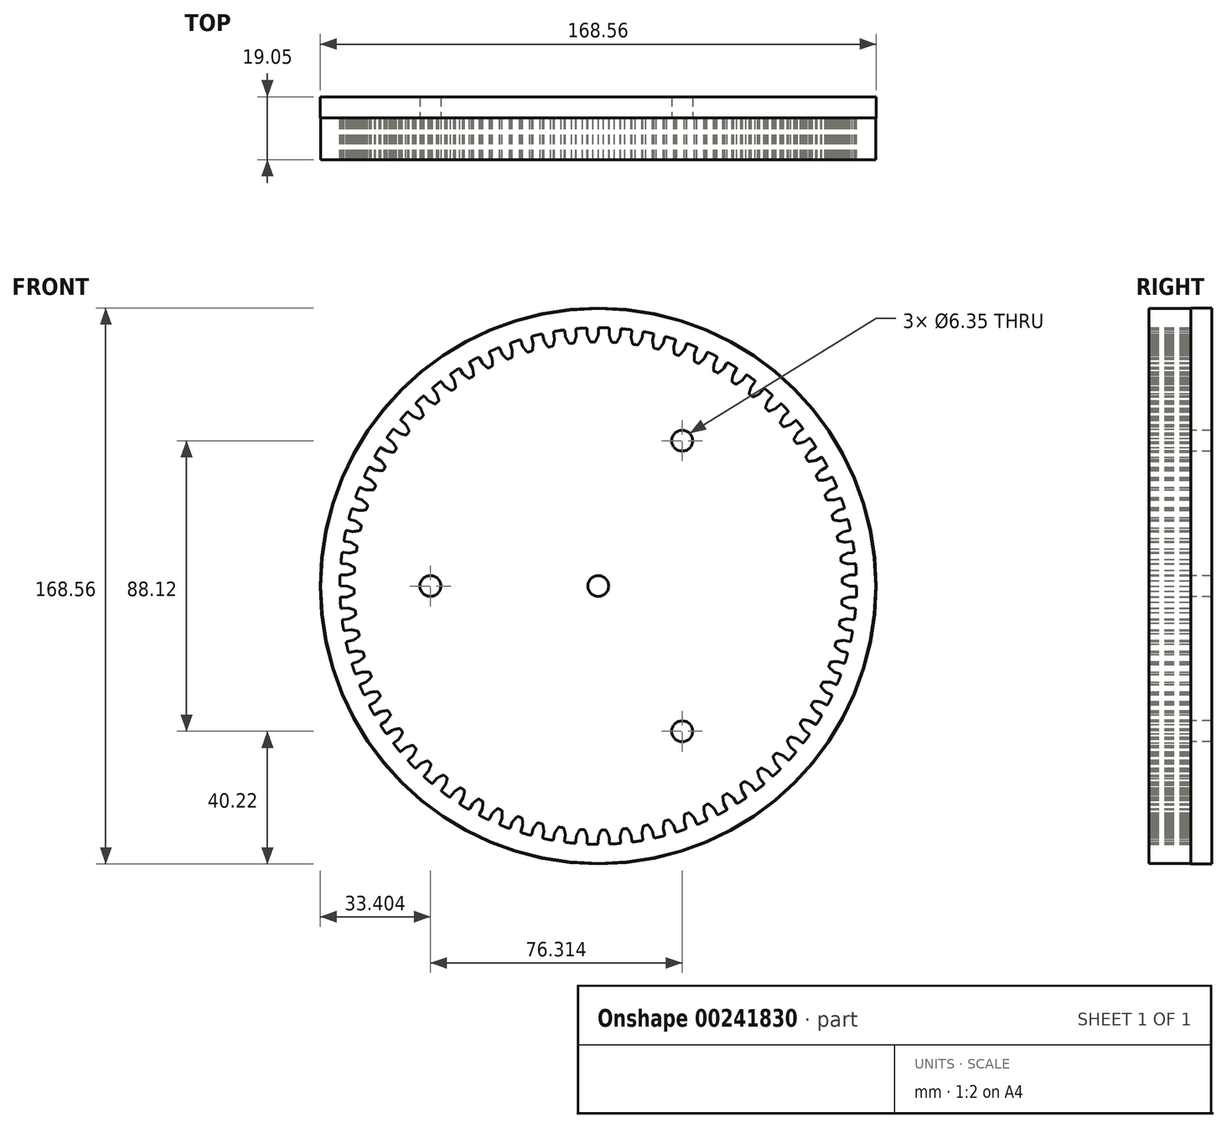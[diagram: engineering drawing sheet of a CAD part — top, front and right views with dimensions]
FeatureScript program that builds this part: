
annotation { "Feature Type Name" : "Feature", "Feature Type Description" : "" }
export const myFeature = defineFeature(function(context is Context, id is Id, definition is map)
    precondition{}
    {
        {
            var Q0;
            Q0=qCreatedBy(makeId("Front.planeOp"),FACE);
            var sketch = newSketch(context, id + "F0", { "sketchPlane" : qUnion([Q0])});
            skArc(sketch, "E0", {"start": v(-3.79, 78.22) * mm, "mid": v(-5.3, 78.14) * mm, "end": v(-6.81, 78.02) * mm});
            skPoint(sketch, "E1.orphan", {"position": v(0.25, 70.42) * mm});
            skPoint(sketch, "E2.orphan", {"position": v(-3.32, 70.34) * mm});
            skArc(sketch, "E3.MirrorCS", {"start": v(-3.32, 76.11) * mm, "mid": v(-2.93, 75.15) * mm, "end": v(-2.48, 74.2) * mm});
            skLineSegment(sketch, "E4.MirrorCS", {"start": v(-2.14, 74) * mm, "end": v(-1.63, 74) * mm});
            skLineSegment(sketch, "E5.MirrorCS", {"start": v(-1.12, 74.01) * mm, "end": v(-1.63, 74) * mm});
            skArc(sketch, "E6.MirrorCS", {"start": v(0, 76.17) * mm, "mid": v(-0.36, 75.19) * mm, "end": v(-0.78, 74.23) * mm});
            skLineSegment(sketch, "E7", {"start": v(-3.32, 76.11) * mm, "end": v(-3.39, 77.86) * mm});
            skLineSegment(sketch, "E8", {"start": v(0, 76.17) * mm, "end": v(0.01, 77.94) * mm});
            skCircle(sketch, "E9", {"center": v(0, 0) * mm, "radius": 84.1 * mm});
            skPoint(sketch, "E10.visualSharp", {"position": v(-3.4, 78.24) * mm});
            skArc(sketch, "E10.filletArc", {"start": v(-3.39, 77.86) * mm, "mid": v(-3.51, 78.13) * mm, "end": v(-3.79, 78.22) * mm});
            skPoint(sketch, "E11.visualSharp", {"position": v(0.01, 78.32) * mm});
            skArc(sketch, "E11.filletArc", {"start": v(0.4, 78.32) * mm, "mid": v(0.12, 78.2) * mm, "end": v(0.01, 77.94) * mm});
            skPoint(sketch, "E12.visualSharp", {"position": v(-0.88, 74.02) * mm});
            skArc(sketch, "E12.filletArc", {"start": v(-1.12, 74.01) * mm, "mid": v(-0.92, 74.08) * mm, "end": v(-0.78, 74.23) * mm});
            skPoint(sketch, "E13.visualSharp", {"position": v(-2.37, 74) * mm});
            skArc(sketch, "E13.filletArc", {"start": v(-2.48, 74.2) * mm, "mid": v(-2.34, 74.05) * mm, "end": v(-2.14, 74) * mm});
            skArc(sketch, "E14.1.0", {"start": v(-6.64, 75.88) * mm, "mid": v(-6.92, 74.87) * mm, "end": v(-7.25, 73.88) * mm});
            skArc(sketch, "E14.1.1", {"start": v(-9.94, 75.53) * mm, "mid": v(-9.47, 74.6) * mm, "end": v(-8.94, 73.7) * mm});
            skPoint(sketch, "E14.1.2", {"position": v(-6.81, 78.02) * mm});
            skPoint(sketch, "E14.1.3", {"position": v(-7.33, 73.66) * mm});
            skLineSegment(sketch, "E14.1.4", {"start": v(-6.64, 75.88) * mm, "end": v(-6.78, 77.64) * mm});
            skLineSegment(sketch, "E14.1.5", {"start": v(-9.94, 75.53) * mm, "end": v(-10.16, 77.27) * mm});
            skPoint(sketch, "E14.1.6", {"position": v(-8.81, 73.5) * mm});
            skLineSegment(sketch, "E14.1.7", {"start": v(-7.56, 73.64) * mm, "end": v(-8.07, 73.58) * mm});
            skLineSegment(sketch, "E14.1.8", {"start": v(-8.58, 73.53) * mm, "end": v(-8.07, 73.58) * mm});
            skArc(sketch, "E14.1.9", {"start": v(-7.56, 73.64) * mm, "mid": v(-7.37, 73.71) * mm, "end": v(-7.25, 73.88) * mm});
            skArc(sketch, "E14.1.10", {"start": v(-8.94, 73.7) * mm, "mid": v(-8.78, 73.57) * mm, "end": v(-8.58, 73.53) * mm});
            skArc(sketch, "E14.1.11", {"start": v(-6.43, 78.05) * mm, "mid": v(-6.7, 77.92) * mm, "end": v(-6.78, 77.64) * mm});
            skArc(sketch, "E14.1.12", {"start": v(-10.16, 77.27) * mm, "mid": v(-10.3, 77.52) * mm, "end": v(-10.6, 77.6) * mm});
            skArc(sketch, "E14.2.0", {"start": v(-13.23, 75) * mm, "mid": v(-13.41, 73.98) * mm, "end": v(-13.66, 72.97) * mm});
            skArc(sketch, "E14.2.1", {"start": v(-16.49, 74.38) * mm, "mid": v(-15.93, 73.5) * mm, "end": v(-15.33, 72.65) * mm});
            skPoint(sketch, "E14.2.2", {"position": v(-13.59, 77.13) * mm});
            skPoint(sketch, "E14.2.3", {"position": v(-13.72, 72.74) * mm});
            skLineSegment(sketch, "E14.2.4", {"start": v(-13.23, 75) * mm, "end": v(-13.52, 76.75) * mm});
            skLineSegment(sketch, "E14.2.5", {"start": v(-16.49, 74.38) * mm, "end": v(-16.86, 76.09) * mm});
            skPoint(sketch, "E14.2.6", {"position": v(-15.19, 72.46) * mm});
            skLineSegment(sketch, "E14.2.7", {"start": v(-13.95, 72.7) * mm, "end": v(-14.45, 72.6) * mm});
            skLineSegment(sketch, "E14.2.8", {"start": v(-14.96, 72.5) * mm, "end": v(-14.45, 72.6) * mm});
            skArc(sketch, "E14.2.9", {"start": v(-13.95, 72.7) * mm, "mid": v(-13.77, 72.8) * mm, "end": v(-13.66, 72.97) * mm});
            skArc(sketch, "E14.2.10", {"start": v(-15.33, 72.65) * mm, "mid": v(-15.16, 72.52) * mm, "end": v(-14.96, 72.5) * mm});
            skArc(sketch, "E14.2.11", {"start": v(-13.21, 77.2) * mm, "mid": v(-13.46, 77.04) * mm, "end": v(-13.52, 76.75) * mm});
            skArc(sketch, "E14.2.12", {"start": v(-16.86, 76.09) * mm, "mid": v(-17.03, 76.33) * mm, "end": v(-17.32, 76.38) * mm});
            skArc(sketch, "E14.3.0", {"start": v(-19.71, 73.57) * mm, "mid": v(-19.81, 72.53) * mm, "end": v(-19.97, 71.5) * mm});
            skArc(sketch, "E14.3.1", {"start": v(-22.9, 72.66) * mm, "mid": v(-22.28, 71.83) * mm, "end": v(-21.6, 71.04) * mm});
            skPoint(sketch, "E14.3.2", {"position": v(-20.26, 75.65) * mm});
            skPoint(sketch, "E14.3.3", {"position": v(-20, 71.27) * mm});
            skLineSegment(sketch, "E14.3.4", {"start": v(-19.71, 73.57) * mm, "end": v(-20.16, 75.28) * mm});
            skLineSegment(sketch, "E14.3.5", {"start": v(-22.9, 72.66) * mm, "end": v(-23.43, 74.33) * mm});
            skPoint(sketch, "E14.3.6", {"position": v(-21.44, 70.86) * mm});
            skLineSegment(sketch, "E14.3.7", {"start": v(-20.23, 71.2) * mm, "end": v(-20.72, 71.06) * mm});
            skLineSegment(sketch, "E14.3.8", {"start": v(-21.22, 70.92) * mm, "end": v(-20.72, 71.06) * mm});
            skArc(sketch, "E14.3.9", {"start": v(-20.23, 71.2) * mm, "mid": v(-20.06, 71.32) * mm, "end": v(-19.97, 71.5) * mm});
            skArc(sketch, "E14.3.10", {"start": v(-21.6, 71.04) * mm, "mid": v(-21.43, 70.92) * mm, "end": v(-21.22, 70.92) * mm});
            skArc(sketch, "E14.3.11", {"start": v(-19.89, 75.75) * mm, "mid": v(-20.12, 75.57) * mm, "end": v(-20.16, 75.28) * mm});
            skArc(sketch, "E14.3.12", {"start": v(-23.43, 74.33) * mm, "mid": v(-23.61, 74.55) * mm, "end": v(-23.9, 74.58) * mm});
            skArc(sketch, "E14.4.0", {"start": v(-26.05, 71.57) * mm, "mid": v(-26.06, 70.53) * mm, "end": v(-26.12, 69.5) * mm});
            skArc(sketch, "E14.4.1", {"start": v(-29.16, 70.39) * mm, "mid": v(-28.45, 69.61) * mm, "end": v(-27.71, 68.88) * mm});
            skPoint(sketch, "E14.4.2", {"position": v(-26.77, 73.6) * mm});
            skPoint(sketch, "E14.4.3", {"position": v(-26.15, 69.26) * mm});
            skLineSegment(sketch, "E14.4.4", {"start": v(-26.05, 71.57) * mm, "end": v(-26.65, 73.24) * mm});
            skLineSegment(sketch, "E14.4.5", {"start": v(-29.16, 70.39) * mm, "end": v(-29.81, 72) * mm});
            skPoint(sketch, "E14.4.6", {"position": v(-27.54, 68.72) * mm});
            skLineSegment(sketch, "E14.4.7", {"start": v(-26.36, 69.17) * mm, "end": v(-26.84, 68.98) * mm});
            skLineSegment(sketch, "E14.4.8", {"start": v(-27.32, 68.8) * mm, "end": v(-26.84, 68.98) * mm});
            skArc(sketch, "E14.4.9", {"start": v(-26.36, 69.17) * mm, "mid": v(-26.2, 69.3) * mm, "end": v(-26.12, 69.5) * mm});
            skArc(sketch, "E14.4.10", {"start": v(-27.71, 68.88) * mm, "mid": v(-27.53, 68.79) * mm, "end": v(-27.32, 68.8) * mm});
            skArc(sketch, "E14.4.11", {"start": v(-26.42, 73.73) * mm, "mid": v(-26.63, 73.53) * mm, "end": v(-26.65, 73.24) * mm});
            skArc(sketch, "E14.4.12", {"start": v(-29.81, 72) * mm, "mid": v(-30.02, 72.21) * mm, "end": v(-30.31, 72.21) * mm});
            skArc(sketch, "E14.5.0", {"start": v(-32.19, 69.03) * mm, "mid": v(-32.1, 68) * mm, "end": v(-32.08, 66.95) * mm});
            skArc(sketch, "E14.5.1", {"start": v(-35.18, 67.58) * mm, "mid": v(-34.41, 66.87) * mm, "end": v(-33.6, 66.2) * mm});
            skPoint(sketch, "E14.5.2", {"position": v(-33.09, 70.98) * mm});
            skPoint(sketch, "E14.5.3", {"position": v(-32.08, 66.71) * mm});
            skLineSegment(sketch, "E14.5.4", {"start": v(-32.19, 69.03) * mm, "end": v(-32.93, 70.64) * mm});
            skLineSegment(sketch, "E14.5.5", {"start": v(-35.18, 67.58) * mm, "end": v(-35.98, 69.13) * mm});
            skPoint(sketch, "E14.5.6", {"position": v(-33.42, 66.06) * mm});
            skLineSegment(sketch, "E14.5.7", {"start": v(-32.3, 66.6) * mm, "end": v(-32.75, 66.38) * mm});
            skLineSegment(sketch, "E14.5.8", {"start": v(-33.21, 66.16) * mm, "end": v(-32.75, 66.38) * mm});
            skArc(sketch, "E14.5.9", {"start": v(-32.3, 66.6) * mm, "mid": v(-32.14, 66.75) * mm, "end": v(-32.08, 66.95) * mm});
            skArc(sketch, "E14.5.10", {"start": v(-33.6, 66.2) * mm, "mid": v(-33.42, 66.13) * mm, "end": v(-33.21, 66.16) * mm});
            skArc(sketch, "E14.5.11", {"start": v(-32.74, 71.14) * mm, "mid": v(-32.94, 70.93) * mm, "end": v(-32.93, 70.64) * mm});
            skArc(sketch, "E14.5.12", {"start": v(-35.98, 69.13) * mm, "mid": v(-36.2, 69.32) * mm, "end": v(-36.5, 69.3) * mm});
            skArc(sketch, "E14.6.0", {"start": v(-38.08, 65.96) * mm, "mid": v(-37.9, 64.93) * mm, "end": v(-37.8, 63.9) * mm});
            skArc(sketch, "E14.6.1", {"start": v(-40.93, 64.25) * mm, "mid": v(-40.1, 63.62) * mm, "end": v(-39.25, 63.02) * mm});
            skPoint(sketch, "E14.6.2", {"position": v(-39.15, 67.83) * mm});
            skPoint(sketch, "E14.6.3", {"position": v(-37.77, 63.66) * mm});
            skLineSegment(sketch, "E14.6.4", {"start": v(-38.08, 65.96) * mm, "end": v(-38.96, 67.5) * mm});
            skLineSegment(sketch, "E14.6.5", {"start": v(-40.93, 64.25) * mm, "end": v(-41.87, 65.73) * mm});
            skPoint(sketch, "E14.6.6", {"position": v(-39.05, 62.9) * mm});
            skLineSegment(sketch, "E14.6.7", {"start": v(-37.97, 63.54) * mm, "end": v(-38.4, 63.27) * mm});
            skLineSegment(sketch, "E14.6.8", {"start": v(-38.85, 63.01) * mm, "end": v(-38.4, 63.27) * mm});
            skArc(sketch, "E14.6.9", {"start": v(-37.97, 63.54) * mm, "mid": v(-37.83, 63.7) * mm, "end": v(-37.8, 63.9) * mm});
            skArc(sketch, "E14.6.10", {"start": v(-39.25, 63.02) * mm, "mid": v(-39.05, 62.96) * mm, "end": v(-38.85, 63.01) * mm});
            skArc(sketch, "E14.6.11", {"start": v(-38.82, 68.02) * mm, "mid": v(-39, 67.79) * mm, "end": v(-38.96, 67.5) * mm});
            skArc(sketch, "E14.6.12", {"start": v(-41.87, 65.73) * mm, "mid": v(-42.1, 65.9) * mm, "end": v(-42.4, 65.85) * mm});
            skArc(sketch, "E14.7.0", {"start": v(-43.69, 62.4) * mm, "mid": v(-43.42, 61.38) * mm, "end": v(-43.22, 60.36) * mm});
            skArc(sketch, "E14.7.1", {"start": v(-46.38, 60.44) * mm, "mid": v(-45.5, 59.88) * mm, "end": v(-44.6, 59.36) * mm});
            skPoint(sketch, "E14.7.2", {"position": v(-44.91, 64.16) * mm});
            skPoint(sketch, "E14.7.3", {"position": v(-43.18, 60.13) * mm});
            skLineSegment(sketch, "E14.7.4", {"start": v(-43.69, 62.4) * mm, "end": v(-44.7, 63.85) * mm});
            skLineSegment(sketch, "E14.7.5", {"start": v(-46.38, 60.44) * mm, "end": v(-47.43, 61.83) * mm});
            skPoint(sketch, "E14.7.6", {"position": v(-44.39, 59.25) * mm});
            skLineSegment(sketch, "E14.7.7", {"start": v(-43.37, 59.99) * mm, "end": v(-43.78, 59.69) * mm});
            skLineSegment(sketch, "E14.7.8", {"start": v(-44.2, 59.39) * mm, "end": v(-43.78, 59.69) * mm});
            skArc(sketch, "E14.7.9", {"start": v(-43.37, 59.99) * mm, "mid": v(-43.24, 60.15) * mm, "end": v(-43.22, 60.36) * mm});
            skArc(sketch, "E14.7.10", {"start": v(-44.6, 59.36) * mm, "mid": v(-44.4, 59.32) * mm, "end": v(-44.2, 59.39) * mm});
            skArc(sketch, "E14.7.11", {"start": v(-44.6, 64.38) * mm, "mid": v(-44.76, 64.13) * mm, "end": v(-44.7, 63.85) * mm});
            skArc(sketch, "E14.7.12", {"start": v(-47.43, 61.83) * mm, "mid": v(-47.69, 61.98) * mm, "end": v(-47.97, 61.9) * mm});
            skArc(sketch, "E14.8.0", {"start": v(-48.96, 58.35) * mm, "mid": v(-48.6, 57.36) * mm, "end": v(-48.31, 56.36) * mm});
            skArc(sketch, "E14.8.1", {"start": v(-51.47, 56.17) * mm, "mid": v(-50.55, 55.68) * mm, "end": v(-49.6, 55.25) * mm});
            skPoint(sketch, "E14.8.2", {"position": v(-50.33, 60) * mm});
            skPoint(sketch, "E14.8.3", {"position": v(-48.26, 56.14) * mm});
            skLineSegment(sketch, "E14.8.4", {"start": v(-48.96, 58.35) * mm, "end": v(-50.09, 59.7) * mm});
            skLineSegment(sketch, "E14.8.5", {"start": v(-51.47, 56.17) * mm, "end": v(-52.64, 57.46) * mm});
            skPoint(sketch, "E14.8.6", {"position": v(-49.38, 55.16) * mm});
            skLineSegment(sketch, "E14.8.7", {"start": v(-48.43, 55.98) * mm, "end": v(-48.81, 55.64) * mm});
            skLineSegment(sketch, "E14.8.8", {"start": v(-49.2, 55.31) * mm, "end": v(-48.81, 55.64) * mm});
            skArc(sketch, "E14.8.9", {"start": v(-48.43, 55.98) * mm, "mid": v(-48.32, 56.16) * mm, "end": v(-48.31, 56.36) * mm});
            skArc(sketch, "E14.8.10", {"start": v(-49.6, 55.25) * mm, "mid": v(-49.4, 55.22) * mm, "end": v(-49.2, 55.31) * mm});
            skArc(sketch, "E14.8.11", {"start": v(-50.04, 60.25) * mm, "mid": v(-50.17, 59.99) * mm, "end": v(-50.09, 59.7) * mm});
            skArc(sketch, "E14.8.12", {"start": v(-52.64, 57.46) * mm, "mid": v(-52.9, 57.59) * mm, "end": v(-53.18, 57.49) * mm});
            skArc(sketch, "E14.9.0", {"start": v(-53.86, 53.86) * mm, "mid": v(-53.42, 52.91) * mm, "end": v(-53.04, 51.94) * mm});
            skArc(sketch, "E14.9.1", {"start": v(-56.17, 51.47) * mm, "mid": v(-55.2, 51.07) * mm, "end": v(-54.23, 50.72) * mm});
            skPoint(sketch, "E14.9.2", {"position": v(-55.37, 55.39) * mm});
            skPoint(sketch, "E14.9.3", {"position": v(-52.96, 51.72) * mm});
            skLineSegment(sketch, "E14.9.4", {"start": v(-53.86, 53.86) * mm, "end": v(-55.1, 55.12) * mm});
            skLineSegment(sketch, "E14.9.5", {"start": v(-56.17, 51.47) * mm, "end": v(-57.45, 52.66) * mm});
            skPoint(sketch, "E14.9.6", {"position": v(-54, 50.65) * mm});
            skLineSegment(sketch, "E14.9.7", {"start": v(-53.12, 51.55) * mm, "end": v(-53.48, 51.18) * mm});
            skLineSegment(sketch, "E14.9.8", {"start": v(-53.84, 50.81) * mm, "end": v(-53.48, 51.18) * mm});
            skArc(sketch, "E14.9.9", {"start": v(-53.12, 51.55) * mm, "mid": v(-53.03, 51.73) * mm, "end": v(-53.04, 51.94) * mm});
            skArc(sketch, "E14.9.10", {"start": v(-54.23, 50.72) * mm, "mid": v(-54.02, 50.7) * mm, "end": v(-53.84, 50.81) * mm});
            skArc(sketch, "E14.9.11", {"start": v(-55.1, 55.66) * mm, "mid": v(-55.21, 55.39) * mm, "end": v(-55.1, 55.12) * mm});
            skArc(sketch, "E14.9.12", {"start": v(-57.45, 52.66) * mm, "mid": v(-57.73, 52.76) * mm, "end": v(-58, 52.63) * mm});
            skArc(sketch, "E14.10.0", {"start": v(-58.35, 48.96) * mm, "mid": v(-57.83, 48.05) * mm, "end": v(-57.37, 47.12) * mm});
            skArc(sketch, "E14.10.1", {"start": v(-60.44, 46.38) * mm, "mid": v(-59.45, 46.06) * mm, "end": v(-58.44, 45.8) * mm});
            skPoint(sketch, "E14.10.2", {"position": v(-59.99, 50.35) * mm});
            skPoint(sketch, "E14.10.3", {"position": v(-57.27, 46.9) * mm});
            skLineSegment(sketch, "E14.10.4", {"start": v(-58.35, 48.96) * mm, "end": v(-59.7, 50.1) * mm});
            skLineSegment(sketch, "E14.10.5", {"start": v(-60.44, 46.38) * mm, "end": v(-61.82, 47.45) * mm});
            skPoint(sketch, "E14.10.6", {"position": v(-58.2, 45.75) * mm});
            skLineSegment(sketch, "E14.10.7", {"start": v(-57.42, 46.72) * mm, "end": v(-57.73, 46.32) * mm});
            skLineSegment(sketch, "E14.10.8", {"start": v(-58.06, 45.93) * mm, "end": v(-57.73, 46.32) * mm});
            skArc(sketch, "E14.10.9", {"start": v(-57.42, 46.72) * mm, "mid": v(-57.34, 46.91) * mm, "end": v(-57.37, 47.12) * mm});
            skArc(sketch, "E14.10.10", {"start": v(-58.44, 45.8) * mm, "mid": v(-58.23, 45.8) * mm, "end": v(-58.06, 45.93) * mm});
            skArc(sketch, "E14.10.11", {"start": v(-59.74, 50.64) * mm, "mid": v(-59.83, 50.36) * mm, "end": v(-59.7, 50.1) * mm});
            skArc(sketch, "E14.10.12", {"start": v(-61.82, 47.45) * mm, "mid": v(-62.1, 47.53) * mm, "end": v(-62.36, 47.38) * mm});
            skArc(sketch, "E14.11.0", {"start": v(-62.4, 43.69) * mm, "mid": v(-61.8, 42.83) * mm, "end": v(-61.26, 41.94) * mm});
            skArc(sketch, "E14.11.1", {"start": v(-64.25, 40.93) * mm, "mid": v(-63.24, 40.7) * mm, "end": v(-62.2, 40.53) * mm});
            skPoint(sketch, "E14.11.2", {"position": v(-64.15, 44.93) * mm});
            skPoint(sketch, "E14.11.3", {"position": v(-61.14, 41.73) * mm});
            skLineSegment(sketch, "E14.11.4", {"start": v(-62.4, 43.69) * mm, "end": v(-63.84, 44.71) * mm});
            skLineSegment(sketch, "E14.11.5", {"start": v(-64.25, 40.93) * mm, "end": v(-65.72, 41.88) * mm});
            skPoint(sketch, "E14.11.6", {"position": v(-61.98, 40.5) * mm});
            skLineSegment(sketch, "E14.11.7", {"start": v(-61.27, 41.54) * mm, "end": v(-61.55, 41.11) * mm});
            skLineSegment(sketch, "E14.11.8", {"start": v(-61.84, 40.7) * mm, "end": v(-61.55, 41.11) * mm});
            skArc(sketch, "E14.11.9", {"start": v(-61.27, 41.54) * mm, "mid": v(-61.2, 41.74) * mm, "end": v(-61.26, 41.94) * mm});
            skArc(sketch, "E14.11.10", {"start": v(-62.2, 40.53) * mm, "mid": v(-62, 40.56) * mm, "end": v(-61.84, 40.7) * mm});
            skArc(sketch, "E14.11.11", {"start": v(-63.93, 45.24) * mm, "mid": v(-64, 44.96) * mm, "end": v(-63.84, 44.71) * mm});
            skArc(sketch, "E14.11.12", {"start": v(-65.72, 41.88) * mm, "mid": v(-66.01, 41.93) * mm, "end": v(-66.25, 41.76) * mm});
            skArc(sketch, "E14.12.0", {"start": v(-65.96, 38.08) * mm, "mid": v(-65.3, 37.28) * mm, "end": v(-64.68, 36.44) * mm});
            skArc(sketch, "E14.12.1", {"start": v(-67.58, 35.18) * mm, "mid": v(-66.54, 35.04) * mm, "end": v(-65.5, 34.95) * mm});
            skPoint(sketch, "E14.12.2", {"position": v(-67.82, 39.17) * mm});
            skPoint(sketch, "E14.12.3", {"position": v(-64.54, 36.25) * mm});
            skLineSegment(sketch, "E14.12.4", {"start": v(-65.96, 38.08) * mm, "end": v(-67.49, 38.98) * mm});
            skLineSegment(sketch, "E14.12.5", {"start": v(-67.58, 35.18) * mm, "end": v(-69.12, 36) * mm});
            skPoint(sketch, "E14.12.6", {"position": v(-65.27, 34.94) * mm});
            skLineSegment(sketch, "E14.12.7", {"start": v(-64.66, 36.04) * mm, "end": v(-64.9, 35.6) * mm});
            skLineSegment(sketch, "E14.12.8", {"start": v(-65.15, 35.15) * mm, "end": v(-64.9, 35.6) * mm});
            skArc(sketch, "E14.12.9", {"start": v(-64.66, 36.04) * mm, "mid": v(-64.61, 36.24) * mm, "end": v(-64.68, 36.44) * mm});
            skArc(sketch, "E14.12.10", {"start": v(-65.5, 34.95) * mm, "mid": v(-65.3, 35) * mm, "end": v(-65.15, 35.15) * mm});
            skArc(sketch, "E14.12.11", {"start": v(-67.63, 39.5) * mm, "mid": v(-67.67, 39.2) * mm, "end": v(-67.49, 38.98) * mm});
            skArc(sketch, "E14.12.12", {"start": v(-69.12, 36) * mm, "mid": v(-69.41, 36.02) * mm, "end": v(-69.64, 35.83) * mm});
            skArc(sketch, "E14.13.0", {"start": v(-69.03, 32.19) * mm, "mid": v(-68.3, 31.45) * mm, "end": v(-67.6, 30.67) * mm});
            skArc(sketch, "E14.13.1", {"start": v(-70.39, 29.15) * mm, "mid": v(-69.34, 29.1) * mm, "end": v(-68.3, 29.11) * mm});
            skPoint(sketch, "E14.13.2", {"position": v(-70.97, 33.1) * mm});
            skPoint(sketch, "E14.13.3", {"position": v(-67.46, 30.48) * mm});
            skLineSegment(sketch, "E14.13.4", {"start": v(-69.03, 32.19) * mm, "end": v(-70.63, 32.95) * mm});
            skLineSegment(sketch, "E14.13.5", {"start": v(-70.39, 29.15) * mm, "end": v(-72, 29.83) * mm});
            skPoint(sketch, "E14.13.6", {"position": v(-68.07, 29.12) * mm});
            skLineSegment(sketch, "E14.13.7", {"start": v(-67.55, 30.27) * mm, "end": v(-67.76, 29.8) * mm});
            skLineSegment(sketch, "E14.13.8", {"start": v(-67.97, 29.33) * mm, "end": v(-67.76, 29.8) * mm});
            skArc(sketch, "E14.13.9", {"start": v(-67.55, 30.27) * mm, "mid": v(-67.52, 30.48) * mm, "end": v(-67.6, 30.67) * mm});
            skArc(sketch, "E14.13.10", {"start": v(-68.3, 29.11) * mm, "mid": v(-68.1, 29.18) * mm, "end": v(-67.97, 29.33) * mm});
            skArc(sketch, "E14.13.11", {"start": v(-70.81, 33.45) * mm, "mid": v(-70.83, 33.16) * mm, "end": v(-70.63, 32.95) * mm});
            skArc(sketch, "E14.13.12", {"start": v(-72, 29.83) * mm, "mid": v(-72.3, 29.83) * mm, "end": v(-72.5, 29.63) * mm});
            skArc(sketch, "E14.14.0", {"start": v(-71.57, 26.05) * mm, "mid": v(-70.78, 25.37) * mm, "end": v(-70.02, 24.66) * mm});
            skArc(sketch, "E14.14.1", {"start": v(-72.66, 22.9) * mm, "mid": v(-71.62, 22.95) * mm, "end": v(-70.58, 23.05) * mm});
            skPoint(sketch, "E14.14.2", {"position": v(-73.59, 26.8) * mm});
            skPoint(sketch, "E14.14.3", {"position": v(-69.86, 24.49) * mm});
            skLineSegment(sketch, "E14.14.4", {"start": v(-71.57, 26.05) * mm, "end": v(-73.23, 26.67) * mm});
            skLineSegment(sketch, "E14.14.5", {"start": v(-72.66, 22.9) * mm, "end": v(-74.32, 23.44) * mm});
            skPoint(sketch, "E14.14.6", {"position": v(-70.35, 23.08) * mm});
            skLineSegment(sketch, "E14.14.7", {"start": v(-69.93, 24.27) * mm, "end": v(-70.1, 23.78) * mm});
            skLineSegment(sketch, "E14.14.8", {"start": v(-70.27, 23.3) * mm, "end": v(-70.1, 23.78) * mm});
            skArc(sketch, "E14.14.9", {"start": v(-69.93, 24.27) * mm, "mid": v(-69.92, 24.47) * mm, "end": v(-70.02, 24.66) * mm});
            skArc(sketch, "E14.14.10", {"start": v(-70.58, 23.05) * mm, "mid": v(-70.39, 23.13) * mm, "end": v(-70.27, 23.3) * mm});
            skArc(sketch, "E14.14.11", {"start": v(-73.46, 27.16) * mm, "mid": v(-73.45, 26.86) * mm, "end": v(-73.23, 26.67) * mm});
            skArc(sketch, "E14.14.12", {"start": v(-74.32, 23.44) * mm, "mid": v(-74.62, 23.42) * mm, "end": v(-74.8, 23.2) * mm});
            skArc(sketch, "E14.15.0", {"start": v(-73.57, 19.71) * mm, "mid": v(-72.72, 19.1) * mm, "end": v(-71.9, 18.46) * mm});
            skArc(sketch, "E14.15.1", {"start": v(-74.38, 16.49) * mm, "mid": v(-73.35, 16.62) * mm, "end": v(-72.32, 16.8) * mm});
            skPoint(sketch, "E14.15.2", {"position": v(-75.64, 20.28) * mm});
            skPoint(sketch, "E14.15.3", {"position": v(-71.73, 18.3) * mm});
            skLineSegment(sketch, "E14.15.4", {"start": v(-73.57, 19.71) * mm, "end": v(-75.28, 20.18) * mm});
            skLineSegment(sketch, "E14.15.5", {"start": v(-74.38, 16.49) * mm, "end": v(-76.08, 16.88) * mm});
            skPoint(sketch, "E14.15.6", {"position": v(-72.09, 16.86) * mm});
            skLineSegment(sketch, "E14.15.7", {"start": v(-71.78, 18.08) * mm, "end": v(-71.9, 17.58) * mm});
            skLineSegment(sketch, "E14.15.8", {"start": v(-72.03, 17.09) * mm, "end": v(-71.9, 17.58) * mm});
            skArc(sketch, "E14.15.9", {"start": v(-71.78, 18.08) * mm, "mid": v(-71.79, 18.29) * mm, "end": v(-71.9, 18.46) * mm});
            skArc(sketch, "E14.15.10", {"start": v(-72.32, 16.8) * mm, "mid": v(-72.14, 16.9) * mm, "end": v(-72.03, 17.09) * mm});
            skArc(sketch, "E14.15.11", {"start": v(-75.55, 20.65) * mm, "mid": v(-75.5, 20.36) * mm, "end": v(-75.28, 20.18) * mm});
            skArc(sketch, "E14.15.12", {"start": v(-76.08, 16.88) * mm, "mid": v(-76.37, 16.83) * mm, "end": v(-76.54, 16.59) * mm});
            skArc(sketch, "E14.16.0", {"start": v(-75, 13.23) * mm, "mid": v(-74.11, 12.7) * mm, "end": v(-73.24, 12.12) * mm});
            skArc(sketch, "E14.16.1", {"start": v(-75.53, 9.94) * mm, "mid": v(-74.51, 10.17) * mm, "end": v(-73.5, 10.44) * mm});
            skPoint(sketch, "E14.16.2", {"position": v(-77.12, 13.61) * mm});
            skPoint(sketch, "E14.16.3", {"position": v(-73.05, 11.99) * mm});
            skLineSegment(sketch, "E14.16.4", {"start": v(-75, 13.23) * mm, "end": v(-76.75, 13.54) * mm});
            skLineSegment(sketch, "E14.16.5", {"start": v(-75.53, 9.94) * mm, "end": v(-77.26, 10.18) * mm});
            skPoint(sketch, "E14.16.6", {"position": v(-73.28, 10.51) * mm});
            skLineSegment(sketch, "E14.16.7", {"start": v(-73.08, 11.75) * mm, "end": v(-73.16, 11.25) * mm});
            skLineSegment(sketch, "E14.16.8", {"start": v(-73.25, 10.74) * mm, "end": v(-73.16, 11.25) * mm});
            skArc(sketch, "E14.16.9", {"start": v(-73.08, 11.75) * mm, "mid": v(-73.11, 11.96) * mm, "end": v(-73.24, 12.12) * mm});
            skArc(sketch, "E14.16.10", {"start": v(-73.5, 10.44) * mm, "mid": v(-73.33, 10.56) * mm, "end": v(-73.25, 10.74) * mm});
            skArc(sketch, "E14.16.11", {"start": v(-77.06, 13.99) * mm, "mid": v(-77, 13.7) * mm, "end": v(-76.75, 13.54) * mm});
            skArc(sketch, "E14.16.12", {"start": v(-77.26, 10.18) * mm, "mid": v(-77.55, 10.1) * mm, "end": v(-77.7, 9.85) * mm});
            skArc(sketch, "E14.17.0", {"start": v(-75.88, 6.64) * mm, "mid": v(-74.93, 6.2) * mm, "end": v(-74.02, 5.7) * mm});
            skArc(sketch, "E14.17.1", {"start": v(-76.11, 3.32) * mm, "mid": v(-75.12, 3.63) * mm, "end": v(-74.14, 4) * mm});
            skPoint(sketch, "E14.17.2", {"position": v(-78.02, 6.84) * mm});
            skPoint(sketch, "E14.17.3", {"position": v(-73.82, 5.57) * mm});
            skLineSegment(sketch, "E14.17.4", {"start": v(-75.88, 6.64) * mm, "end": v(-77.64, 6.8) * mm});
            skLineSegment(sketch, "E14.17.5", {"start": v(-76.11, 3.32) * mm, "end": v(-77.86, 3.4) * mm});
            skPoint(sketch, "E14.17.6", {"position": v(-73.92, 4.09) * mm});
            skLineSegment(sketch, "E14.17.7", {"start": v(-73.83, 5.34) * mm, "end": v(-73.86, 4.83) * mm});
            skLineSegment(sketch, "E14.17.8", {"start": v(-73.9, 4.32) * mm, "end": v(-73.86, 4.83) * mm});
            skArc(sketch, "E14.17.9", {"start": v(-73.83, 5.34) * mm, "mid": v(-73.87, 5.54) * mm, "end": v(-74.02, 5.7) * mm});
            skArc(sketch, "E14.17.10", {"start": v(-74.14, 4) * mm, "mid": v(-73.98, 4.12) * mm, "end": v(-73.9, 4.32) * mm});
            skArc(sketch, "E14.17.11", {"start": v(-77.98, 7.22) * mm, "mid": v(-77.9, 6.94) * mm, "end": v(-77.64, 6.8) * mm});
            skArc(sketch, "E14.17.12", {"start": v(-77.86, 3.4) * mm, "mid": v(-78.13, 3.3) * mm, "end": v(-78.26, 3.04) * mm});
            skArc(sketch, "E14.18.0", {"start": v(-76.17, 0) * mm, "mid": v(-75.19, -0.36) * mm, "end": v(-74.23, -0.78) * mm});
            skArc(sketch, "E14.18.1", {"start": v(-76.11, -3.32) * mm, "mid": v(-75.15, -2.93) * mm, "end": v(-74.2, -2.48) * mm});
            skPoint(sketch, "E14.18.2", {"position": v(-78.32, 0.01) * mm});
            skPoint(sketch, "E14.18.3", {"position": v(-74.02, -0.88) * mm});
            skLineSegment(sketch, "E14.18.4", {"start": v(-76.17, 0) * mm, "end": v(-77.94, 0.01) * mm});
            skLineSegment(sketch, "E14.18.5", {"start": v(-76.11, -3.32) * mm, "end": v(-77.86, -3.39) * mm});
            skPoint(sketch, "E14.18.6", {"position": v(-74, -2.37) * mm});
            skLineSegment(sketch, "E14.18.7", {"start": v(-74.01, -1.12) * mm, "end": v(-74, -1.63) * mm});
            skLineSegment(sketch, "E14.18.8", {"start": v(-74, -2.14) * mm, "end": v(-74, -1.63) * mm});
            skArc(sketch, "E14.18.9", {"start": v(-74.01, -1.12) * mm, "mid": v(-74.08, -0.92) * mm, "end": v(-74.23, -0.78) * mm});
            skArc(sketch, "E14.18.10", {"start": v(-74.2, -2.48) * mm, "mid": v(-74.05, -2.34) * mm, "end": v(-74, -2.14) * mm});
            skArc(sketch, "E14.18.11", {"start": v(-78.32, 0.4) * mm, "mid": v(-78.2, 0.12) * mm, "end": v(-77.94, 0.01) * mm});
            skArc(sketch, "E14.18.12", {"start": v(-77.86, -3.39) * mm, "mid": v(-78.13, -3.51) * mm, "end": v(-78.22, -3.79) * mm});
            skArc(sketch, "E14.19.0", {"start": v(-75.88, -6.64) * mm, "mid": v(-74.87, -6.92) * mm, "end": v(-73.88, -7.25) * mm});
            skArc(sketch, "E14.19.1", {"start": v(-75.53, -9.94) * mm, "mid": v(-74.6, -9.47) * mm, "end": v(-73.7, -8.94) * mm});
            skPoint(sketch, "E14.19.2", {"position": v(-78.02, -6.81) * mm});
            skPoint(sketch, "E14.19.3", {"position": v(-73.66, -7.33) * mm});
            skLineSegment(sketch, "E14.19.4", {"start": v(-75.88, -6.64) * mm, "end": v(-77.64, -6.78) * mm});
            skLineSegment(sketch, "E14.19.5", {"start": v(-75.53, -9.94) * mm, "end": v(-77.27, -10.16) * mm});
            skPoint(sketch, "E14.19.6", {"position": v(-73.5, -8.81) * mm});
            skLineSegment(sketch, "E14.19.7", {"start": v(-73.64, -7.56) * mm, "end": v(-73.58, -8.07) * mm});
            skLineSegment(sketch, "E14.19.8", {"start": v(-73.53, -8.58) * mm, "end": v(-73.58, -8.07) * mm});
            skArc(sketch, "E14.19.9", {"start": v(-73.64, -7.56) * mm, "mid": v(-73.71, -7.37) * mm, "end": v(-73.88, -7.25) * mm});
            skArc(sketch, "E14.19.10", {"start": v(-73.7, -8.94) * mm, "mid": v(-73.57, -8.78) * mm, "end": v(-73.53, -8.58) * mm});
            skArc(sketch, "E14.19.11", {"start": v(-78.05, -6.43) * mm, "mid": v(-77.92, -6.7) * mm, "end": v(-77.64, -6.78) * mm});
            skArc(sketch, "E14.19.12", {"start": v(-77.27, -10.16) * mm, "mid": v(-77.52, -10.3) * mm, "end": v(-77.6, -10.6) * mm});
            skArc(sketch, "E14.20.0", {"start": v(-75, -13.23) * mm, "mid": v(-73.98, -13.41) * mm, "end": v(-72.97, -13.66) * mm});
            skArc(sketch, "E14.20.1", {"start": v(-74.38, -16.49) * mm, "mid": v(-73.5, -15.93) * mm, "end": v(-72.65, -15.33) * mm});
            skPoint(sketch, "E14.20.2", {"position": v(-77.13, -13.59) * mm});
            skPoint(sketch, "E14.20.3", {"position": v(-72.74, -13.72) * mm});
            skLineSegment(sketch, "E14.20.4", {"start": v(-75, -13.23) * mm, "end": v(-76.75, -13.52) * mm});
            skLineSegment(sketch, "E14.20.5", {"start": v(-74.38, -16.49) * mm, "end": v(-76.09, -16.86) * mm});
            skPoint(sketch, "E14.20.6", {"position": v(-72.46, -15.19) * mm});
            skLineSegment(sketch, "E14.20.7", {"start": v(-72.7, -13.95) * mm, "end": v(-72.6, -14.45) * mm});
            skLineSegment(sketch, "E14.20.8", {"start": v(-72.5, -14.96) * mm, "end": v(-72.6, -14.45) * mm});
            skArc(sketch, "E14.20.9", {"start": v(-72.7, -13.95) * mm, "mid": v(-72.8, -13.77) * mm, "end": v(-72.97, -13.66) * mm});
            skArc(sketch, "E14.20.10", {"start": v(-72.65, -15.33) * mm, "mid": v(-72.52, -15.16) * mm, "end": v(-72.5, -14.96) * mm});
            skArc(sketch, "E14.20.11", {"start": v(-77.2, -13.21) * mm, "mid": v(-77.04, -13.46) * mm, "end": v(-76.75, -13.52) * mm});
            skArc(sketch, "E14.20.12", {"start": v(-76.09, -16.86) * mm, "mid": v(-76.33, -17.03) * mm, "end": v(-76.38, -17.32) * mm});
            skArc(sketch, "E14.21.0", {"start": v(-73.57, -19.71) * mm, "mid": v(-72.53, -19.81) * mm, "end": v(-71.5, -19.97) * mm});
            skArc(sketch, "E14.21.1", {"start": v(-72.66, -22.9) * mm, "mid": v(-71.83, -22.28) * mm, "end": v(-71.04, -21.6) * mm});
            skPoint(sketch, "E14.21.2", {"position": v(-75.65, -20.26) * mm});
            skPoint(sketch, "E14.21.3", {"position": v(-71.27, -20) * mm});
            skLineSegment(sketch, "E14.21.4", {"start": v(-73.57, -19.71) * mm, "end": v(-75.28, -20.16) * mm});
            skLineSegment(sketch, "E14.21.5", {"start": v(-72.66, -22.9) * mm, "end": v(-74.33, -23.43) * mm});
            skPoint(sketch, "E14.21.6", {"position": v(-70.86, -21.44) * mm});
            skLineSegment(sketch, "E14.21.7", {"start": v(-71.2, -20.23) * mm, "end": v(-71.06, -20.72) * mm});
            skLineSegment(sketch, "E14.21.8", {"start": v(-70.92, -21.22) * mm, "end": v(-71.06, -20.72) * mm});
            skArc(sketch, "E14.21.9", {"start": v(-71.2, -20.23) * mm, "mid": v(-71.32, -20.06) * mm, "end": v(-71.5, -19.97) * mm});
            skArc(sketch, "E14.21.10", {"start": v(-71.04, -21.6) * mm, "mid": v(-70.92, -21.43) * mm, "end": v(-70.92, -21.22) * mm});
            skArc(sketch, "E14.21.11", {"start": v(-75.75, -19.89) * mm, "mid": v(-75.57, -20.12) * mm, "end": v(-75.28, -20.16) * mm});
            skArc(sketch, "E14.21.12", {"start": v(-74.33, -23.43) * mm, "mid": v(-74.55, -23.61) * mm, "end": v(-74.58, -23.9) * mm});
            skArc(sketch, "E14.22.0", {"start": v(-71.57, -26.05) * mm, "mid": v(-70.53, -26.06) * mm, "end": v(-69.5, -26.12) * mm});
            skArc(sketch, "E14.22.1", {"start": v(-70.39, -29.16) * mm, "mid": v(-69.61, -28.45) * mm, "end": v(-68.88, -27.71) * mm});
            skPoint(sketch, "E14.22.2", {"position": v(-73.6, -26.77) * mm});
            skPoint(sketch, "E14.22.3", {"position": v(-69.26, -26.15) * mm});
            skLineSegment(sketch, "E14.22.4", {"start": v(-71.57, -26.05) * mm, "end": v(-73.24, -26.65) * mm});
            skLineSegment(sketch, "E14.22.5", {"start": v(-70.39, -29.16) * mm, "end": v(-72, -29.81) * mm});
            skPoint(sketch, "E14.22.6", {"position": v(-68.72, -27.54) * mm});
            skLineSegment(sketch, "E14.22.7", {"start": v(-69.17, -26.36) * mm, "end": v(-68.98, -26.84) * mm});
            skLineSegment(sketch, "E14.22.8", {"start": v(-68.8, -27.32) * mm, "end": v(-68.98, -26.84) * mm});
            skArc(sketch, "E14.22.9", {"start": v(-69.17, -26.36) * mm, "mid": v(-69.3, -26.2) * mm, "end": v(-69.5, -26.12) * mm});
            skArc(sketch, "E14.22.10", {"start": v(-68.88, -27.71) * mm, "mid": v(-68.79, -27.53) * mm, "end": v(-68.8, -27.32) * mm});
            skArc(sketch, "E14.22.11", {"start": v(-73.73, -26.42) * mm, "mid": v(-73.53, -26.63) * mm, "end": v(-73.24, -26.65) * mm});
            skArc(sketch, "E14.22.12", {"start": v(-72, -29.81) * mm, "mid": v(-72.21, -30.02) * mm, "end": v(-72.21, -30.31) * mm});
            skArc(sketch, "E14.23.0", {"start": v(-69.03, -32.19) * mm, "mid": v(-68, -32.1) * mm, "end": v(-66.95, -32.08) * mm});
            skArc(sketch, "E14.23.1", {"start": v(-67.58, -35.18) * mm, "mid": v(-66.87, -34.41) * mm, "end": v(-66.2, -33.6) * mm});
            skPoint(sketch, "E14.23.2", {"position": v(-70.98, -33.09) * mm});
            skPoint(sketch, "E14.23.3", {"position": v(-66.71, -32.08) * mm});
            skLineSegment(sketch, "E14.23.4", {"start": v(-69.03, -32.19) * mm, "end": v(-70.64, -32.93) * mm});
            skLineSegment(sketch, "E14.23.5", {"start": v(-67.58, -35.18) * mm, "end": v(-69.13, -35.98) * mm});
            skPoint(sketch, "E14.23.6", {"position": v(-66.06, -33.42) * mm});
            skLineSegment(sketch, "E14.23.7", {"start": v(-66.6, -32.3) * mm, "end": v(-66.38, -32.75) * mm});
            skLineSegment(sketch, "E14.23.8", {"start": v(-66.16, -33.21) * mm, "end": v(-66.38, -32.75) * mm});
            skArc(sketch, "E14.23.9", {"start": v(-66.6, -32.3) * mm, "mid": v(-66.75, -32.14) * mm, "end": v(-66.95, -32.08) * mm});
            skArc(sketch, "E14.23.10", {"start": v(-66.2, -33.6) * mm, "mid": v(-66.13, -33.42) * mm, "end": v(-66.16, -33.21) * mm});
            skArc(sketch, "E14.23.11", {"start": v(-71.14, -32.74) * mm, "mid": v(-70.93, -32.94) * mm, "end": v(-70.64, -32.93) * mm});
            skArc(sketch, "E14.23.12", {"start": v(-69.13, -35.98) * mm, "mid": v(-69.32, -36.2) * mm, "end": v(-69.3, -36.5) * mm});
            skArc(sketch, "E14.24.0", {"start": v(-65.96, -38.08) * mm, "mid": v(-64.93, -37.9) * mm, "end": v(-63.9, -37.8) * mm});
            skArc(sketch, "E14.24.1", {"start": v(-64.25, -40.93) * mm, "mid": v(-63.62, -40.1) * mm, "end": v(-63.02, -39.25) * mm});
            skPoint(sketch, "E14.24.2", {"position": v(-67.83, -39.15) * mm});
            skPoint(sketch, "E14.24.3", {"position": v(-63.66, -37.77) * mm});
            skLineSegment(sketch, "E14.24.4", {"start": v(-65.96, -38.08) * mm, "end": v(-67.5, -38.96) * mm});
            skLineSegment(sketch, "E14.24.5", {"start": v(-64.25, -40.93) * mm, "end": v(-65.73, -41.87) * mm});
            skPoint(sketch, "E14.24.6", {"position": v(-62.9, -39.05) * mm});
            skLineSegment(sketch, "E14.24.7", {"start": v(-63.54, -37.97) * mm, "end": v(-63.27, -38.4) * mm});
            skLineSegment(sketch, "E14.24.8", {"start": v(-63.01, -38.85) * mm, "end": v(-63.27, -38.4) * mm});
            skArc(sketch, "E14.24.9", {"start": v(-63.54, -37.97) * mm, "mid": v(-63.7, -37.83) * mm, "end": v(-63.9, -37.8) * mm});
            skArc(sketch, "E14.24.10", {"start": v(-63.02, -39.25) * mm, "mid": v(-62.96, -39.05) * mm, "end": v(-63.01, -38.85) * mm});
            skArc(sketch, "E14.24.11", {"start": v(-68.02, -38.82) * mm, "mid": v(-67.79, -39) * mm, "end": v(-67.5, -38.96) * mm});
            skArc(sketch, "E14.24.12", {"start": v(-65.73, -41.87) * mm, "mid": v(-65.9, -42.1) * mm, "end": v(-65.85, -42.4) * mm});
            skArc(sketch, "E14.25.0", {"start": v(-62.4, -43.69) * mm, "mid": v(-61.38, -43.42) * mm, "end": v(-60.36, -43.22) * mm});
            skArc(sketch, "E14.25.1", {"start": v(-60.44, -46.38) * mm, "mid": v(-59.88, -45.5) * mm, "end": v(-59.36, -44.6) * mm});
            skPoint(sketch, "E14.25.2", {"position": v(-64.16, -44.91) * mm});
            skPoint(sketch, "E14.25.3", {"position": v(-60.13, -43.18) * mm});
            skLineSegment(sketch, "E14.25.4", {"start": v(-62.4, -43.69) * mm, "end": v(-63.85, -44.7) * mm});
            skLineSegment(sketch, "E14.25.5", {"start": v(-60.44, -46.38) * mm, "end": v(-61.83, -47.43) * mm});
            skPoint(sketch, "E14.25.6", {"position": v(-59.25, -44.39) * mm});
            skLineSegment(sketch, "E14.25.7", {"start": v(-59.99, -43.37) * mm, "end": v(-59.69, -43.78) * mm});
            skLineSegment(sketch, "E14.25.8", {"start": v(-59.39, -44.2) * mm, "end": v(-59.69, -43.78) * mm});
            skArc(sketch, "E14.25.9", {"start": v(-59.99, -43.37) * mm, "mid": v(-60.15, -43.24) * mm, "end": v(-60.36, -43.22) * mm});
            skArc(sketch, "E14.25.10", {"start": v(-59.36, -44.6) * mm, "mid": v(-59.32, -44.4) * mm, "end": v(-59.39, -44.2) * mm});
            skArc(sketch, "E14.25.11", {"start": v(-64.38, -44.6) * mm, "mid": v(-64.13, -44.76) * mm, "end": v(-63.85, -44.7) * mm});
            skArc(sketch, "E14.25.12", {"start": v(-61.83, -47.43) * mm, "mid": v(-61.98, -47.69) * mm, "end": v(-61.9, -47.97) * mm});
            skArc(sketch, "E14.26.0", {"start": v(-58.35, -48.96) * mm, "mid": v(-57.36, -48.6) * mm, "end": v(-56.36, -48.31) * mm});
            skArc(sketch, "E14.26.1", {"start": v(-56.17, -51.47) * mm, "mid": v(-55.68, -50.55) * mm, "end": v(-55.25, -49.6) * mm});
            skPoint(sketch, "E14.26.2", {"position": v(-60, -50.33) * mm});
            skPoint(sketch, "E14.26.3", {"position": v(-56.14, -48.26) * mm});
            skLineSegment(sketch, "E14.26.4", {"start": v(-58.35, -48.96) * mm, "end": v(-59.7, -50.09) * mm});
            skLineSegment(sketch, "E14.26.5", {"start": v(-56.17, -51.47) * mm, "end": v(-57.46, -52.64) * mm});
            skPoint(sketch, "E14.26.6", {"position": v(-55.16, -49.38) * mm});
            skLineSegment(sketch, "E14.26.7", {"start": v(-55.98, -48.43) * mm, "end": v(-55.64, -48.81) * mm});
            skLineSegment(sketch, "E14.26.8", {"start": v(-55.31, -49.2) * mm, "end": v(-55.64, -48.81) * mm});
            skArc(sketch, "E14.26.9", {"start": v(-55.98, -48.43) * mm, "mid": v(-56.16, -48.32) * mm, "end": v(-56.36, -48.31) * mm});
            skArc(sketch, "E14.26.10", {"start": v(-55.25, -49.6) * mm, "mid": v(-55.22, -49.4) * mm, "end": v(-55.31, -49.2) * mm});
            skArc(sketch, "E14.26.11", {"start": v(-60.25, -50.04) * mm, "mid": v(-59.99, -50.17) * mm, "end": v(-59.7, -50.09) * mm});
            skArc(sketch, "E14.26.12", {"start": v(-57.46, -52.64) * mm, "mid": v(-57.59, -52.9) * mm, "end": v(-57.49, -53.18) * mm});
            skArc(sketch, "E14.27.0", {"start": v(-53.86, -53.86) * mm, "mid": v(-52.91, -53.42) * mm, "end": v(-51.94, -53.04) * mm});
            skArc(sketch, "E14.27.1", {"start": v(-51.47, -56.17) * mm, "mid": v(-51.07, -55.2) * mm, "end": v(-50.72, -54.23) * mm});
            skPoint(sketch, "E14.27.2", {"position": v(-55.39, -55.37) * mm});
            skPoint(sketch, "E14.27.3", {"position": v(-51.72, -52.96) * mm});
            skLineSegment(sketch, "E14.27.4", {"start": v(-53.86, -53.86) * mm, "end": v(-55.12, -55.1) * mm});
            skLineSegment(sketch, "E14.27.5", {"start": v(-51.47, -56.17) * mm, "end": v(-52.66, -57.45) * mm});
            skPoint(sketch, "E14.27.6", {"position": v(-50.65, -54) * mm});
            skLineSegment(sketch, "E14.27.7", {"start": v(-51.55, -53.12) * mm, "end": v(-51.18, -53.48) * mm});
            skLineSegment(sketch, "E14.27.8", {"start": v(-50.81, -53.84) * mm, "end": v(-51.18, -53.48) * mm});
            skArc(sketch, "E14.27.9", {"start": v(-51.55, -53.12) * mm, "mid": v(-51.73, -53.03) * mm, "end": v(-51.94, -53.04) * mm});
            skArc(sketch, "E14.27.10", {"start": v(-50.72, -54.23) * mm, "mid": v(-50.7, -54.02) * mm, "end": v(-50.81, -53.84) * mm});
            skArc(sketch, "E14.27.11", {"start": v(-55.66, -55.1) * mm, "mid": v(-55.39, -55.21) * mm, "end": v(-55.12, -55.1) * mm});
            skArc(sketch, "E14.27.12", {"start": v(-52.66, -57.45) * mm, "mid": v(-52.76, -57.73) * mm, "end": v(-52.63, -58) * mm});
            skArc(sketch, "E14.28.0", {"start": v(-48.96, -58.35) * mm, "mid": v(-48.05, -57.83) * mm, "end": v(-47.12, -57.37) * mm});
            skArc(sketch, "E14.28.1", {"start": v(-46.38, -60.44) * mm, "mid": v(-46.06, -59.45) * mm, "end": v(-45.8, -58.44) * mm});
            skPoint(sketch, "E14.28.2", {"position": v(-50.35, -59.99) * mm});
            skPoint(sketch, "E14.28.3", {"position": v(-46.9, -57.27) * mm});
            skLineSegment(sketch, "E14.28.4", {"start": v(-48.96, -58.35) * mm, "end": v(-50.1, -59.7) * mm});
            skLineSegment(sketch, "E14.28.5", {"start": v(-46.38, -60.44) * mm, "end": v(-47.45, -61.82) * mm});
            skPoint(sketch, "E14.28.6", {"position": v(-45.75, -58.2) * mm});
            skLineSegment(sketch, "E14.28.7", {"start": v(-46.72, -57.42) * mm, "end": v(-46.32, -57.73) * mm});
            skLineSegment(sketch, "E14.28.8", {"start": v(-45.93, -58.06) * mm, "end": v(-46.32, -57.73) * mm});
            skArc(sketch, "E14.28.9", {"start": v(-46.72, -57.42) * mm, "mid": v(-46.91, -57.34) * mm, "end": v(-47.12, -57.37) * mm});
            skArc(sketch, "E14.28.10", {"start": v(-45.8, -58.44) * mm, "mid": v(-45.8, -58.23) * mm, "end": v(-45.93, -58.06) * mm});
            skArc(sketch, "E14.28.11", {"start": v(-50.64, -59.74) * mm, "mid": v(-50.36, -59.83) * mm, "end": v(-50.1, -59.7) * mm});
            skArc(sketch, "E14.28.12", {"start": v(-47.45, -61.82) * mm, "mid": v(-47.53, -62.1) * mm, "end": v(-47.38, -62.36) * mm});
            skArc(sketch, "E14.29.0", {"start": v(-43.69, -62.4) * mm, "mid": v(-42.83, -61.8) * mm, "end": v(-41.94, -61.26) * mm});
            skArc(sketch, "E14.29.1", {"start": v(-40.93, -64.25) * mm, "mid": v(-40.7, -63.24) * mm, "end": v(-40.53, -62.2) * mm});
            skPoint(sketch, "E14.29.2", {"position": v(-44.93, -64.15) * mm});
            skPoint(sketch, "E14.29.3", {"position": v(-41.73, -61.14) * mm});
            skLineSegment(sketch, "E14.29.4", {"start": v(-43.69, -62.4) * mm, "end": v(-44.71, -63.84) * mm});
            skLineSegment(sketch, "E14.29.5", {"start": v(-40.93, -64.25) * mm, "end": v(-41.88, -65.72) * mm});
            skPoint(sketch, "E14.29.6", {"position": v(-40.5, -61.98) * mm});
            skLineSegment(sketch, "E14.29.7", {"start": v(-41.54, -61.27) * mm, "end": v(-41.11, -61.55) * mm});
            skLineSegment(sketch, "E14.29.8", {"start": v(-40.7, -61.84) * mm, "end": v(-41.11, -61.55) * mm});
            skArc(sketch, "E14.29.9", {"start": v(-41.54, -61.27) * mm, "mid": v(-41.74, -61.2) * mm, "end": v(-41.94, -61.26) * mm});
            skArc(sketch, "E14.29.10", {"start": v(-40.53, -62.2) * mm, "mid": v(-40.56, -62) * mm, "end": v(-40.7, -61.84) * mm});
            skArc(sketch, "E14.29.11", {"start": v(-45.24, -63.93) * mm, "mid": v(-44.96, -64) * mm, "end": v(-44.71, -63.84) * mm});
            skArc(sketch, "E14.29.12", {"start": v(-41.88, -65.72) * mm, "mid": v(-41.93, -66.01) * mm, "end": v(-41.76, -66.25) * mm});
            skArc(sketch, "E14.30.0", {"start": v(-38.08, -65.96) * mm, "mid": v(-37.28, -65.3) * mm, "end": v(-36.44, -64.68) * mm});
            skArc(sketch, "E14.30.1", {"start": v(-35.18, -67.58) * mm, "mid": v(-35.04, -66.54) * mm, "end": v(-34.95, -65.5) * mm});
            skPoint(sketch, "E14.30.2", {"position": v(-39.17, -67.82) * mm});
            skPoint(sketch, "E14.30.3", {"position": v(-36.25, -64.54) * mm});
            skLineSegment(sketch, "E14.30.4", {"start": v(-38.08, -65.96) * mm, "end": v(-38.98, -67.49) * mm});
            skLineSegment(sketch, "E14.30.5", {"start": v(-35.18, -67.58) * mm, "end": v(-36, -69.12) * mm});
            skPoint(sketch, "E14.30.6", {"position": v(-34.94, -65.27) * mm});
            skLineSegment(sketch, "E14.30.7", {"start": v(-36.04, -64.66) * mm, "end": v(-35.6, -64.9) * mm});
            skLineSegment(sketch, "E14.30.8", {"start": v(-35.15, -65.15) * mm, "end": v(-35.6, -64.9) * mm});
            skArc(sketch, "E14.30.9", {"start": v(-36.04, -64.66) * mm, "mid": v(-36.24, -64.61) * mm, "end": v(-36.44, -64.68) * mm});
            skArc(sketch, "E14.30.10", {"start": v(-34.95, -65.5) * mm, "mid": v(-35, -65.3) * mm, "end": v(-35.15, -65.15) * mm});
            skArc(sketch, "E14.30.11", {"start": v(-39.5, -67.63) * mm, "mid": v(-39.2, -67.67) * mm, "end": v(-38.98, -67.49) * mm});
            skArc(sketch, "E14.30.12", {"start": v(-36, -69.12) * mm, "mid": v(-36.02, -69.41) * mm, "end": v(-35.83, -69.64) * mm});
            skArc(sketch, "E14.31.0", {"start": v(-32.19, -69.03) * mm, "mid": v(-31.45, -68.3) * mm, "end": v(-30.67, -67.6) * mm});
            skArc(sketch, "E14.31.1", {"start": v(-29.15, -70.39) * mm, "mid": v(-29.1, -69.34) * mm, "end": v(-29.11, -68.3) * mm});
            skPoint(sketch, "E14.31.2", {"position": v(-33.1, -70.97) * mm});
            skPoint(sketch, "E14.31.3", {"position": v(-30.48, -67.46) * mm});
            skLineSegment(sketch, "E14.31.4", {"start": v(-32.19, -69.03) * mm, "end": v(-32.95, -70.63) * mm});
            skLineSegment(sketch, "E14.31.5", {"start": v(-29.15, -70.39) * mm, "end": v(-29.83, -72) * mm});
            skPoint(sketch, "E14.31.6", {"position": v(-29.12, -68.07) * mm});
            skLineSegment(sketch, "E14.31.7", {"start": v(-30.27, -67.55) * mm, "end": v(-29.8, -67.76) * mm});
            skLineSegment(sketch, "E14.31.8", {"start": v(-29.33, -67.97) * mm, "end": v(-29.8, -67.76) * mm});
            skArc(sketch, "E14.31.9", {"start": v(-30.27, -67.55) * mm, "mid": v(-30.48, -67.52) * mm, "end": v(-30.67, -67.6) * mm});
            skArc(sketch, "E14.31.10", {"start": v(-29.11, -68.3) * mm, "mid": v(-29.18, -68.1) * mm, "end": v(-29.33, -67.97) * mm});
            skArc(sketch, "E14.31.11", {"start": v(-33.45, -70.81) * mm, "mid": v(-33.16, -70.83) * mm, "end": v(-32.95, -70.63) * mm});
            skArc(sketch, "E14.31.12", {"start": v(-29.83, -72) * mm, "mid": v(-29.83, -72.3) * mm, "end": v(-29.63, -72.5) * mm});
            skArc(sketch, "E14.32.0", {"start": v(-26.05, -71.57) * mm, "mid": v(-25.37, -70.78) * mm, "end": v(-24.66, -70.02) * mm});
            skArc(sketch, "E14.32.1", {"start": v(-22.9, -72.66) * mm, "mid": v(-22.95, -71.62) * mm, "end": v(-23.05, -70.58) * mm});
            skPoint(sketch, "E14.32.2", {"position": v(-26.8, -73.59) * mm});
            skPoint(sketch, "E14.32.3", {"position": v(-24.49, -69.86) * mm});
            skLineSegment(sketch, "E14.32.4", {"start": v(-26.05, -71.57) * mm, "end": v(-26.67, -73.23) * mm});
            skLineSegment(sketch, "E14.32.5", {"start": v(-22.9, -72.66) * mm, "end": v(-23.44, -74.32) * mm});
            skPoint(sketch, "E14.32.6", {"position": v(-23.08, -70.35) * mm});
            skLineSegment(sketch, "E14.32.7", {"start": v(-24.27, -69.93) * mm, "end": v(-23.78, -70.1) * mm});
            skLineSegment(sketch, "E14.32.8", {"start": v(-23.3, -70.27) * mm, "end": v(-23.78, -70.1) * mm});
            skArc(sketch, "E14.32.9", {"start": v(-24.27, -69.93) * mm, "mid": v(-24.47, -69.92) * mm, "end": v(-24.66, -70.02) * mm});
            skArc(sketch, "E14.32.10", {"start": v(-23.05, -70.58) * mm, "mid": v(-23.13, -70.39) * mm, "end": v(-23.3, -70.27) * mm});
            skArc(sketch, "E14.32.11", {"start": v(-27.16, -73.46) * mm, "mid": v(-26.86, -73.45) * mm, "end": v(-26.67, -73.23) * mm});
            skArc(sketch, "E14.32.12", {"start": v(-23.44, -74.32) * mm, "mid": v(-23.42, -74.62) * mm, "end": v(-23.2, -74.8) * mm});
            skArc(sketch, "E14.33.0", {"start": v(-19.71, -73.57) * mm, "mid": v(-19.1, -72.72) * mm, "end": v(-18.46, -71.9) * mm});
            skArc(sketch, "E14.33.1", {"start": v(-16.49, -74.38) * mm, "mid": v(-16.62, -73.35) * mm, "end": v(-16.8, -72.32) * mm});
            skPoint(sketch, "E14.33.2", {"position": v(-20.28, -75.64) * mm});
            skPoint(sketch, "E14.33.3", {"position": v(-18.3, -71.73) * mm});
            skLineSegment(sketch, "E14.33.4", {"start": v(-19.71, -73.57) * mm, "end": v(-20.18, -75.28) * mm});
            skLineSegment(sketch, "E14.33.5", {"start": v(-16.49, -74.38) * mm, "end": v(-16.88, -76.08) * mm});
            skPoint(sketch, "E14.33.6", {"position": v(-16.86, -72.09) * mm});
            skLineSegment(sketch, "E14.33.7", {"start": v(-18.08, -71.78) * mm, "end": v(-17.58, -71.9) * mm});
            skLineSegment(sketch, "E14.33.8", {"start": v(-17.09, -72.03) * mm, "end": v(-17.58, -71.9) * mm});
            skArc(sketch, "E14.33.9", {"start": v(-18.08, -71.78) * mm, "mid": v(-18.29, -71.79) * mm, "end": v(-18.46, -71.9) * mm});
            skArc(sketch, "E14.33.10", {"start": v(-16.8, -72.32) * mm, "mid": v(-16.9, -72.14) * mm, "end": v(-17.09, -72.03) * mm});
            skArc(sketch, "E14.33.11", {"start": v(-20.65, -75.55) * mm, "mid": v(-20.36, -75.5) * mm, "end": v(-20.18, -75.28) * mm});
            skArc(sketch, "E14.33.12", {"start": v(-16.88, -76.08) * mm, "mid": v(-16.83, -76.37) * mm, "end": v(-16.59, -76.54) * mm});
            skArc(sketch, "E14.34.0", {"start": v(-13.23, -75) * mm, "mid": v(-12.7, -74.11) * mm, "end": v(-12.12, -73.24) * mm});
            skArc(sketch, "E14.34.1", {"start": v(-9.94, -75.53) * mm, "mid": v(-10.17, -74.51) * mm, "end": v(-10.44, -73.5) * mm});
            skPoint(sketch, "E14.34.2", {"position": v(-13.61, -77.12) * mm});
            skPoint(sketch, "E14.34.3", {"position": v(-11.99, -73.05) * mm});
            skLineSegment(sketch, "E14.34.4", {"start": v(-13.23, -75) * mm, "end": v(-13.54, -76.75) * mm});
            skLineSegment(sketch, "E14.34.5", {"start": v(-9.94, -75.53) * mm, "end": v(-10.18, -77.26) * mm});
            skPoint(sketch, "E14.34.6", {"position": v(-10.51, -73.28) * mm});
            skLineSegment(sketch, "E14.34.7", {"start": v(-11.75, -73.08) * mm, "end": v(-11.25, -73.16) * mm});
            skLineSegment(sketch, "E14.34.8", {"start": v(-10.74, -73.25) * mm, "end": v(-11.25, -73.16) * mm});
            skArc(sketch, "E14.34.9", {"start": v(-11.75, -73.08) * mm, "mid": v(-11.96, -73.11) * mm, "end": v(-12.12, -73.24) * mm});
            skArc(sketch, "E14.34.10", {"start": v(-10.44, -73.5) * mm, "mid": v(-10.56, -73.33) * mm, "end": v(-10.74, -73.25) * mm});
            skArc(sketch, "E14.34.11", {"start": v(-13.99, -77.06) * mm, "mid": v(-13.7, -77) * mm, "end": v(-13.54, -76.75) * mm});
            skArc(sketch, "E14.34.12", {"start": v(-10.18, -77.26) * mm, "mid": v(-10.1, -77.55) * mm, "end": v(-9.85, -77.7) * mm});
            skArc(sketch, "E14.35.0", {"start": v(-6.64, -75.88) * mm, "mid": v(-6.2, -74.93) * mm, "end": v(-5.7, -74.02) * mm});
            skArc(sketch, "E14.35.1", {"start": v(-3.32, -76.11) * mm, "mid": v(-3.63, -75.12) * mm, "end": v(-4, -74.14) * mm});
            skPoint(sketch, "E14.35.2", {"position": v(-6.84, -78.02) * mm});
            skPoint(sketch, "E14.35.3", {"position": v(-5.57, -73.82) * mm});
            skLineSegment(sketch, "E14.35.4", {"start": v(-6.64, -75.88) * mm, "end": v(-6.8, -77.64) * mm});
            skLineSegment(sketch, "E14.35.5", {"start": v(-3.32, -76.11) * mm, "end": v(-3.4, -77.86) * mm});
            skPoint(sketch, "E14.35.6", {"position": v(-4.09, -73.92) * mm});
            skLineSegment(sketch, "E14.35.7", {"start": v(-5.34, -73.83) * mm, "end": v(-4.83, -73.86) * mm});
            skLineSegment(sketch, "E14.35.8", {"start": v(-4.32, -73.9) * mm, "end": v(-4.83, -73.86) * mm});
            skArc(sketch, "E14.35.9", {"start": v(-5.34, -73.83) * mm, "mid": v(-5.54, -73.87) * mm, "end": v(-5.7, -74.02) * mm});
            skArc(sketch, "E14.35.10", {"start": v(-4, -74.14) * mm, "mid": v(-4.12, -73.98) * mm, "end": v(-4.32, -73.9) * mm});
            skArc(sketch, "E14.35.11", {"start": v(-7.22, -77.98) * mm, "mid": v(-6.94, -77.9) * mm, "end": v(-6.8, -77.64) * mm});
            skArc(sketch, "E14.35.12", {"start": v(-3.4, -77.86) * mm, "mid": v(-3.3, -78.13) * mm, "end": v(-3.04, -78.26) * mm});
            skArc(sketch, "E14.36.0", {"start": v(0, -76.17) * mm, "mid": v(0.36, -75.19) * mm, "end": v(0.78, -74.23) * mm});
            skArc(sketch, "E14.36.1", {"start": v(3.32, -76.11) * mm, "mid": v(2.93, -75.15) * mm, "end": v(2.48, -74.2) * mm});
            skPoint(sketch, "E14.36.2", {"position": v(-0.01, -78.32) * mm});
            skPoint(sketch, "E14.36.3", {"position": v(0.88, -74.02) * mm});
            skLineSegment(sketch, "E14.36.4", {"start": v(0, -76.17) * mm, "end": v(-0.01, -77.94) * mm});
            skLineSegment(sketch, "E14.36.5", {"start": v(3.32, -76.11) * mm, "end": v(3.39, -77.86) * mm});
            skPoint(sketch, "E14.36.6", {"position": v(2.37, -74) * mm});
            skLineSegment(sketch, "E14.36.7", {"start": v(1.12, -74.01) * mm, "end": v(1.63, -74) * mm});
            skLineSegment(sketch, "E14.36.8", {"start": v(2.14, -74) * mm, "end": v(1.63, -74) * mm});
            skArc(sketch, "E14.36.9", {"start": v(1.12, -74.01) * mm, "mid": v(0.92, -74.08) * mm, "end": v(0.78, -74.23) * mm});
            skArc(sketch, "E14.36.10", {"start": v(2.48, -74.2) * mm, "mid": v(2.34, -74.05) * mm, "end": v(2.14, -74) * mm});
            skArc(sketch, "E14.36.11", {"start": v(-0.4, -78.32) * mm, "mid": v(-0.12, -78.2) * mm, "end": v(-0.01, -77.94) * mm});
            skArc(sketch, "E14.36.12", {"start": v(3.39, -77.86) * mm, "mid": v(3.51, -78.13) * mm, "end": v(3.79, -78.22) * mm});
            skArc(sketch, "E14.37.0", {"start": v(6.64, -75.88) * mm, "mid": v(6.92, -74.87) * mm, "end": v(7.25, -73.88) * mm});
            skArc(sketch, "E14.37.1", {"start": v(9.94, -75.53) * mm, "mid": v(9.47, -74.6) * mm, "end": v(8.94, -73.7) * mm});
            skPoint(sketch, "E14.37.2", {"position": v(6.81, -78.02) * mm});
            skPoint(sketch, "E14.37.3", {"position": v(7.33, -73.66) * mm});
            skLineSegment(sketch, "E14.37.4", {"start": v(6.64, -75.88) * mm, "end": v(6.78, -77.64) * mm});
            skLineSegment(sketch, "E14.37.5", {"start": v(9.94, -75.53) * mm, "end": v(10.16, -77.27) * mm});
            skPoint(sketch, "E14.37.6", {"position": v(8.81, -73.5) * mm});
            skLineSegment(sketch, "E14.37.7", {"start": v(7.56, -73.64) * mm, "end": v(8.07, -73.58) * mm});
            skLineSegment(sketch, "E14.37.8", {"start": v(8.58, -73.53) * mm, "end": v(8.07, -73.58) * mm});
            skArc(sketch, "E14.37.9", {"start": v(7.56, -73.64) * mm, "mid": v(7.37, -73.71) * mm, "end": v(7.25, -73.88) * mm});
            skArc(sketch, "E14.37.10", {"start": v(8.94, -73.7) * mm, "mid": v(8.78, -73.57) * mm, "end": v(8.58, -73.53) * mm});
            skArc(sketch, "E14.37.11", {"start": v(6.43, -78.05) * mm, "mid": v(6.7, -77.92) * mm, "end": v(6.78, -77.64) * mm});
            skArc(sketch, "E14.37.12", {"start": v(10.16, -77.27) * mm, "mid": v(10.3, -77.52) * mm, "end": v(10.6, -77.6) * mm});
            skArc(sketch, "E14.38.0", {"start": v(13.23, -75) * mm, "mid": v(13.41, -73.98) * mm, "end": v(13.66, -72.97) * mm});
            skArc(sketch, "E14.38.1", {"start": v(16.49, -74.38) * mm, "mid": v(15.93, -73.5) * mm, "end": v(15.33, -72.65) * mm});
            skPoint(sketch, "E14.38.2", {"position": v(13.59, -77.13) * mm});
            skPoint(sketch, "E14.38.3", {"position": v(13.72, -72.74) * mm});
            skLineSegment(sketch, "E14.38.4", {"start": v(13.23, -75) * mm, "end": v(13.52, -76.75) * mm});
            skLineSegment(sketch, "E14.38.5", {"start": v(16.49, -74.38) * mm, "end": v(16.86, -76.09) * mm});
            skPoint(sketch, "E14.38.6", {"position": v(15.19, -72.46) * mm});
            skLineSegment(sketch, "E14.38.7", {"start": v(13.95, -72.7) * mm, "end": v(14.45, -72.6) * mm});
            skLineSegment(sketch, "E14.38.8", {"start": v(14.96, -72.5) * mm, "end": v(14.45, -72.6) * mm});
            skArc(sketch, "E14.38.9", {"start": v(13.95, -72.7) * mm, "mid": v(13.77, -72.8) * mm, "end": v(13.66, -72.97) * mm});
            skArc(sketch, "E14.38.10", {"start": v(15.33, -72.65) * mm, "mid": v(15.16, -72.52) * mm, "end": v(14.96, -72.5) * mm});
            skArc(sketch, "E14.38.11", {"start": v(13.21, -77.2) * mm, "mid": v(13.46, -77.04) * mm, "end": v(13.52, -76.75) * mm});
            skArc(sketch, "E14.38.12", {"start": v(16.86, -76.09) * mm, "mid": v(17.03, -76.33) * mm, "end": v(17.32, -76.38) * mm});
            skArc(sketch, "E14.39.0", {"start": v(19.71, -73.57) * mm, "mid": v(19.81, -72.53) * mm, "end": v(19.97, -71.5) * mm});
            skArc(sketch, "E14.39.1", {"start": v(22.9, -72.66) * mm, "mid": v(22.28, -71.83) * mm, "end": v(21.6, -71.04) * mm});
            skPoint(sketch, "E14.39.2", {"position": v(20.26, -75.65) * mm});
            skPoint(sketch, "E14.39.3", {"position": v(20, -71.27) * mm});
            skLineSegment(sketch, "E14.39.4", {"start": v(19.71, -73.57) * mm, "end": v(20.16, -75.28) * mm});
            skLineSegment(sketch, "E14.39.5", {"start": v(22.9, -72.66) * mm, "end": v(23.43, -74.33) * mm});
            skPoint(sketch, "E14.39.6", {"position": v(21.44, -70.86) * mm});
            skLineSegment(sketch, "E14.39.7", {"start": v(20.23, -71.2) * mm, "end": v(20.72, -71.06) * mm});
            skLineSegment(sketch, "E14.39.8", {"start": v(21.22, -70.92) * mm, "end": v(20.72, -71.06) * mm});
            skArc(sketch, "E14.39.9", {"start": v(20.23, -71.2) * mm, "mid": v(20.06, -71.32) * mm, "end": v(19.97, -71.5) * mm});
            skArc(sketch, "E14.39.10", {"start": v(21.6, -71.04) * mm, "mid": v(21.43, -70.92) * mm, "end": v(21.22, -70.92) * mm});
            skArc(sketch, "E14.39.11", {"start": v(19.89, -75.75) * mm, "mid": v(20.12, -75.57) * mm, "end": v(20.16, -75.28) * mm});
            skArc(sketch, "E14.39.12", {"start": v(23.43, -74.33) * mm, "mid": v(23.61, -74.55) * mm, "end": v(23.9, -74.58) * mm});
            skArc(sketch, "E14.40.0", {"start": v(26.05, -71.57) * mm, "mid": v(26.06, -70.53) * mm, "end": v(26.12, -69.5) * mm});
            skArc(sketch, "E14.40.1", {"start": v(29.16, -70.39) * mm, "mid": v(28.45, -69.61) * mm, "end": v(27.71, -68.88) * mm});
            skPoint(sketch, "E14.40.2", {"position": v(26.77, -73.6) * mm});
            skPoint(sketch, "E14.40.3", {"position": v(26.15, -69.26) * mm});
            skLineSegment(sketch, "E14.40.4", {"start": v(26.05, -71.57) * mm, "end": v(26.65, -73.24) * mm});
            skLineSegment(sketch, "E14.40.5", {"start": v(29.16, -70.39) * mm, "end": v(29.81, -72) * mm});
            skPoint(sketch, "E14.40.6", {"position": v(27.54, -68.72) * mm});
            skLineSegment(sketch, "E14.40.7", {"start": v(26.36, -69.17) * mm, "end": v(26.84, -68.98) * mm});
            skLineSegment(sketch, "E14.40.8", {"start": v(27.32, -68.8) * mm, "end": v(26.84, -68.98) * mm});
            skArc(sketch, "E14.40.9", {"start": v(26.36, -69.17) * mm, "mid": v(26.2, -69.3) * mm, "end": v(26.12, -69.5) * mm});
            skArc(sketch, "E14.40.10", {"start": v(27.71, -68.88) * mm, "mid": v(27.53, -68.79) * mm, "end": v(27.32, -68.8) * mm});
            skArc(sketch, "E14.40.11", {"start": v(26.42, -73.73) * mm, "mid": v(26.63, -73.53) * mm, "end": v(26.65, -73.24) * mm});
            skArc(sketch, "E14.40.12", {"start": v(29.81, -72) * mm, "mid": v(30.02, -72.21) * mm, "end": v(30.31, -72.21) * mm});
            skArc(sketch, "E14.41.0", {"start": v(32.19, -69.03) * mm, "mid": v(32.1, -68) * mm, "end": v(32.08, -66.95) * mm});
            skArc(sketch, "E14.41.1", {"start": v(35.18, -67.58) * mm, "mid": v(34.41, -66.87) * mm, "end": v(33.6, -66.2) * mm});
            skPoint(sketch, "E14.41.2", {"position": v(33.09, -70.98) * mm});
            skPoint(sketch, "E14.41.3", {"position": v(32.08, -66.71) * mm});
            skLineSegment(sketch, "E14.41.4", {"start": v(32.19, -69.03) * mm, "end": v(32.93, -70.64) * mm});
            skLineSegment(sketch, "E14.41.5", {"start": v(35.18, -67.58) * mm, "end": v(35.98, -69.13) * mm});
            skPoint(sketch, "E14.41.6", {"position": v(33.42, -66.06) * mm});
            skLineSegment(sketch, "E14.41.7", {"start": v(32.3, -66.6) * mm, "end": v(32.75, -66.38) * mm});
            skLineSegment(sketch, "E14.41.8", {"start": v(33.21, -66.16) * mm, "end": v(32.75, -66.38) * mm});
            skArc(sketch, "E14.41.9", {"start": v(32.3, -66.6) * mm, "mid": v(32.14, -66.75) * mm, "end": v(32.08, -66.95) * mm});
            skArc(sketch, "E14.41.10", {"start": v(33.6, -66.2) * mm, "mid": v(33.42, -66.13) * mm, "end": v(33.21, -66.16) * mm});
            skArc(sketch, "E14.41.11", {"start": v(32.74, -71.14) * mm, "mid": v(32.94, -70.93) * mm, "end": v(32.93, -70.64) * mm});
            skArc(sketch, "E14.41.12", {"start": v(35.98, -69.13) * mm, "mid": v(36.2, -69.32) * mm, "end": v(36.5, -69.3) * mm});
            skArc(sketch, "E14.42.0", {"start": v(38.08, -65.96) * mm, "mid": v(37.9, -64.93) * mm, "end": v(37.8, -63.9) * mm});
            skArc(sketch, "E14.42.1", {"start": v(40.93, -64.25) * mm, "mid": v(40.1, -63.62) * mm, "end": v(39.25, -63.02) * mm});
            skPoint(sketch, "E14.42.2", {"position": v(39.15, -67.83) * mm});
            skPoint(sketch, "E14.42.3", {"position": v(37.77, -63.66) * mm});
            skLineSegment(sketch, "E14.42.4", {"start": v(38.08, -65.96) * mm, "end": v(38.96, -67.5) * mm});
            skLineSegment(sketch, "E14.42.5", {"start": v(40.93, -64.25) * mm, "end": v(41.87, -65.73) * mm});
            skPoint(sketch, "E14.42.6", {"position": v(39.05, -62.9) * mm});
            skLineSegment(sketch, "E14.42.7", {"start": v(37.97, -63.54) * mm, "end": v(38.4, -63.27) * mm});
            skLineSegment(sketch, "E14.42.8", {"start": v(38.85, -63.01) * mm, "end": v(38.4, -63.27) * mm});
            skArc(sketch, "E14.42.9", {"start": v(37.97, -63.54) * mm, "mid": v(37.83, -63.7) * mm, "end": v(37.8, -63.9) * mm});
            skArc(sketch, "E14.42.10", {"start": v(39.25, -63.02) * mm, "mid": v(39.05, -62.96) * mm, "end": v(38.85, -63.01) * mm});
            skArc(sketch, "E14.42.11", {"start": v(38.82, -68.02) * mm, "mid": v(39, -67.79) * mm, "end": v(38.96, -67.5) * mm});
            skArc(sketch, "E14.42.12", {"start": v(41.87, -65.73) * mm, "mid": v(42.1, -65.9) * mm, "end": v(42.4, -65.85) * mm});
            skArc(sketch, "E14.43.0", {"start": v(43.69, -62.4) * mm, "mid": v(43.42, -61.38) * mm, "end": v(43.22, -60.36) * mm});
            skArc(sketch, "E14.43.1", {"start": v(46.38, -60.44) * mm, "mid": v(45.5, -59.88) * mm, "end": v(44.6, -59.36) * mm});
            skPoint(sketch, "E14.43.2", {"position": v(44.91, -64.16) * mm});
            skPoint(sketch, "E14.43.3", {"position": v(43.18, -60.13) * mm});
            skLineSegment(sketch, "E14.43.4", {"start": v(43.69, -62.4) * mm, "end": v(44.7, -63.85) * mm});
            skLineSegment(sketch, "E14.43.5", {"start": v(46.38, -60.44) * mm, "end": v(47.43, -61.83) * mm});
            skPoint(sketch, "E14.43.6", {"position": v(44.39, -59.25) * mm});
            skLineSegment(sketch, "E14.43.7", {"start": v(43.37, -59.99) * mm, "end": v(43.78, -59.69) * mm});
            skLineSegment(sketch, "E14.43.8", {"start": v(44.2, -59.39) * mm, "end": v(43.78, -59.69) * mm});
            skArc(sketch, "E14.43.9", {"start": v(43.37, -59.99) * mm, "mid": v(43.24, -60.15) * mm, "end": v(43.22, -60.36) * mm});
            skArc(sketch, "E14.43.10", {"start": v(44.6, -59.36) * mm, "mid": v(44.4, -59.32) * mm, "end": v(44.2, -59.39) * mm});
            skArc(sketch, "E14.43.11", {"start": v(44.6, -64.38) * mm, "mid": v(44.76, -64.13) * mm, "end": v(44.7, -63.85) * mm});
            skArc(sketch, "E14.43.12", {"start": v(47.43, -61.83) * mm, "mid": v(47.69, -61.98) * mm, "end": v(47.97, -61.9) * mm});
            skArc(sketch, "E14.44.0", {"start": v(48.96, -58.35) * mm, "mid": v(48.6, -57.36) * mm, "end": v(48.31, -56.36) * mm});
            skArc(sketch, "E14.44.1", {"start": v(51.47, -56.17) * mm, "mid": v(50.55, -55.68) * mm, "end": v(49.6, -55.25) * mm});
            skPoint(sketch, "E14.44.2", {"position": v(50.33, -60) * mm});
            skPoint(sketch, "E14.44.3", {"position": v(48.26, -56.14) * mm});
            skLineSegment(sketch, "E14.44.4", {"start": v(48.96, -58.35) * mm, "end": v(50.09, -59.7) * mm});
            skLineSegment(sketch, "E14.44.5", {"start": v(51.47, -56.17) * mm, "end": v(52.64, -57.46) * mm});
            skPoint(sketch, "E14.44.6", {"position": v(49.38, -55.16) * mm});
            skLineSegment(sketch, "E14.44.7", {"start": v(48.43, -55.98) * mm, "end": v(48.81, -55.64) * mm});
            skLineSegment(sketch, "E14.44.8", {"start": v(49.2, -55.31) * mm, "end": v(48.81, -55.64) * mm});
            skArc(sketch, "E14.44.9", {"start": v(48.43, -55.98) * mm, "mid": v(48.32, -56.16) * mm, "end": v(48.31, -56.36) * mm});
            skArc(sketch, "E14.44.10", {"start": v(49.6, -55.25) * mm, "mid": v(49.4, -55.22) * mm, "end": v(49.2, -55.31) * mm});
            skArc(sketch, "E14.44.11", {"start": v(50.04, -60.25) * mm, "mid": v(50.17, -59.99) * mm, "end": v(50.09, -59.7) * mm});
            skArc(sketch, "E14.44.12", {"start": v(52.64, -57.46) * mm, "mid": v(52.9, -57.59) * mm, "end": v(53.18, -57.49) * mm});
            skArc(sketch, "E14.45.0", {"start": v(53.86, -53.86) * mm, "mid": v(53.42, -52.91) * mm, "end": v(53.04, -51.94) * mm});
            skArc(sketch, "E14.45.1", {"start": v(56.17, -51.47) * mm, "mid": v(55.2, -51.07) * mm, "end": v(54.23, -50.72) * mm});
            skPoint(sketch, "E14.45.2", {"position": v(55.37, -55.39) * mm});
            skPoint(sketch, "E14.45.3", {"position": v(52.96, -51.72) * mm});
            skLineSegment(sketch, "E14.45.4", {"start": v(53.86, -53.86) * mm, "end": v(55.1, -55.12) * mm});
            skLineSegment(sketch, "E14.45.5", {"start": v(56.17, -51.47) * mm, "end": v(57.45, -52.66) * mm});
            skPoint(sketch, "E14.45.6", {"position": v(54, -50.65) * mm});
            skLineSegment(sketch, "E14.45.7", {"start": v(53.12, -51.55) * mm, "end": v(53.48, -51.18) * mm});
            skLineSegment(sketch, "E14.45.8", {"start": v(53.84, -50.81) * mm, "end": v(53.48, -51.18) * mm});
            skArc(sketch, "E14.45.9", {"start": v(53.12, -51.55) * mm, "mid": v(53.03, -51.73) * mm, "end": v(53.04, -51.94) * mm});
            skArc(sketch, "E14.45.10", {"start": v(54.23, -50.72) * mm, "mid": v(54.02, -50.7) * mm, "end": v(53.84, -50.81) * mm});
            skArc(sketch, "E14.45.11", {"start": v(55.1, -55.66) * mm, "mid": v(55.21, -55.39) * mm, "end": v(55.1, -55.12) * mm});
            skArc(sketch, "E14.45.12", {"start": v(57.45, -52.66) * mm, "mid": v(57.73, -52.76) * mm, "end": v(58, -52.63) * mm});
            skArc(sketch, "E14.46.0", {"start": v(58.35, -48.96) * mm, "mid": v(57.83, -48.05) * mm, "end": v(57.37, -47.12) * mm});
            skArc(sketch, "E14.46.1", {"start": v(60.44, -46.38) * mm, "mid": v(59.45, -46.06) * mm, "end": v(58.44, -45.8) * mm});
            skPoint(sketch, "E14.46.2", {"position": v(59.99, -50.35) * mm});
            skPoint(sketch, "E14.46.3", {"position": v(57.27, -46.9) * mm});
            skLineSegment(sketch, "E14.46.4", {"start": v(58.35, -48.96) * mm, "end": v(59.7, -50.1) * mm});
            skLineSegment(sketch, "E14.46.5", {"start": v(60.44, -46.38) * mm, "end": v(61.82, -47.45) * mm});
            skPoint(sketch, "E14.46.6", {"position": v(58.2, -45.75) * mm});
            skLineSegment(sketch, "E14.46.7", {"start": v(57.42, -46.72) * mm, "end": v(57.73, -46.32) * mm});
            skLineSegment(sketch, "E14.46.8", {"start": v(58.06, -45.93) * mm, "end": v(57.73, -46.32) * mm});
            skArc(sketch, "E14.46.9", {"start": v(57.42, -46.72) * mm, "mid": v(57.34, -46.91) * mm, "end": v(57.37, -47.12) * mm});
            skArc(sketch, "E14.46.10", {"start": v(58.44, -45.8) * mm, "mid": v(58.23, -45.8) * mm, "end": v(58.06, -45.93) * mm});
            skArc(sketch, "E14.46.11", {"start": v(59.74, -50.64) * mm, "mid": v(59.83, -50.36) * mm, "end": v(59.7, -50.1) * mm});
            skArc(sketch, "E14.46.12", {"start": v(61.82, -47.45) * mm, "mid": v(62.1, -47.53) * mm, "end": v(62.36, -47.38) * mm});
            skArc(sketch, "E14.47.0", {"start": v(62.4, -43.69) * mm, "mid": v(61.8, -42.83) * mm, "end": v(61.26, -41.94) * mm});
            skArc(sketch, "E14.47.1", {"start": v(64.25, -40.93) * mm, "mid": v(63.24, -40.7) * mm, "end": v(62.2, -40.53) * mm});
            skPoint(sketch, "E14.47.2", {"position": v(64.15, -44.93) * mm});
            skPoint(sketch, "E14.47.3", {"position": v(61.14, -41.73) * mm});
            skLineSegment(sketch, "E14.47.4", {"start": v(62.4, -43.69) * mm, "end": v(63.84, -44.71) * mm});
            skLineSegment(sketch, "E14.47.5", {"start": v(64.25, -40.93) * mm, "end": v(65.72, -41.88) * mm});
            skPoint(sketch, "E14.47.6", {"position": v(61.98, -40.5) * mm});
            skLineSegment(sketch, "E14.47.7", {"start": v(61.27, -41.54) * mm, "end": v(61.55, -41.11) * mm});
            skLineSegment(sketch, "E14.47.8", {"start": v(61.84, -40.7) * mm, "end": v(61.55, -41.11) * mm});
            skArc(sketch, "E14.47.9", {"start": v(61.27, -41.54) * mm, "mid": v(61.2, -41.74) * mm, "end": v(61.26, -41.94) * mm});
            skArc(sketch, "E14.47.10", {"start": v(62.2, -40.53) * mm, "mid": v(62, -40.56) * mm, "end": v(61.84, -40.7) * mm});
            skArc(sketch, "E14.47.11", {"start": v(63.93, -45.24) * mm, "mid": v(64, -44.96) * mm, "end": v(63.84, -44.71) * mm});
            skArc(sketch, "E14.47.12", {"start": v(65.72, -41.88) * mm, "mid": v(66.01, -41.93) * mm, "end": v(66.25, -41.76) * mm});
            skArc(sketch, "E14.48.0", {"start": v(65.96, -38.08) * mm, "mid": v(65.3, -37.28) * mm, "end": v(64.68, -36.44) * mm});
            skArc(sketch, "E14.48.1", {"start": v(67.58, -35.18) * mm, "mid": v(66.54, -35.04) * mm, "end": v(65.5, -34.95) * mm});
            skPoint(sketch, "E14.48.2", {"position": v(67.82, -39.17) * mm});
            skPoint(sketch, "E14.48.3", {"position": v(64.54, -36.25) * mm});
            skLineSegment(sketch, "E14.48.4", {"start": v(65.96, -38.08) * mm, "end": v(67.49, -38.98) * mm});
            skLineSegment(sketch, "E14.48.5", {"start": v(67.58, -35.18) * mm, "end": v(69.12, -36) * mm});
            skPoint(sketch, "E14.48.6", {"position": v(65.27, -34.94) * mm});
            skLineSegment(sketch, "E14.48.7", {"start": v(64.66, -36.04) * mm, "end": v(64.9, -35.6) * mm});
            skLineSegment(sketch, "E14.48.8", {"start": v(65.15, -35.15) * mm, "end": v(64.9, -35.6) * mm});
            skArc(sketch, "E14.48.9", {"start": v(64.66, -36.04) * mm, "mid": v(64.61, -36.24) * mm, "end": v(64.68, -36.44) * mm});
            skArc(sketch, "E14.48.10", {"start": v(65.5, -34.95) * mm, "mid": v(65.3, -35) * mm, "end": v(65.15, -35.15) * mm});
            skArc(sketch, "E14.48.11", {"start": v(67.63, -39.5) * mm, "mid": v(67.67, -39.2) * mm, "end": v(67.49, -38.98) * mm});
            skArc(sketch, "E14.48.12", {"start": v(69.12, -36) * mm, "mid": v(69.41, -36.02) * mm, "end": v(69.64, -35.83) * mm});
            skArc(sketch, "E14.49.0", {"start": v(69.03, -32.19) * mm, "mid": v(68.3, -31.45) * mm, "end": v(67.6, -30.67) * mm});
            skArc(sketch, "E14.49.1", {"start": v(70.39, -29.15) * mm, "mid": v(69.34, -29.1) * mm, "end": v(68.3, -29.11) * mm});
            skPoint(sketch, "E14.49.2", {"position": v(70.97, -33.1) * mm});
            skPoint(sketch, "E14.49.3", {"position": v(67.46, -30.48) * mm});
            skLineSegment(sketch, "E14.49.4", {"start": v(69.03, -32.19) * mm, "end": v(70.63, -32.95) * mm});
            skLineSegment(sketch, "E14.49.5", {"start": v(70.39, -29.15) * mm, "end": v(72, -29.83) * mm});
            skPoint(sketch, "E14.49.6", {"position": v(68.07, -29.12) * mm});
            skLineSegment(sketch, "E14.49.7", {"start": v(67.55, -30.27) * mm, "end": v(67.76, -29.8) * mm});
            skLineSegment(sketch, "E14.49.8", {"start": v(67.97, -29.33) * mm, "end": v(67.76, -29.8) * mm});
            skArc(sketch, "E14.49.9", {"start": v(67.55, -30.27) * mm, "mid": v(67.52, -30.48) * mm, "end": v(67.6, -30.67) * mm});
            skArc(sketch, "E14.49.10", {"start": v(68.3, -29.11) * mm, "mid": v(68.1, -29.18) * mm, "end": v(67.97, -29.33) * mm});
            skArc(sketch, "E14.49.11", {"start": v(70.81, -33.45) * mm, "mid": v(70.83, -33.16) * mm, "end": v(70.63, -32.95) * mm});
            skArc(sketch, "E14.49.12", {"start": v(72, -29.83) * mm, "mid": v(72.3, -29.83) * mm, "end": v(72.5, -29.63) * mm});
            skArc(sketch, "E14.50.0", {"start": v(71.57, -26.05) * mm, "mid": v(70.78, -25.37) * mm, "end": v(70.02, -24.66) * mm});
            skArc(sketch, "E14.50.1", {"start": v(72.66, -22.9) * mm, "mid": v(71.62, -22.95) * mm, "end": v(70.58, -23.05) * mm});
            skPoint(sketch, "E14.50.2", {"position": v(73.59, -26.8) * mm});
            skPoint(sketch, "E14.50.3", {"position": v(69.86, -24.49) * mm});
            skLineSegment(sketch, "E14.50.4", {"start": v(71.57, -26.05) * mm, "end": v(73.23, -26.67) * mm});
            skLineSegment(sketch, "E14.50.5", {"start": v(72.66, -22.9) * mm, "end": v(74.32, -23.44) * mm});
            skPoint(sketch, "E14.50.6", {"position": v(70.35, -23.08) * mm});
            skLineSegment(sketch, "E14.50.7", {"start": v(69.93, -24.27) * mm, "end": v(70.1, -23.78) * mm});
            skLineSegment(sketch, "E14.50.8", {"start": v(70.27, -23.3) * mm, "end": v(70.1, -23.78) * mm});
            skArc(sketch, "E14.50.9", {"start": v(69.93, -24.27) * mm, "mid": v(69.92, -24.47) * mm, "end": v(70.02, -24.66) * mm});
            skArc(sketch, "E14.50.10", {"start": v(70.58, -23.05) * mm, "mid": v(70.39, -23.13) * mm, "end": v(70.27, -23.3) * mm});
            skArc(sketch, "E14.50.11", {"start": v(73.46, -27.16) * mm, "mid": v(73.45, -26.86) * mm, "end": v(73.23, -26.67) * mm});
            skArc(sketch, "E14.50.12", {"start": v(74.32, -23.44) * mm, "mid": v(74.62, -23.42) * mm, "end": v(74.8, -23.2) * mm});
            skArc(sketch, "E14.51.0", {"start": v(73.57, -19.71) * mm, "mid": v(72.72, -19.1) * mm, "end": v(71.9, -18.46) * mm});
            skArc(sketch, "E14.51.1", {"start": v(74.38, -16.49) * mm, "mid": v(73.35, -16.62) * mm, "end": v(72.32, -16.8) * mm});
            skPoint(sketch, "E14.51.2", {"position": v(75.64, -20.28) * mm});
            skPoint(sketch, "E14.51.3", {"position": v(71.73, -18.3) * mm});
            skLineSegment(sketch, "E14.51.4", {"start": v(73.57, -19.71) * mm, "end": v(75.28, -20.18) * mm});
            skLineSegment(sketch, "E14.51.5", {"start": v(74.38, -16.49) * mm, "end": v(76.08, -16.88) * mm});
            skPoint(sketch, "E14.51.6", {"position": v(72.09, -16.86) * mm});
            skLineSegment(sketch, "E14.51.7", {"start": v(71.78, -18.08) * mm, "end": v(71.9, -17.58) * mm});
            skLineSegment(sketch, "E14.51.8", {"start": v(72.03, -17.09) * mm, "end": v(71.9, -17.58) * mm});
            skArc(sketch, "E14.51.9", {"start": v(71.78, -18.08) * mm, "mid": v(71.79, -18.29) * mm, "end": v(71.9, -18.46) * mm});
            skArc(sketch, "E14.51.10", {"start": v(72.32, -16.8) * mm, "mid": v(72.14, -16.9) * mm, "end": v(72.03, -17.09) * mm});
            skArc(sketch, "E14.51.11", {"start": v(75.55, -20.65) * mm, "mid": v(75.5, -20.36) * mm, "end": v(75.28, -20.18) * mm});
            skArc(sketch, "E14.51.12", {"start": v(76.08, -16.88) * mm, "mid": v(76.37, -16.83) * mm, "end": v(76.54, -16.59) * mm});
            skArc(sketch, "E14.52.0", {"start": v(75, -13.23) * mm, "mid": v(74.11, -12.7) * mm, "end": v(73.24, -12.12) * mm});
            skArc(sketch, "E14.52.1", {"start": v(75.53, -9.94) * mm, "mid": v(74.51, -10.17) * mm, "end": v(73.5, -10.44) * mm});
            skPoint(sketch, "E14.52.2", {"position": v(77.12, -13.61) * mm});
            skPoint(sketch, "E14.52.3", {"position": v(73.05, -11.99) * mm});
            skLineSegment(sketch, "E14.52.4", {"start": v(75, -13.23) * mm, "end": v(76.75, -13.54) * mm});
            skLineSegment(sketch, "E14.52.5", {"start": v(75.53, -9.94) * mm, "end": v(77.26, -10.18) * mm});
            skPoint(sketch, "E14.52.6", {"position": v(73.28, -10.51) * mm});
            skLineSegment(sketch, "E14.52.7", {"start": v(73.08, -11.75) * mm, "end": v(73.16, -11.25) * mm});
            skLineSegment(sketch, "E14.52.8", {"start": v(73.25, -10.74) * mm, "end": v(73.16, -11.25) * mm});
            skArc(sketch, "E14.52.9", {"start": v(73.08, -11.75) * mm, "mid": v(73.11, -11.96) * mm, "end": v(73.24, -12.12) * mm});
            skArc(sketch, "E14.52.10", {"start": v(73.5, -10.44) * mm, "mid": v(73.33, -10.56) * mm, "end": v(73.25, -10.74) * mm});
            skArc(sketch, "E14.52.11", {"start": v(77.06, -13.99) * mm, "mid": v(77, -13.7) * mm, "end": v(76.75, -13.54) * mm});
            skArc(sketch, "E14.52.12", {"start": v(77.26, -10.18) * mm, "mid": v(77.55, -10.1) * mm, "end": v(77.7, -9.85) * mm});
            skArc(sketch, "E14.53.0", {"start": v(75.88, -6.64) * mm, "mid": v(74.93, -6.2) * mm, "end": v(74.02, -5.7) * mm});
            skArc(sketch, "E14.53.1", {"start": v(76.11, -3.32) * mm, "mid": v(75.12, -3.63) * mm, "end": v(74.14, -4) * mm});
            skPoint(sketch, "E14.53.2", {"position": v(78.02, -6.84) * mm});
            skPoint(sketch, "E14.53.3", {"position": v(73.82, -5.57) * mm});
            skLineSegment(sketch, "E14.53.4", {"start": v(75.88, -6.64) * mm, "end": v(77.64, -6.8) * mm});
            skLineSegment(sketch, "E14.53.5", {"start": v(76.11, -3.32) * mm, "end": v(77.86, -3.4) * mm});
            skPoint(sketch, "E14.53.6", {"position": v(73.92, -4.09) * mm});
            skLineSegment(sketch, "E14.53.7", {"start": v(73.83, -5.34) * mm, "end": v(73.86, -4.83) * mm});
            skLineSegment(sketch, "E14.53.8", {"start": v(73.9, -4.32) * mm, "end": v(73.86, -4.83) * mm});
            skArc(sketch, "E14.53.9", {"start": v(73.83, -5.34) * mm, "mid": v(73.87, -5.54) * mm, "end": v(74.02, -5.7) * mm});
            skArc(sketch, "E14.53.10", {"start": v(74.14, -4) * mm, "mid": v(73.98, -4.12) * mm, "end": v(73.9, -4.32) * mm});
            skArc(sketch, "E14.53.11", {"start": v(77.98, -7.22) * mm, "mid": v(77.9, -6.94) * mm, "end": v(77.64, -6.8) * mm});
            skArc(sketch, "E14.53.12", {"start": v(77.86, -3.4) * mm, "mid": v(78.13, -3.3) * mm, "end": v(78.26, -3.04) * mm});
            skArc(sketch, "E14.54.0", {"start": v(76.17, 0) * mm, "mid": v(75.19, 0.36) * mm, "end": v(74.23, 0.78) * mm});
            skArc(sketch, "E14.54.1", {"start": v(76.11, 3.32) * mm, "mid": v(75.15, 2.93) * mm, "end": v(74.2, 2.48) * mm});
            skPoint(sketch, "E14.54.2", {"position": v(78.32, -0.01) * mm});
            skPoint(sketch, "E14.54.3", {"position": v(74.02, 0.88) * mm});
            skLineSegment(sketch, "E14.54.4", {"start": v(76.17, 0) * mm, "end": v(77.94, -0.01) * mm});
            skLineSegment(sketch, "E14.54.5", {"start": v(76.11, 3.32) * mm, "end": v(77.86, 3.39) * mm});
            skPoint(sketch, "E14.54.6", {"position": v(74, 2.37) * mm});
            skLineSegment(sketch, "E14.54.7", {"start": v(74.01, 1.12) * mm, "end": v(74, 1.63) * mm});
            skLineSegment(sketch, "E14.54.8", {"start": v(74, 2.14) * mm, "end": v(74, 1.63) * mm});
            skArc(sketch, "E14.54.9", {"start": v(74.01, 1.12) * mm, "mid": v(74.08, 0.92) * mm, "end": v(74.23, 0.78) * mm});
            skArc(sketch, "E14.54.10", {"start": v(74.2, 2.48) * mm, "mid": v(74.05, 2.34) * mm, "end": v(74, 2.14) * mm});
            skArc(sketch, "E14.54.11", {"start": v(78.32, -0.4) * mm, "mid": v(78.2, -0.12) * mm, "end": v(77.94, -0.01) * mm});
            skArc(sketch, "E14.54.12", {"start": v(77.86, 3.39) * mm, "mid": v(78.13, 3.51) * mm, "end": v(78.22, 3.79) * mm});
            skArc(sketch, "E14.55.0", {"start": v(75.88, 6.64) * mm, "mid": v(74.87, 6.92) * mm, "end": v(73.88, 7.25) * mm});
            skArc(sketch, "E14.55.1", {"start": v(75.53, 9.94) * mm, "mid": v(74.6, 9.47) * mm, "end": v(73.7, 8.94) * mm});
            skPoint(sketch, "E14.55.2", {"position": v(78.02, 6.81) * mm});
            skPoint(sketch, "E14.55.3", {"position": v(73.66, 7.33) * mm});
            skLineSegment(sketch, "E14.55.4", {"start": v(75.88, 6.64) * mm, "end": v(77.64, 6.78) * mm});
            skLineSegment(sketch, "E14.55.5", {"start": v(75.53, 9.94) * mm, "end": v(77.27, 10.16) * mm});
            skPoint(sketch, "E14.55.6", {"position": v(73.5, 8.81) * mm});
            skLineSegment(sketch, "E14.55.7", {"start": v(73.64, 7.56) * mm, "end": v(73.58, 8.07) * mm});
            skLineSegment(sketch, "E14.55.8", {"start": v(73.53, 8.58) * mm, "end": v(73.58, 8.07) * mm});
            skArc(sketch, "E14.55.9", {"start": v(73.64, 7.56) * mm, "mid": v(73.71, 7.37) * mm, "end": v(73.88, 7.25) * mm});
            skArc(sketch, "E14.55.10", {"start": v(73.7, 8.94) * mm, "mid": v(73.57, 8.78) * mm, "end": v(73.53, 8.58) * mm});
            skArc(sketch, "E14.55.11", {"start": v(78.05, 6.43) * mm, "mid": v(77.92, 6.7) * mm, "end": v(77.64, 6.78) * mm});
            skArc(sketch, "E14.55.12", {"start": v(77.27, 10.16) * mm, "mid": v(77.52, 10.3) * mm, "end": v(77.6, 10.6) * mm});
            skArc(sketch, "E14.56.0", {"start": v(75, 13.23) * mm, "mid": v(73.98, 13.41) * mm, "end": v(72.97, 13.66) * mm});
            skArc(sketch, "E14.56.1", {"start": v(74.38, 16.49) * mm, "mid": v(73.5, 15.93) * mm, "end": v(72.65, 15.33) * mm});
            skPoint(sketch, "E14.56.2", {"position": v(77.13, 13.59) * mm});
            skPoint(sketch, "E14.56.3", {"position": v(72.74, 13.72) * mm});
            skLineSegment(sketch, "E14.56.4", {"start": v(75, 13.23) * mm, "end": v(76.75, 13.52) * mm});
            skLineSegment(sketch, "E14.56.5", {"start": v(74.38, 16.49) * mm, "end": v(76.09, 16.86) * mm});
            skPoint(sketch, "E14.56.6", {"position": v(72.46, 15.19) * mm});
            skLineSegment(sketch, "E14.56.7", {"start": v(72.7, 13.95) * mm, "end": v(72.6, 14.45) * mm});
            skLineSegment(sketch, "E14.56.8", {"start": v(72.5, 14.96) * mm, "end": v(72.6, 14.45) * mm});
            skArc(sketch, "E14.56.9", {"start": v(72.7, 13.95) * mm, "mid": v(72.8, 13.77) * mm, "end": v(72.97, 13.66) * mm});
            skArc(sketch, "E14.56.10", {"start": v(72.65, 15.33) * mm, "mid": v(72.52, 15.16) * mm, "end": v(72.5, 14.96) * mm});
            skArc(sketch, "E14.56.11", {"start": v(77.2, 13.21) * mm, "mid": v(77.04, 13.46) * mm, "end": v(76.75, 13.52) * mm});
            skArc(sketch, "E14.56.12", {"start": v(76.09, 16.86) * mm, "mid": v(76.33, 17.03) * mm, "end": v(76.38, 17.32) * mm});
            skArc(sketch, "E14.57.0", {"start": v(73.57, 19.71) * mm, "mid": v(72.53, 19.81) * mm, "end": v(71.5, 19.97) * mm});
            skArc(sketch, "E14.57.1", {"start": v(72.66, 22.9) * mm, "mid": v(71.83, 22.28) * mm, "end": v(71.04, 21.6) * mm});
            skPoint(sketch, "E14.57.2", {"position": v(75.65, 20.26) * mm});
            skPoint(sketch, "E14.57.3", {"position": v(71.27, 20) * mm});
            skLineSegment(sketch, "E14.57.4", {"start": v(73.57, 19.71) * mm, "end": v(75.28, 20.16) * mm});
            skLineSegment(sketch, "E14.57.5", {"start": v(72.66, 22.9) * mm, "end": v(74.33, 23.43) * mm});
            skPoint(sketch, "E14.57.6", {"position": v(70.86, 21.44) * mm});
            skLineSegment(sketch, "E14.57.7", {"start": v(71.2, 20.23) * mm, "end": v(71.06, 20.72) * mm});
            skLineSegment(sketch, "E14.57.8", {"start": v(70.92, 21.22) * mm, "end": v(71.06, 20.72) * mm});
            skArc(sketch, "E14.57.9", {"start": v(71.2, 20.23) * mm, "mid": v(71.32, 20.06) * mm, "end": v(71.5, 19.97) * mm});
            skArc(sketch, "E14.57.10", {"start": v(71.04, 21.6) * mm, "mid": v(70.92, 21.43) * mm, "end": v(70.92, 21.22) * mm});
            skArc(sketch, "E14.57.11", {"start": v(75.75, 19.89) * mm, "mid": v(75.57, 20.12) * mm, "end": v(75.28, 20.16) * mm});
            skArc(sketch, "E14.57.12", {"start": v(74.33, 23.43) * mm, "mid": v(74.55, 23.61) * mm, "end": v(74.58, 23.9) * mm});
            skArc(sketch, "E14.58.0", {"start": v(71.57, 26.05) * mm, "mid": v(70.53, 26.06) * mm, "end": v(69.5, 26.12) * mm});
            skArc(sketch, "E14.58.1", {"start": v(70.39, 29.16) * mm, "mid": v(69.61, 28.45) * mm, "end": v(68.88, 27.71) * mm});
            skPoint(sketch, "E14.58.2", {"position": v(73.6, 26.77) * mm});
            skPoint(sketch, "E14.58.3", {"position": v(69.26, 26.15) * mm});
            skLineSegment(sketch, "E14.58.4", {"start": v(71.57, 26.05) * mm, "end": v(73.24, 26.65) * mm});
            skLineSegment(sketch, "E14.58.5", {"start": v(70.39, 29.16) * mm, "end": v(72, 29.81) * mm});
            skPoint(sketch, "E14.58.6", {"position": v(68.72, 27.54) * mm});
            skLineSegment(sketch, "E14.58.7", {"start": v(69.17, 26.36) * mm, "end": v(68.98, 26.84) * mm});
            skLineSegment(sketch, "E14.58.8", {"start": v(68.8, 27.32) * mm, "end": v(68.98, 26.84) * mm});
            skArc(sketch, "E14.58.9", {"start": v(69.17, 26.36) * mm, "mid": v(69.3, 26.2) * mm, "end": v(69.5, 26.12) * mm});
            skArc(sketch, "E14.58.10", {"start": v(68.88, 27.71) * mm, "mid": v(68.79, 27.53) * mm, "end": v(68.8, 27.32) * mm});
            skArc(sketch, "E14.58.11", {"start": v(73.73, 26.42) * mm, "mid": v(73.53, 26.63) * mm, "end": v(73.24, 26.65) * mm});
            skArc(sketch, "E14.58.12", {"start": v(72, 29.81) * mm, "mid": v(72.21, 30.02) * mm, "end": v(72.21, 30.31) * mm});
            skArc(sketch, "E14.59.0", {"start": v(69.03, 32.19) * mm, "mid": v(68, 32.1) * mm, "end": v(66.95, 32.08) * mm});
            skArc(sketch, "E14.59.1", {"start": v(67.58, 35.18) * mm, "mid": v(66.87, 34.41) * mm, "end": v(66.2, 33.6) * mm});
            skPoint(sketch, "E14.59.2", {"position": v(70.98, 33.09) * mm});
            skPoint(sketch, "E14.59.3", {"position": v(66.71, 32.08) * mm});
            skLineSegment(sketch, "E14.59.4", {"start": v(69.03, 32.19) * mm, "end": v(70.64, 32.93) * mm});
            skLineSegment(sketch, "E14.59.5", {"start": v(67.58, 35.18) * mm, "end": v(69.13, 35.98) * mm});
            skPoint(sketch, "E14.59.6", {"position": v(66.06, 33.42) * mm});
            skLineSegment(sketch, "E14.59.7", {"start": v(66.6, 32.3) * mm, "end": v(66.38, 32.75) * mm});
            skLineSegment(sketch, "E14.59.8", {"start": v(66.16, 33.21) * mm, "end": v(66.38, 32.75) * mm});
            skArc(sketch, "E14.59.9", {"start": v(66.6, 32.3) * mm, "mid": v(66.75, 32.14) * mm, "end": v(66.95, 32.08) * mm});
            skArc(sketch, "E14.59.10", {"start": v(66.2, 33.6) * mm, "mid": v(66.13, 33.42) * mm, "end": v(66.16, 33.21) * mm});
            skArc(sketch, "E14.59.11", {"start": v(71.14, 32.74) * mm, "mid": v(70.93, 32.94) * mm, "end": v(70.64, 32.93) * mm});
            skArc(sketch, "E14.59.12", {"start": v(69.13, 35.98) * mm, "mid": v(69.32, 36.2) * mm, "end": v(69.3, 36.5) * mm});
            skArc(sketch, "E14.60.0", {"start": v(65.96, 38.08) * mm, "mid": v(64.93, 37.9) * mm, "end": v(63.9, 37.8) * mm});
            skArc(sketch, "E14.60.1", {"start": v(64.25, 40.93) * mm, "mid": v(63.62, 40.1) * mm, "end": v(63.02, 39.25) * mm});
            skPoint(sketch, "E14.60.2", {"position": v(67.83, 39.15) * mm});
            skPoint(sketch, "E14.60.3", {"position": v(63.66, 37.77) * mm});
            skLineSegment(sketch, "E14.60.4", {"start": v(65.96, 38.08) * mm, "end": v(67.5, 38.96) * mm});
            skLineSegment(sketch, "E14.60.5", {"start": v(64.25, 40.93) * mm, "end": v(65.73, 41.87) * mm});
            skPoint(sketch, "E14.60.6", {"position": v(62.9, 39.05) * mm});
            skLineSegment(sketch, "E14.60.7", {"start": v(63.54, 37.97) * mm, "end": v(63.27, 38.4) * mm});
            skLineSegment(sketch, "E14.60.8", {"start": v(63.01, 38.85) * mm, "end": v(63.27, 38.4) * mm});
            skArc(sketch, "E14.60.9", {"start": v(63.54, 37.97) * mm, "mid": v(63.7, 37.83) * mm, "end": v(63.9, 37.8) * mm});
            skArc(sketch, "E14.60.10", {"start": v(63.02, 39.25) * mm, "mid": v(62.96, 39.05) * mm, "end": v(63.01, 38.85) * mm});
            skArc(sketch, "E14.60.11", {"start": v(68.02, 38.82) * mm, "mid": v(67.79, 39) * mm, "end": v(67.5, 38.96) * mm});
            skArc(sketch, "E14.60.12", {"start": v(65.73, 41.87) * mm, "mid": v(65.9, 42.1) * mm, "end": v(65.85, 42.4) * mm});
            skArc(sketch, "E14.61.0", {"start": v(62.4, 43.69) * mm, "mid": v(61.38, 43.42) * mm, "end": v(60.36, 43.22) * mm});
            skArc(sketch, "E14.61.1", {"start": v(60.44, 46.38) * mm, "mid": v(59.88, 45.5) * mm, "end": v(59.36, 44.6) * mm});
            skPoint(sketch, "E14.61.2", {"position": v(64.16, 44.91) * mm});
            skPoint(sketch, "E14.61.3", {"position": v(60.13, 43.18) * mm});
            skLineSegment(sketch, "E14.61.4", {"start": v(62.4, 43.69) * mm, "end": v(63.85, 44.7) * mm});
            skLineSegment(sketch, "E14.61.5", {"start": v(60.44, 46.38) * mm, "end": v(61.83, 47.43) * mm});
            skPoint(sketch, "E14.61.6", {"position": v(59.25, 44.39) * mm});
            skLineSegment(sketch, "E14.61.7", {"start": v(59.99, 43.37) * mm, "end": v(59.69, 43.78) * mm});
            skLineSegment(sketch, "E14.61.8", {"start": v(59.39, 44.2) * mm, "end": v(59.69, 43.78) * mm});
            skArc(sketch, "E14.61.9", {"start": v(59.99, 43.37) * mm, "mid": v(60.15, 43.24) * mm, "end": v(60.36, 43.22) * mm});
            skArc(sketch, "E14.61.10", {"start": v(59.36, 44.6) * mm, "mid": v(59.32, 44.4) * mm, "end": v(59.39, 44.2) * mm});
            skArc(sketch, "E14.61.11", {"start": v(64.38, 44.6) * mm, "mid": v(64.13, 44.76) * mm, "end": v(63.85, 44.7) * mm});
            skArc(sketch, "E14.61.12", {"start": v(61.83, 47.43) * mm, "mid": v(61.98, 47.69) * mm, "end": v(61.9, 47.97) * mm});
            skArc(sketch, "E14.62.0", {"start": v(58.35, 48.96) * mm, "mid": v(57.36, 48.6) * mm, "end": v(56.36, 48.31) * mm});
            skArc(sketch, "E14.62.1", {"start": v(56.17, 51.47) * mm, "mid": v(55.68, 50.55) * mm, "end": v(55.25, 49.6) * mm});
            skPoint(sketch, "E14.62.2", {"position": v(60, 50.33) * mm});
            skPoint(sketch, "E14.62.3", {"position": v(56.14, 48.26) * mm});
            skLineSegment(sketch, "E14.62.4", {"start": v(58.35, 48.96) * mm, "end": v(59.7, 50.09) * mm});
            skLineSegment(sketch, "E14.62.5", {"start": v(56.17, 51.47) * mm, "end": v(57.46, 52.64) * mm});
            skPoint(sketch, "E14.62.6", {"position": v(55.16, 49.38) * mm});
            skLineSegment(sketch, "E14.62.7", {"start": v(55.98, 48.43) * mm, "end": v(55.64, 48.81) * mm});
            skLineSegment(sketch, "E14.62.8", {"start": v(55.31, 49.2) * mm, "end": v(55.64, 48.81) * mm});
            skArc(sketch, "E14.62.9", {"start": v(55.98, 48.43) * mm, "mid": v(56.16, 48.32) * mm, "end": v(56.36, 48.31) * mm});
            skArc(sketch, "E14.62.10", {"start": v(55.25, 49.6) * mm, "mid": v(55.22, 49.4) * mm, "end": v(55.31, 49.2) * mm});
            skArc(sketch, "E14.62.11", {"start": v(60.25, 50.04) * mm, "mid": v(59.99, 50.17) * mm, "end": v(59.7, 50.09) * mm});
            skArc(sketch, "E14.62.12", {"start": v(57.46, 52.64) * mm, "mid": v(57.59, 52.9) * mm, "end": v(57.49, 53.18) * mm});
            skArc(sketch, "E14.63.0", {"start": v(53.86, 53.86) * mm, "mid": v(52.91, 53.42) * mm, "end": v(51.94, 53.04) * mm});
            skArc(sketch, "E14.63.1", {"start": v(51.47, 56.17) * mm, "mid": v(51.07, 55.2) * mm, "end": v(50.72, 54.23) * mm});
            skPoint(sketch, "E14.63.2", {"position": v(55.39, 55.37) * mm});
            skPoint(sketch, "E14.63.3", {"position": v(51.72, 52.96) * mm});
            skLineSegment(sketch, "E14.63.4", {"start": v(53.86, 53.86) * mm, "end": v(55.12, 55.1) * mm});
            skLineSegment(sketch, "E14.63.5", {"start": v(51.47, 56.17) * mm, "end": v(52.66, 57.45) * mm});
            skPoint(sketch, "E14.63.6", {"position": v(50.65, 54) * mm});
            skLineSegment(sketch, "E14.63.7", {"start": v(51.55, 53.12) * mm, "end": v(51.18, 53.48) * mm});
            skLineSegment(sketch, "E14.63.8", {"start": v(50.81, 53.84) * mm, "end": v(51.18, 53.48) * mm});
            skArc(sketch, "E14.63.9", {"start": v(51.55, 53.12) * mm, "mid": v(51.73, 53.03) * mm, "end": v(51.94, 53.04) * mm});
            skArc(sketch, "E14.63.10", {"start": v(50.72, 54.23) * mm, "mid": v(50.7, 54.02) * mm, "end": v(50.81, 53.84) * mm});
            skArc(sketch, "E14.63.11", {"start": v(55.66, 55.1) * mm, "mid": v(55.39, 55.21) * mm, "end": v(55.12, 55.1) * mm});
            skArc(sketch, "E14.63.12", {"start": v(52.66, 57.45) * mm, "mid": v(52.76, 57.73) * mm, "end": v(52.63, 58) * mm});
            skArc(sketch, "E14.64.0", {"start": v(48.96, 58.35) * mm, "mid": v(48.05, 57.83) * mm, "end": v(47.12, 57.37) * mm});
            skArc(sketch, "E14.64.1", {"start": v(46.38, 60.44) * mm, "mid": v(46.06, 59.45) * mm, "end": v(45.8, 58.44) * mm});
            skPoint(sketch, "E14.64.2", {"position": v(50.35, 59.99) * mm});
            skPoint(sketch, "E14.64.3", {"position": v(46.9, 57.27) * mm});
            skLineSegment(sketch, "E14.64.4", {"start": v(48.96, 58.35) * mm, "end": v(50.1, 59.7) * mm});
            skLineSegment(sketch, "E14.64.5", {"start": v(46.38, 60.44) * mm, "end": v(47.45, 61.82) * mm});
            skPoint(sketch, "E14.64.6", {"position": v(45.75, 58.2) * mm});
            skLineSegment(sketch, "E14.64.7", {"start": v(46.72, 57.42) * mm, "end": v(46.32, 57.73) * mm});
            skLineSegment(sketch, "E14.64.8", {"start": v(45.93, 58.06) * mm, "end": v(46.32, 57.73) * mm});
            skArc(sketch, "E14.64.9", {"start": v(46.72, 57.42) * mm, "mid": v(46.91, 57.34) * mm, "end": v(47.12, 57.37) * mm});
            skArc(sketch, "E14.64.10", {"start": v(45.8, 58.44) * mm, "mid": v(45.8, 58.23) * mm, "end": v(45.93, 58.06) * mm});
            skArc(sketch, "E14.64.11", {"start": v(50.64, 59.74) * mm, "mid": v(50.36, 59.83) * mm, "end": v(50.1, 59.7) * mm});
            skArc(sketch, "E14.64.12", {"start": v(47.45, 61.82) * mm, "mid": v(47.53, 62.1) * mm, "end": v(47.38, 62.36) * mm});
            skArc(sketch, "E14.65.0", {"start": v(43.69, 62.4) * mm, "mid": v(42.83, 61.8) * mm, "end": v(41.94, 61.26) * mm});
            skArc(sketch, "E14.65.1", {"start": v(40.93, 64.25) * mm, "mid": v(40.7, 63.24) * mm, "end": v(40.53, 62.2) * mm});
            skPoint(sketch, "E14.65.2", {"position": v(44.93, 64.15) * mm});
            skPoint(sketch, "E14.65.3", {"position": v(41.73, 61.14) * mm});
            skLineSegment(sketch, "E14.65.4", {"start": v(43.69, 62.4) * mm, "end": v(44.71, 63.84) * mm});
            skLineSegment(sketch, "E14.65.5", {"start": v(40.93, 64.25) * mm, "end": v(41.88, 65.72) * mm});
            skPoint(sketch, "E14.65.6", {"position": v(40.5, 61.98) * mm});
            skLineSegment(sketch, "E14.65.7", {"start": v(41.54, 61.27) * mm, "end": v(41.11, 61.55) * mm});
            skLineSegment(sketch, "E14.65.8", {"start": v(40.7, 61.84) * mm, "end": v(41.11, 61.55) * mm});
            skArc(sketch, "E14.65.9", {"start": v(41.54, 61.27) * mm, "mid": v(41.74, 61.2) * mm, "end": v(41.94, 61.26) * mm});
            skArc(sketch, "E14.65.10", {"start": v(40.53, 62.2) * mm, "mid": v(40.56, 62) * mm, "end": v(40.7, 61.84) * mm});
            skArc(sketch, "E14.65.11", {"start": v(45.24, 63.93) * mm, "mid": v(44.96, 64) * mm, "end": v(44.71, 63.84) * mm});
            skArc(sketch, "E14.65.12", {"start": v(41.88, 65.72) * mm, "mid": v(41.93, 66.01) * mm, "end": v(41.76, 66.25) * mm});
            skArc(sketch, "E14.66.0", {"start": v(38.08, 65.96) * mm, "mid": v(37.28, 65.3) * mm, "end": v(36.44, 64.68) * mm});
            skArc(sketch, "E14.66.1", {"start": v(35.18, 67.58) * mm, "mid": v(35.04, 66.54) * mm, "end": v(34.95, 65.5) * mm});
            skPoint(sketch, "E14.66.2", {"position": v(39.17, 67.82) * mm});
            skPoint(sketch, "E14.66.3", {"position": v(36.25, 64.54) * mm});
            skLineSegment(sketch, "E14.66.4", {"start": v(38.08, 65.96) * mm, "end": v(38.98, 67.49) * mm});
            skLineSegment(sketch, "E14.66.5", {"start": v(35.18, 67.58) * mm, "end": v(36, 69.12) * mm});
            skPoint(sketch, "E14.66.6", {"position": v(34.94, 65.27) * mm});
            skLineSegment(sketch, "E14.66.7", {"start": v(36.04, 64.66) * mm, "end": v(35.6, 64.9) * mm});
            skLineSegment(sketch, "E14.66.8", {"start": v(35.15, 65.15) * mm, "end": v(35.6, 64.9) * mm});
            skArc(sketch, "E14.66.9", {"start": v(36.04, 64.66) * mm, "mid": v(36.24, 64.61) * mm, "end": v(36.44, 64.68) * mm});
            skArc(sketch, "E14.66.10", {"start": v(34.95, 65.5) * mm, "mid": v(35, 65.3) * mm, "end": v(35.15, 65.15) * mm});
            skArc(sketch, "E14.66.11", {"start": v(39.5, 67.63) * mm, "mid": v(39.2, 67.67) * mm, "end": v(38.98, 67.49) * mm});
            skArc(sketch, "E14.66.12", {"start": v(36, 69.12) * mm, "mid": v(36.02, 69.41) * mm, "end": v(35.83, 69.64) * mm});
            skArc(sketch, "E14.67.0", {"start": v(32.19, 69.03) * mm, "mid": v(31.45, 68.3) * mm, "end": v(30.67, 67.6) * mm});
            skArc(sketch, "E14.67.1", {"start": v(29.15, 70.39) * mm, "mid": v(29.1, 69.34) * mm, "end": v(29.11, 68.3) * mm});
            skPoint(sketch, "E14.67.2", {"position": v(33.1, 70.97) * mm});
            skPoint(sketch, "E14.67.3", {"position": v(30.48, 67.46) * mm});
            skLineSegment(sketch, "E14.67.4", {"start": v(32.19, 69.03) * mm, "end": v(32.95, 70.63) * mm});
            skLineSegment(sketch, "E14.67.5", {"start": v(29.15, 70.39) * mm, "end": v(29.83, 72) * mm});
            skPoint(sketch, "E14.67.6", {"position": v(29.12, 68.07) * mm});
            skLineSegment(sketch, "E14.67.7", {"start": v(30.27, 67.55) * mm, "end": v(29.8, 67.76) * mm});
            skLineSegment(sketch, "E14.67.8", {"start": v(29.33, 67.97) * mm, "end": v(29.8, 67.76) * mm});
            skArc(sketch, "E14.67.9", {"start": v(30.27, 67.55) * mm, "mid": v(30.48, 67.52) * mm, "end": v(30.67, 67.6) * mm});
            skArc(sketch, "E14.67.10", {"start": v(29.11, 68.3) * mm, "mid": v(29.18, 68.1) * mm, "end": v(29.33, 67.97) * mm});
            skArc(sketch, "E14.67.11", {"start": v(33.45, 70.81) * mm, "mid": v(33.16, 70.83) * mm, "end": v(32.95, 70.63) * mm});
            skArc(sketch, "E14.67.12", {"start": v(29.83, 72) * mm, "mid": v(29.83, 72.3) * mm, "end": v(29.63, 72.5) * mm});
            skArc(sketch, "E14.68.0", {"start": v(26.05, 71.57) * mm, "mid": v(25.37, 70.78) * mm, "end": v(24.66, 70.02) * mm});
            skArc(sketch, "E14.68.1", {"start": v(22.9, 72.66) * mm, "mid": v(22.95, 71.62) * mm, "end": v(23.05, 70.58) * mm});
            skPoint(sketch, "E14.68.2", {"position": v(26.8, 73.59) * mm});
            skPoint(sketch, "E14.68.3", {"position": v(24.49, 69.86) * mm});
            skLineSegment(sketch, "E14.68.4", {"start": v(26.05, 71.57) * mm, "end": v(26.67, 73.23) * mm});
            skLineSegment(sketch, "E14.68.5", {"start": v(22.9, 72.66) * mm, "end": v(23.44, 74.32) * mm});
            skPoint(sketch, "E14.68.6", {"position": v(23.08, 70.35) * mm});
            skLineSegment(sketch, "E14.68.7", {"start": v(24.27, 69.93) * mm, "end": v(23.78, 70.1) * mm});
            skLineSegment(sketch, "E14.68.8", {"start": v(23.3, 70.27) * mm, "end": v(23.78, 70.1) * mm});
            skArc(sketch, "E14.68.9", {"start": v(24.27, 69.93) * mm, "mid": v(24.47, 69.92) * mm, "end": v(24.66, 70.02) * mm});
            skArc(sketch, "E14.68.10", {"start": v(23.05, 70.58) * mm, "mid": v(23.13, 70.39) * mm, "end": v(23.3, 70.27) * mm});
            skArc(sketch, "E14.68.11", {"start": v(27.16, 73.46) * mm, "mid": v(26.86, 73.45) * mm, "end": v(26.67, 73.23) * mm});
            skArc(sketch, "E14.68.12", {"start": v(23.44, 74.32) * mm, "mid": v(23.42, 74.62) * mm, "end": v(23.2, 74.8) * mm});
            skArc(sketch, "E14.69.0", {"start": v(19.71, 73.57) * mm, "mid": v(19.1, 72.72) * mm, "end": v(18.46, 71.9) * mm});
            skArc(sketch, "E14.69.1", {"start": v(16.49, 74.38) * mm, "mid": v(16.62, 73.35) * mm, "end": v(16.8, 72.32) * mm});
            skPoint(sketch, "E14.69.2", {"position": v(20.28, 75.64) * mm});
            skPoint(sketch, "E14.69.3", {"position": v(18.3, 71.73) * mm});
            skLineSegment(sketch, "E14.69.4", {"start": v(19.71, 73.57) * mm, "end": v(20.18, 75.28) * mm});
            skLineSegment(sketch, "E14.69.5", {"start": v(16.49, 74.38) * mm, "end": v(16.88, 76.08) * mm});
            skPoint(sketch, "E14.69.6", {"position": v(16.86, 72.09) * mm});
            skLineSegment(sketch, "E14.69.7", {"start": v(18.08, 71.78) * mm, "end": v(17.58, 71.9) * mm});
            skLineSegment(sketch, "E14.69.8", {"start": v(17.09, 72.03) * mm, "end": v(17.58, 71.9) * mm});
            skArc(sketch, "E14.69.9", {"start": v(18.08, 71.78) * mm, "mid": v(18.29, 71.79) * mm, "end": v(18.46, 71.9) * mm});
            skArc(sketch, "E14.69.10", {"start": v(16.8, 72.32) * mm, "mid": v(16.9, 72.14) * mm, "end": v(17.09, 72.03) * mm});
            skArc(sketch, "E14.69.11", {"start": v(20.65, 75.55) * mm, "mid": v(20.36, 75.5) * mm, "end": v(20.18, 75.28) * mm});
            skArc(sketch, "E14.69.12", {"start": v(16.88, 76.08) * mm, "mid": v(16.83, 76.37) * mm, "end": v(16.59, 76.54) * mm});
            skArc(sketch, "E14.70.0", {"start": v(13.23, 75) * mm, "mid": v(12.7, 74.11) * mm, "end": v(12.12, 73.24) * mm});
            skArc(sketch, "E14.70.1", {"start": v(9.94, 75.53) * mm, "mid": v(10.17, 74.51) * mm, "end": v(10.44, 73.5) * mm});
            skPoint(sketch, "E14.70.2", {"position": v(13.61, 77.12) * mm});
            skPoint(sketch, "E14.70.3", {"position": v(11.99, 73.05) * mm});
            skLineSegment(sketch, "E14.70.4", {"start": v(13.23, 75) * mm, "end": v(13.54, 76.75) * mm});
            skLineSegment(sketch, "E14.70.5", {"start": v(9.94, 75.53) * mm, "end": v(10.18, 77.26) * mm});
            skPoint(sketch, "E14.70.6", {"position": v(10.51, 73.28) * mm});
            skLineSegment(sketch, "E14.70.7", {"start": v(11.75, 73.08) * mm, "end": v(11.25, 73.16) * mm});
            skLineSegment(sketch, "E14.70.8", {"start": v(10.74, 73.25) * mm, "end": v(11.25, 73.16) * mm});
            skArc(sketch, "E14.70.9", {"start": v(11.75, 73.08) * mm, "mid": v(11.96, 73.11) * mm, "end": v(12.12, 73.24) * mm});
            skArc(sketch, "E14.70.10", {"start": v(10.44, 73.5) * mm, "mid": v(10.56, 73.33) * mm, "end": v(10.74, 73.25) * mm});
            skArc(sketch, "E14.70.11", {"start": v(13.99, 77.06) * mm, "mid": v(13.7, 77) * mm, "end": v(13.54, 76.75) * mm});
            skArc(sketch, "E14.70.12", {"start": v(10.18, 77.26) * mm, "mid": v(10.1, 77.55) * mm, "end": v(9.85, 77.7) * mm});
            skArc(sketch, "E14.71.0", {"start": v(6.64, 75.88) * mm, "mid": v(6.2, 74.93) * mm, "end": v(5.7, 74.02) * mm});
            skArc(sketch, "E14.71.1", {"start": v(3.32, 76.11) * mm, "mid": v(3.63, 75.12) * mm, "end": v(4, 74.14) * mm});
            skPoint(sketch, "E14.71.2", {"position": v(6.84, 78.02) * mm});
            skPoint(sketch, "E14.71.3", {"position": v(5.57, 73.82) * mm});
            skLineSegment(sketch, "E14.71.4", {"start": v(6.64, 75.88) * mm, "end": v(6.8, 77.64) * mm});
            skLineSegment(sketch, "E14.71.5", {"start": v(3.32, 76.11) * mm, "end": v(3.4, 77.86) * mm});
            skPoint(sketch, "E14.71.6", {"position": v(4.09, 73.92) * mm});
            skLineSegment(sketch, "E14.71.7", {"start": v(5.34, 73.83) * mm, "end": v(4.83, 73.86) * mm});
            skLineSegment(sketch, "E14.71.8", {"start": v(4.32, 73.9) * mm, "end": v(4.83, 73.86) * mm});
            skArc(sketch, "E14.71.9", {"start": v(5.34, 73.83) * mm, "mid": v(5.54, 73.87) * mm, "end": v(5.7, 74.02) * mm});
            skArc(sketch, "E14.71.10", {"start": v(4, 74.14) * mm, "mid": v(4.12, 73.98) * mm, "end": v(4.32, 73.9) * mm});
            skArc(sketch, "E14.71.11", {"start": v(7.22, 77.98) * mm, "mid": v(6.94, 77.9) * mm, "end": v(6.8, 77.64) * mm});
            skArc(sketch, "E14.71.12", {"start": v(3.4, 77.86) * mm, "mid": v(3.3, 78.13) * mm, "end": v(3.04, 78.26) * mm});
            skArc(sketch, "E15.trimOffspring", {"start": v(3.04, 78.26) * mm, "mid": v(1.72, 78.3) * mm, "end": v(0.4, 78.32) * mm});
            skArc(sketch, "E16.trimOffspring", {"start": v(9.85, 77.7) * mm, "mid": v(8.35, 77.87) * mm, "end": v(6.84, 78.02) * mm});
            skArc(sketch, "E17.trimOffspring", {"start": v(16.59, 76.54) * mm, "mid": v(15.1, 76.85) * mm, "end": v(13.61, 77.12) * mm});
            skArc(sketch, "E18.trimOffspring", {"start": v(23.2, 74.8) * mm, "mid": v(21.74, 75.24) * mm, "end": v(20.28, 75.64) * mm});
            skArc(sketch, "E19.trimOffspring", {"start": v(29.63, 72.5) * mm, "mid": v(28.22, 73.06) * mm, "end": v(26.8, 73.59) * mm});
            skArc(sketch, "E20.trimOffspring", {"start": v(35.83, 69.64) * mm, "mid": v(34.48, 70.32) * mm, "end": v(33.1, 70.97) * mm});
            skArc(sketch, "E21.trimOffspring", {"start": v(41.76, 66.25) * mm, "mid": v(40.47, 67.05) * mm, "end": v(39.17, 67.82) * mm});
            skArc(sketch, "E22.trimOffspring", {"start": v(47.38, 62.36) * mm, "mid": v(46.16, 63.26) * mm, "end": v(44.93, 64.15) * mm});
            skArc(sketch, "E23.trimOffspring", {"start": v(52.63, 58) * mm, "mid": v(51.5, 59) * mm, "end": v(50.35, 59.99) * mm});
            skArc(sketch, "E24.trimOffspring", {"start": v(57.49, 53.18) * mm, "mid": v(56.45, 54.29) * mm, "end": v(55.39, 55.37) * mm});
            skArc(sketch, "E25.trimOffspring", {"start": v(61.9, 47.97) * mm, "mid": v(60.96, 49.16) * mm, "end": v(60, 50.33) * mm});
            skArc(sketch, "E26.trimOffspring", {"start": v(65.85, 42.4) * mm, "mid": v(65.02, 43.66) * mm, "end": v(64.16, 44.91) * mm});
            skArc(sketch, "E27.trimOffspring", {"start": v(69.3, 36.5) * mm, "mid": v(68.58, 37.83) * mm, "end": v(67.83, 39.15) * mm});
            skArc(sketch, "E28.trimOffspring", {"start": v(72.21, 30.31) * mm, "mid": v(71.61, 31.7) * mm, "end": v(70.98, 33.09) * mm});
            skArc(sketch, "E29.trimOffspring", {"start": v(74.58, 23.9) * mm, "mid": v(74.1, 25.34) * mm, "end": v(73.6, 26.77) * mm});
            skArc(sketch, "E30.trimOffspring", {"start": v(76.38, 17.32) * mm, "mid": v(76.03, 18.79) * mm, "end": v(75.65, 20.26) * mm});
            skArc(sketch, "E31.trimOffspring", {"start": v(77.6, 10.6) * mm, "mid": v(77.38, 12.1) * mm, "end": v(77.13, 13.59) * mm});
            skArc(sketch, "E32.trimOffspring", {"start": v(78.22, 3.79) * mm, "mid": v(78.14, 5.3) * mm, "end": v(78.02, 6.81) * mm});
            skArc(sketch, "E33.trimOffspring", {"start": v(78.26, -3.04) * mm, "mid": v(78.3, -1.53) * mm, "end": v(78.32, -0.01) * mm});
            skArc(sketch, "E34.trimOffspring", {"start": v(77.7, -9.85) * mm, "mid": v(77.87, -8.35) * mm, "end": v(78.02, -6.84) * mm});
            skArc(sketch, "E35.trimOffspring", {"start": v(76.54, -16.59) * mm, "mid": v(76.85, -15.1) * mm, "end": v(77.12, -13.61) * mm});
            skArc(sketch, "E36.trimOffspring", {"start": v(74.8, -23.2) * mm, "mid": v(75.24, -21.74) * mm, "end": v(75.64, -20.28) * mm});
            skArc(sketch, "E37.trimOffspring", {"start": v(72.5, -29.63) * mm, "mid": v(73.06, -28.22) * mm, "end": v(73.59, -26.8) * mm});
            skArc(sketch, "E38.trimOffspring", {"start": v(69.64, -35.83) * mm, "mid": v(70.32, -34.48) * mm, "end": v(70.97, -33.1) * mm});
            skArc(sketch, "E39.trimOffspring", {"start": v(66.25, -41.76) * mm, "mid": v(67.05, -40.47) * mm, "end": v(67.82, -39.17) * mm});
            skArc(sketch, "E40.trimOffspring", {"start": v(62.36, -47.38) * mm, "mid": v(63.26, -46.16) * mm, "end": v(64.15, -44.93) * mm});
            skArc(sketch, "E41.trimOffspring", {"start": v(58, -52.63) * mm, "mid": v(59, -51.5) * mm, "end": v(59.99, -50.35) * mm});
            skArc(sketch, "E42.trimOffspring", {"start": v(53.18, -57.49) * mm, "mid": v(54.29, -56.45) * mm, "end": v(55.37, -55.39) * mm});
            skArc(sketch, "E43.trimOffspring", {"start": v(47.97, -61.9) * mm, "mid": v(49.16, -60.96) * mm, "end": v(50.33, -60) * mm});
            skArc(sketch, "E44.trimOffspring", {"start": v(42.4, -65.85) * mm, "mid": v(43.66, -65.02) * mm, "end": v(44.91, -64.16) * mm});
            skArc(sketch, "E45.trimOffspring", {"start": v(36.5, -69.3) * mm, "mid": v(37.83, -68.58) * mm, "end": v(39.15, -67.83) * mm});
            skArc(sketch, "E46.trimOffspring", {"start": v(30.31, -72.21) * mm, "mid": v(31.7, -71.61) * mm, "end": v(33.09, -70.98) * mm});
            skArc(sketch, "E47.trimOffspring", {"start": v(23.9, -74.58) * mm, "mid": v(25.34, -74.1) * mm, "end": v(26.77, -73.6) * mm});
            skArc(sketch, "E48.trimOffspring", {"start": v(17.32, -76.38) * mm, "mid": v(18.79, -76.03) * mm, "end": v(20.26, -75.65) * mm});
            skArc(sketch, "E49.trimOffspring", {"start": v(10.6, -77.6) * mm, "mid": v(12.1, -77.38) * mm, "end": v(13.59, -77.13) * mm});
            skArc(sketch, "E50.trimOffspring", {"start": v(3.79, -78.22) * mm, "mid": v(5.3, -78.14) * mm, "end": v(6.81, -78.02) * mm});
            skArc(sketch, "E51.trimOffspring", {"start": v(-3.04, -78.26) * mm, "mid": v(-1.53, -78.3) * mm, "end": v(-0.01, -78.32) * mm});
            skArc(sketch, "E52.trimOffspring", {"start": v(-9.85, -77.7) * mm, "mid": v(-8.35, -77.87) * mm, "end": v(-6.84, -78.02) * mm});
            skArc(sketch, "E53.trimOffspring", {"start": v(-16.59, -76.54) * mm, "mid": v(-15.1, -76.85) * mm, "end": v(-13.61, -77.12) * mm});
            skArc(sketch, "E54.trimOffspring", {"start": v(-23.2, -74.8) * mm, "mid": v(-21.74, -75.24) * mm, "end": v(-20.28, -75.64) * mm});
            skArc(sketch, "E55.trimOffspring", {"start": v(-29.63, -72.5) * mm, "mid": v(-28.22, -73.06) * mm, "end": v(-26.8, -73.59) * mm});
            skArc(sketch, "E56.trimOffspring", {"start": v(-35.83, -69.64) * mm, "mid": v(-34.48, -70.32) * mm, "end": v(-33.1, -70.97) * mm});
            skArc(sketch, "E57.trimOffspring", {"start": v(-41.76, -66.25) * mm, "mid": v(-40.47, -67.05) * mm, "end": v(-39.17, -67.82) * mm});
            skArc(sketch, "E58.trimOffspring", {"start": v(-47.38, -62.36) * mm, "mid": v(-46.16, -63.26) * mm, "end": v(-44.93, -64.15) * mm});
            skArc(sketch, "E59.trimOffspring", {"start": v(-52.63, -58) * mm, "mid": v(-51.5, -59) * mm, "end": v(-50.35, -59.99) * mm});
            skArc(sketch, "E60.trimOffspring", {"start": v(-57.49, -53.18) * mm, "mid": v(-56.45, -54.29) * mm, "end": v(-55.39, -55.37) * mm});
            skArc(sketch, "E61.trimOffspring", {"start": v(-61.9, -47.97) * mm, "mid": v(-60.96, -49.16) * mm, "end": v(-60, -50.33) * mm});
            skArc(sketch, "E62.trimOffspring", {"start": v(-65.85, -42.4) * mm, "mid": v(-65.02, -43.66) * mm, "end": v(-64.16, -44.91) * mm});
            skArc(sketch, "E63.trimOffspring", {"start": v(-69.3, -36.5) * mm, "mid": v(-68.58, -37.83) * mm, "end": v(-67.83, -39.15) * mm});
            skArc(sketch, "E64.trimOffspring", {"start": v(-72.21, -30.31) * mm, "mid": v(-71.69, -31.53) * mm, "end": v(-71.14, -32.74) * mm});
            skArc(sketch, "E65.trimOffspring", {"start": v(-74.58, -23.9) * mm, "mid": v(-74.1, -25.34) * mm, "end": v(-73.6, -26.77) * mm});
            skArc(sketch, "E66.trimOffspring", {"start": v(-76.38, -17.32) * mm, "mid": v(-76.03, -18.79) * mm, "end": v(-75.65, -20.26) * mm});
            skArc(sketch, "E67.trimOffspring", {"start": v(-77.6, -10.6) * mm, "mid": v(-77.38, -12.1) * mm, "end": v(-77.13, -13.59) * mm});
            skArc(sketch, "E68.trimOffspring", {"start": v(-78.22, -3.79) * mm, "mid": v(-78.14, -5.3) * mm, "end": v(-78.02, -6.81) * mm});
            skArc(sketch, "E69.trimOffspring", {"start": v(-78.26, 3.04) * mm, "mid": v(-78.3, 1.53) * mm, "end": v(-78.32, 0.01) * mm});
            skArc(sketch, "E70.trimOffspring", {"start": v(-77.7, 9.85) * mm, "mid": v(-77.87, 8.35) * mm, "end": v(-78.02, 6.84) * mm});
            skArc(sketch, "E71.trimOffspring", {"start": v(-76.54, 16.59) * mm, "mid": v(-76.85, 15.1) * mm, "end": v(-77.12, 13.61) * mm});
            skArc(sketch, "E72.trimOffspring", {"start": v(-74.8, 23.2) * mm, "mid": v(-75.24, 21.74) * mm, "end": v(-75.64, 20.28) * mm});
            skArc(sketch, "E73.trimOffspring", {"start": v(-72.5, 29.63) * mm, "mid": v(-73.06, 28.22) * mm, "end": v(-73.59, 26.8) * mm});
            skArc(sketch, "E74.trimOffspring", {"start": v(-69.64, 35.83) * mm, "mid": v(-70.32, 34.48) * mm, "end": v(-70.97, 33.1) * mm});
            skArc(sketch, "E75.trimOffspring", {"start": v(-66.25, 41.76) * mm, "mid": v(-67.05, 40.47) * mm, "end": v(-67.82, 39.17) * mm});
            skArc(sketch, "E76.trimOffspring", {"start": v(-62.36, 47.38) * mm, "mid": v(-63.26, 46.16) * mm, "end": v(-64.15, 44.93) * mm});
            skArc(sketch, "E77.trimOffspring", {"start": v(-58, 52.63) * mm, "mid": v(-59, 51.5) * mm, "end": v(-59.99, 50.35) * mm});
            skArc(sketch, "E78.trimOffspring", {"start": v(-53.18, 57.49) * mm, "mid": v(-54.29, 56.45) * mm, "end": v(-55.37, 55.39) * mm});
            skArc(sketch, "E79.trimOffspring", {"start": v(-47.97, 61.9) * mm, "mid": v(-49.16, 60.96) * mm, "end": v(-50.33, 60) * mm});
            skArc(sketch, "E80.trimOffspring", {"start": v(-42.4, 65.85) * mm, "mid": v(-43.66, 65.02) * mm, "end": v(-44.91, 64.16) * mm});
            skArc(sketch, "E81.trimOffspring", {"start": v(-36.5, 69.3) * mm, "mid": v(-37.83, 68.58) * mm, "end": v(-39.15, 67.83) * mm});
            skArc(sketch, "E82.trimOffspring", {"start": v(-30.31, 72.21) * mm, "mid": v(-31.7, 71.61) * mm, "end": v(-33.09, 70.98) * mm});
            skArc(sketch, "E83.trimOffspring", {"start": v(-23.9, 74.58) * mm, "mid": v(-25.34, 74.1) * mm, "end": v(-26.77, 73.6) * mm});
            skArc(sketch, "E84.trimOffspring", {"start": v(-17.32, 76.38) * mm, "mid": v(-18.79, 76.03) * mm, "end": v(-20.26, 75.65) * mm});
            skArc(sketch, "E85.trimOffspring", {"start": v(-10.6, 77.6) * mm, "mid": v(-12.1, 77.38) * mm, "end": v(-13.59, 77.13) * mm});
            skSolve(sketch);
        }
        {
            var Q0;
            Q0 = qSketchRegion(id + "F0", true);
            extrude(context, id + "F1", {"entities" : qUnion([Q0]), "depth" : 12.7 * mm});
        }
        {
            var Q0;
            Q0=qCreatedBy(makeId("Front.planeOp"),FACE);
            var sketch = newSketch(context, id + "F2", { "sketchPlane" : qUnion([Q0])});
            skCircle(sketch, "E86", {"center": v(0, 0) * mm, "radius": 84.28 * mm});
            skSolve(sketch);
        }
        {
            var Q0;
            Q0 = qSketchRegion(id + "F2", true);
            extrude(context, id + "F3", {"entities" : qUnion([Q0]), "operationType" : NewBodyOperationType.ADD, "oppositeDirection" : true, "depth" : 6.35 * mm});
        }
        {
            var Q0;
            Q0=makeQuery(id+"F3.boolean.opBoolean","SPLIT",FACE,{"disambiguationData":[TD([makeQuery(id+"F1.opExtrude","SWEPT_FACE",FACE,{"disambiguationData":[OSD([sQuery(id+"F0.wireOp",EDGE,"E0")])]})])],"derivedFrom":makeQuery(id+"F3.opExtrude","CAP_FACE",FACE,{"disambiguationData":[OSD([sQuery(id+"F2.wireOp",EDGE,"E86")])],"isStart":true})});
            var sketch = newSketch(context, id + "F4", { "sketchPlane" : qUnion([Q0])});
            skCircle(sketch, "E87", {"center": v(0, 0) * mm, "radius": 3.18 * mm});
            skSolve(sketch);
        }
        {
            var Q0;
            Q0 = qSketchRegion(id + "F4", true);
            extrude(context, id + "F5", {"entities" : qUnion([Q0]), "operationType" : NewBodyOperationType.ADD, "depth" : 12.7 * mm});
        }
        {
            var Q0;
            Q0=makeQuery(id+"F3.boolean.opBoolean","SPLIT",FACE,{"disambiguationData":[TD([makeQuery(id+"F1.opExtrude","SWEPT_FACE",FACE,{"disambiguationData":[OSD([sQuery(id+"F0.wireOp",EDGE,"E0")])]})])],"derivedFrom":makeQuery(id+"F3.opExtrude","CAP_FACE",FACE,{"disambiguationData":[OSD([sQuery(id+"F2.wireOp",EDGE,"E86")])],"isStart":true})});
            var sketch = newSketch(context, id + "F6", { "sketchPlane" : qUnion([Q0])});
            skCircle(sketch, "E88", {"center": v(0, 0) * mm, "radius": 27.38 * mm});
            skCircle(sketch, "E89", {"center": v(-27.38, 0) * mm, "radius": 23.5 * mm});
            skCircle(sketch, "E90", {"center": v(-50.88, 0) * mm, "radius": 27.38 * mm});
            skPoint(sketch, "E91.1.0", {"position": v(25.44, -44.06) * mm});
            skPoint(sketch, "E91.2.0", {"position": v(25.44, 44.06) * mm});
            skSolve(sketch);
        }
        {
            var Q0;
            Q0=sQuery(id+"F6.wireOp",VERTEX,"E90.center");
            var Q1;
            Q1=sQuery(id+"F6.wireOp",VERTEX,"E91.2.0");
            var Q2;
            Q2=sQuery(id+"F6.wireOp",VERTEX,"E91.1.0");
            var Q3;
            Q3=makeQuery(id+"F1.opExtrude","SWEPT_BODY",BODY,{"disambiguationData":[OSD([sQuery(id+"F0.wireOp",EDGE,"E0"),sQuery(id+"F0.wireOp",EDGE,"E3.MirrorCS"),sQuery(id+"F0.wireOp",EDGE,"E4.MirrorCS"),sQuery(id+"F0.wireOp",EDGE,"E5.MirrorCS"),sQuery(id+"F0.wireOp",EDGE,"E6.MirrorCS"),sQuery(id+"F0.wireOp",EDGE,"E7"),sQuery(id+"F0.wireOp",EDGE,"E8"),sQuery(id+"F0.wireOp",EDGE,"E9"),sQuery(id+"F0.wireOp",EDGE,"E10.filletArc"),sQuery(id+"F0.wireOp",EDGE,"E11.filletArc"),sQuery(id+"F0.wireOp",EDGE,"E12.filletArc"),sQuery(id+"F0.wireOp",EDGE,"E13.filletArc"),sQuery(id+"F0.wireOp",EDGE,"E14.1.0"),sQuery(id+"F0.wireOp",EDGE,"E14.1.1"),sQuery(id+"F0.wireOp",EDGE,"E14.1.4"),sQuery(id+"F0.wireOp",EDGE,"E14.1.5"),sQuery(id+"F0.wireOp",EDGE,"E14.1.7"),sQuery(id+"F0.wireOp",EDGE,"E14.1.8"),sQuery(id+"F0.wireOp",EDGE,"E14.1.9"),sQuery(id+"F0.wireOp",EDGE,"E14.1.10"),sQuery(id+"F0.wireOp",EDGE,"E14.1.11"),sQuery(id+"F0.wireOp",EDGE,"E14.1.12"),sQuery(id+"F0.wireOp",EDGE,"E14.2.0"),sQuery(id+"F0.wireOp",EDGE,"E14.2.1"),sQuery(id+"F0.wireOp",EDGE,"E14.2.4"),sQuery(id+"F0.wireOp",EDGE,"E14.2.5"),sQuery(id+"F0.wireOp",EDGE,"E14.2.7"),sQuery(id+"F0.wireOp",EDGE,"E14.2.8"),sQuery(id+"F0.wireOp",EDGE,"E14.2.9"),sQuery(id+"F0.wireOp",EDGE,"E14.2.10"),sQuery(id+"F0.wireOp",EDGE,"E14.2.11"),sQuery(id+"F0.wireOp",EDGE,"E14.2.12"),sQuery(id+"F0.wireOp",EDGE,"E14.3.0"),sQuery(id+"F0.wireOp",EDGE,"E14.3.1"),sQuery(id+"F0.wireOp",EDGE,"E14.3.4"),sQuery(id+"F0.wireOp",EDGE,"E14.3.5"),sQuery(id+"F0.wireOp",EDGE,"E14.3.7"),sQuery(id+"F0.wireOp",EDGE,"E14.3.8"),sQuery(id+"F0.wireOp",EDGE,"E14.3.9"),sQuery(id+"F0.wireOp",EDGE,"E14.3.10"),sQuery(id+"F0.wireOp",EDGE,"E14.3.11"),sQuery(id+"F0.wireOp",EDGE,"E14.3.12"),sQuery(id+"F0.wireOp",EDGE,"E14.4.0"),sQuery(id+"F0.wireOp",EDGE,"E14.4.1"),sQuery(id+"F0.wireOp",EDGE,"E14.4.4"),sQuery(id+"F0.wireOp",EDGE,"E14.4.5"),sQuery(id+"F0.wireOp",EDGE,"E14.4.7"),sQuery(id+"F0.wireOp",EDGE,"E14.4.8"),sQuery(id+"F0.wireOp",EDGE,"E14.4.9"),sQuery(id+"F0.wireOp",EDGE,"E14.4.10"),sQuery(id+"F0.wireOp",EDGE,"E14.4.11"),sQuery(id+"F0.wireOp",EDGE,"E14.4.12"),sQuery(id+"F0.wireOp",EDGE,"E14.5.0"),sQuery(id+"F0.wireOp",EDGE,"E14.5.1"),sQuery(id+"F0.wireOp",EDGE,"E14.5.4"),sQuery(id+"F0.wireOp",EDGE,"E14.5.5"),sQuery(id+"F0.wireOp",EDGE,"E14.5.7"),sQuery(id+"F0.wireOp",EDGE,"E14.5.8"),sQuery(id+"F0.wireOp",EDGE,"E14.5.9"),sQuery(id+"F0.wireOp",EDGE,"E14.5.10"),sQuery(id+"F0.wireOp",EDGE,"E14.5.11"),sQuery(id+"F0.wireOp",EDGE,"E14.5.12"),sQuery(id+"F0.wireOp",EDGE,"E14.6.0"),sQuery(id+"F0.wireOp",EDGE,"E14.6.1"),sQuery(id+"F0.wireOp",EDGE,"E14.6.4"),sQuery(id+"F0.wireOp",EDGE,"E14.6.5"),sQuery(id+"F0.wireOp",EDGE,"E14.6.7"),sQuery(id+"F0.wireOp",EDGE,"E14.6.8"),sQuery(id+"F0.wireOp",EDGE,"E14.6.9"),sQuery(id+"F0.wireOp",EDGE,"E14.6.10"),sQuery(id+"F0.wireOp",EDGE,"E14.6.11"),sQuery(id+"F0.wireOp",EDGE,"E14.6.12"),sQuery(id+"F0.wireOp",EDGE,"E14.7.0"),sQuery(id+"F0.wireOp",EDGE,"E14.7.1"),sQuery(id+"F0.wireOp",EDGE,"E14.7.4"),sQuery(id+"F0.wireOp",EDGE,"E14.7.5"),sQuery(id+"F0.wireOp",EDGE,"E14.7.7"),sQuery(id+"F0.wireOp",EDGE,"E14.7.8"),sQuery(id+"F0.wireOp",EDGE,"E14.7.9"),sQuery(id+"F0.wireOp",EDGE,"E14.7.10"),sQuery(id+"F0.wireOp",EDGE,"E14.7.11"),sQuery(id+"F0.wireOp",EDGE,"E14.7.12"),sQuery(id+"F0.wireOp",EDGE,"E14.8.0"),sQuery(id+"F0.wireOp",EDGE,"E14.8.1"),sQuery(id+"F0.wireOp",EDGE,"E14.8.4"),sQuery(id+"F0.wireOp",EDGE,"E14.8.5"),sQuery(id+"F0.wireOp",EDGE,"E14.8.7"),sQuery(id+"F0.wireOp",EDGE,"E14.8.8"),sQuery(id+"F0.wireOp",EDGE,"E14.8.9"),sQuery(id+"F0.wireOp",EDGE,"E14.8.10"),sQuery(id+"F0.wireOp",EDGE,"E14.8.11"),sQuery(id+"F0.wireOp",EDGE,"E14.8.12"),sQuery(id+"F0.wireOp",EDGE,"E14.9.0"),sQuery(id+"F0.wireOp",EDGE,"E14.9.1"),sQuery(id+"F0.wireOp",EDGE,"E14.9.4"),sQuery(id+"F0.wireOp",EDGE,"E14.9.5"),sQuery(id+"F0.wireOp",EDGE,"E14.9.7"),sQuery(id+"F0.wireOp",EDGE,"E14.9.8"),sQuery(id+"F0.wireOp",EDGE,"E14.9.9"),sQuery(id+"F0.wireOp",EDGE,"E14.9.10"),sQuery(id+"F0.wireOp",EDGE,"E14.9.11"),sQuery(id+"F0.wireOp",EDGE,"E14.9.12"),sQuery(id+"F0.wireOp",EDGE,"E14.10.0"),sQuery(id+"F0.wireOp",EDGE,"E14.10.1"),sQuery(id+"F0.wireOp",EDGE,"E14.10.4"),sQuery(id+"F0.wireOp",EDGE,"E14.10.5"),sQuery(id+"F0.wireOp",EDGE,"E14.10.7"),sQuery(id+"F0.wireOp",EDGE,"E14.10.8"),sQuery(id+"F0.wireOp",EDGE,"E14.10.9"),sQuery(id+"F0.wireOp",EDGE,"E14.10.10"),sQuery(id+"F0.wireOp",EDGE,"E14.10.11"),sQuery(id+"F0.wireOp",EDGE,"E14.10.12"),sQuery(id+"F0.wireOp",EDGE,"E14.11.0"),sQuery(id+"F0.wireOp",EDGE,"E14.11.1"),sQuery(id+"F0.wireOp",EDGE,"E14.11.4"),sQuery(id+"F0.wireOp",EDGE,"E14.11.5"),sQuery(id+"F0.wireOp",EDGE,"E14.11.7"),sQuery(id+"F0.wireOp",EDGE,"E14.11.8"),sQuery(id+"F0.wireOp",EDGE,"E14.11.9"),sQuery(id+"F0.wireOp",EDGE,"E14.11.10"),sQuery(id+"F0.wireOp",EDGE,"E14.11.11"),sQuery(id+"F0.wireOp",EDGE,"E14.11.12"),sQuery(id+"F0.wireOp",EDGE,"E14.12.0"),sQuery(id+"F0.wireOp",EDGE,"E14.12.1"),sQuery(id+"F0.wireOp",EDGE,"E14.12.4"),sQuery(id+"F0.wireOp",EDGE,"E14.12.5"),sQuery(id+"F0.wireOp",EDGE,"E14.12.7"),sQuery(id+"F0.wireOp",EDGE,"E14.12.8"),sQuery(id+"F0.wireOp",EDGE,"E14.12.9"),sQuery(id+"F0.wireOp",EDGE,"E14.12.10"),sQuery(id+"F0.wireOp",EDGE,"E14.12.11"),sQuery(id+"F0.wireOp",EDGE,"E14.12.12"),sQuery(id+"F0.wireOp",EDGE,"E14.13.0"),sQuery(id+"F0.wireOp",EDGE,"E14.13.1"),sQuery(id+"F0.wireOp",EDGE,"E14.13.4"),sQuery(id+"F0.wireOp",EDGE,"E14.13.5"),sQuery(id+"F0.wireOp",EDGE,"E14.13.7"),sQuery(id+"F0.wireOp",EDGE,"E14.13.8"),sQuery(id+"F0.wireOp",EDGE,"E14.13.9"),sQuery(id+"F0.wireOp",EDGE,"E14.13.10"),sQuery(id+"F0.wireOp",EDGE,"E14.13.11"),sQuery(id+"F0.wireOp",EDGE,"E14.13.12"),sQuery(id+"F0.wireOp",EDGE,"E14.14.0"),sQuery(id+"F0.wireOp",EDGE,"E14.14.1"),sQuery(id+"F0.wireOp",EDGE,"E14.14.4"),sQuery(id+"F0.wireOp",EDGE,"E14.14.5"),sQuery(id+"F0.wireOp",EDGE,"E14.14.7"),sQuery(id+"F0.wireOp",EDGE,"E14.14.8"),sQuery(id+"F0.wireOp",EDGE,"E14.14.9"),sQuery(id+"F0.wireOp",EDGE,"E14.14.10"),sQuery(id+"F0.wireOp",EDGE,"E14.14.11"),sQuery(id+"F0.wireOp",EDGE,"E14.14.12"),sQuery(id+"F0.wireOp",EDGE,"E14.15.0"),sQuery(id+"F0.wireOp",EDGE,"E14.15.1"),sQuery(id+"F0.wireOp",EDGE,"E14.15.4"),sQuery(id+"F0.wireOp",EDGE,"E14.15.5"),sQuery(id+"F0.wireOp",EDGE,"E14.15.7"),sQuery(id+"F0.wireOp",EDGE,"E14.15.8"),sQuery(id+"F0.wireOp",EDGE,"E14.15.9"),sQuery(id+"F0.wireOp",EDGE,"E14.15.10"),sQuery(id+"F0.wireOp",EDGE,"E14.15.11"),sQuery(id+"F0.wireOp",EDGE,"E14.15.12"),sQuery(id+"F0.wireOp",EDGE,"E14.16.0"),sQuery(id+"F0.wireOp",EDGE,"E14.16.1"),sQuery(id+"F0.wireOp",EDGE,"E14.16.4"),sQuery(id+"F0.wireOp",EDGE,"E14.16.5"),sQuery(id+"F0.wireOp",EDGE,"E14.16.7"),sQuery(id+"F0.wireOp",EDGE,"E14.16.8"),sQuery(id+"F0.wireOp",EDGE,"E14.16.9"),sQuery(id+"F0.wireOp",EDGE,"E14.16.10"),sQuery(id+"F0.wireOp",EDGE,"E14.16.11"),sQuery(id+"F0.wireOp",EDGE,"E14.16.12"),sQuery(id+"F0.wireOp",EDGE,"E14.17.0"),sQuery(id+"F0.wireOp",EDGE,"E14.17.1"),sQuery(id+"F0.wireOp",EDGE,"E14.17.4"),sQuery(id+"F0.wireOp",EDGE,"E14.17.5"),sQuery(id+"F0.wireOp",EDGE,"E14.17.7"),sQuery(id+"F0.wireOp",EDGE,"E14.17.8"),sQuery(id+"F0.wireOp",EDGE,"E14.17.9"),sQuery(id+"F0.wireOp",EDGE,"E14.17.10"),sQuery(id+"F0.wireOp",EDGE,"E14.17.11"),sQuery(id+"F0.wireOp",EDGE,"E14.17.12"),sQuery(id+"F0.wireOp",EDGE,"E14.18.0"),sQuery(id+"F0.wireOp",EDGE,"E14.18.1"),sQuery(id+"F0.wireOp",EDGE,"E14.18.4"),sQuery(id+"F0.wireOp",EDGE,"E14.18.5"),sQuery(id+"F0.wireOp",EDGE,"E14.18.7"),sQuery(id+"F0.wireOp",EDGE,"E14.18.8"),sQuery(id+"F0.wireOp",EDGE,"E14.18.9"),sQuery(id+"F0.wireOp",EDGE,"E14.18.10"),sQuery(id+"F0.wireOp",EDGE,"E14.18.11"),sQuery(id+"F0.wireOp",EDGE,"E14.18.12"),sQuery(id+"F0.wireOp",EDGE,"E14.19.0"),sQuery(id+"F0.wireOp",EDGE,"E14.19.1"),sQuery(id+"F0.wireOp",EDGE,"E14.19.4"),sQuery(id+"F0.wireOp",EDGE,"E14.19.5"),sQuery(id+"F0.wireOp",EDGE,"E14.19.7"),sQuery(id+"F0.wireOp",EDGE,"E14.19.8"),sQuery(id+"F0.wireOp",EDGE,"E14.19.9"),sQuery(id+"F0.wireOp",EDGE,"E14.19.10"),sQuery(id+"F0.wireOp",EDGE,"E14.19.11"),sQuery(id+"F0.wireOp",EDGE,"E14.19.12"),sQuery(id+"F0.wireOp",EDGE,"E14.20.0"),sQuery(id+"F0.wireOp",EDGE,"E14.20.1"),sQuery(id+"F0.wireOp",EDGE,"E14.20.4"),sQuery(id+"F0.wireOp",EDGE,"E14.20.5"),sQuery(id+"F0.wireOp",EDGE,"E14.20.7"),sQuery(id+"F0.wireOp",EDGE,"E14.20.8"),sQuery(id+"F0.wireOp",EDGE,"E14.20.9"),sQuery(id+"F0.wireOp",EDGE,"E14.20.10"),sQuery(id+"F0.wireOp",EDGE,"E14.20.11"),sQuery(id+"F0.wireOp",EDGE,"E14.20.12"),sQuery(id+"F0.wireOp",EDGE,"E14.21.0"),sQuery(id+"F0.wireOp",EDGE,"E14.21.1"),sQuery(id+"F0.wireOp",EDGE,"E14.21.4"),sQuery(id+"F0.wireOp",EDGE,"E14.21.5"),sQuery(id+"F0.wireOp",EDGE,"E14.21.7"),sQuery(id+"F0.wireOp",EDGE,"E14.21.8"),sQuery(id+"F0.wireOp",EDGE,"E14.21.9"),sQuery(id+"F0.wireOp",EDGE,"E14.21.10"),sQuery(id+"F0.wireOp",EDGE,"E14.21.11"),sQuery(id+"F0.wireOp",EDGE,"E14.21.12"),sQuery(id+"F0.wireOp",EDGE,"E14.22.0"),sQuery(id+"F0.wireOp",EDGE,"E14.22.1"),sQuery(id+"F0.wireOp",EDGE,"E14.22.4"),sQuery(id+"F0.wireOp",EDGE,"E14.22.5"),sQuery(id+"F0.wireOp",EDGE,"E14.22.7"),sQuery(id+"F0.wireOp",EDGE,"E14.22.8"),sQuery(id+"F0.wireOp",EDGE,"E14.22.9"),sQuery(id+"F0.wireOp",EDGE,"E14.22.10"),sQuery(id+"F0.wireOp",EDGE,"E14.22.11"),sQuery(id+"F0.wireOp",EDGE,"E14.22.12"),sQuery(id+"F0.wireOp",EDGE,"E14.23.0"),sQuery(id+"F0.wireOp",EDGE,"E14.23.1"),sQuery(id+"F0.wireOp",EDGE,"E14.23.4"),sQuery(id+"F0.wireOp",EDGE,"E14.23.5"),sQuery(id+"F0.wireOp",EDGE,"E14.23.7"),sQuery(id+"F0.wireOp",EDGE,"E14.23.8"),sQuery(id+"F0.wireOp",EDGE,"E14.23.9"),sQuery(id+"F0.wireOp",EDGE,"E14.23.10"),sQuery(id+"F0.wireOp",EDGE,"E14.23.11"),sQuery(id+"F0.wireOp",EDGE,"E14.23.12"),sQuery(id+"F0.wireOp",EDGE,"E14.24.0"),sQuery(id+"F0.wireOp",EDGE,"E14.24.1"),sQuery(id+"F0.wireOp",EDGE,"E14.24.4"),sQuery(id+"F0.wireOp",EDGE,"E14.24.5"),sQuery(id+"F0.wireOp",EDGE,"E14.24.7"),sQuery(id+"F0.wireOp",EDGE,"E14.24.8"),sQuery(id+"F0.wireOp",EDGE,"E14.24.9"),sQuery(id+"F0.wireOp",EDGE,"E14.24.10"),sQuery(id+"F0.wireOp",EDGE,"E14.24.11"),sQuery(id+"F0.wireOp",EDGE,"E14.24.12"),sQuery(id+"F0.wireOp",EDGE,"E14.25.0"),sQuery(id+"F0.wireOp",EDGE,"E14.25.1"),sQuery(id+"F0.wireOp",EDGE,"E14.25.4"),sQuery(id+"F0.wireOp",EDGE,"E14.25.5"),sQuery(id+"F0.wireOp",EDGE,"E14.25.7"),sQuery(id+"F0.wireOp",EDGE,"E14.25.8"),sQuery(id+"F0.wireOp",EDGE,"E14.25.9"),sQuery(id+"F0.wireOp",EDGE,"E14.25.10"),sQuery(id+"F0.wireOp",EDGE,"E14.25.11"),sQuery(id+"F0.wireOp",EDGE,"E14.25.12"),sQuery(id+"F0.wireOp",EDGE,"E14.26.0"),sQuery(id+"F0.wireOp",EDGE,"E14.26.1"),sQuery(id+"F0.wireOp",EDGE,"E14.26.4"),sQuery(id+"F0.wireOp",EDGE,"E14.26.5"),sQuery(id+"F0.wireOp",EDGE,"E14.26.7"),sQuery(id+"F0.wireOp",EDGE,"E14.26.8"),sQuery(id+"F0.wireOp",EDGE,"E14.26.9"),sQuery(id+"F0.wireOp",EDGE,"E14.26.10"),sQuery(id+"F0.wireOp",EDGE,"E14.26.11"),sQuery(id+"F0.wireOp",EDGE,"E14.26.12"),sQuery(id+"F0.wireOp",EDGE,"E14.27.0"),sQuery(id+"F0.wireOp",EDGE,"E14.27.1"),sQuery(id+"F0.wireOp",EDGE,"E14.27.4"),sQuery(id+"F0.wireOp",EDGE,"E14.27.5"),sQuery(id+"F0.wireOp",EDGE,"E14.27.7"),sQuery(id+"F0.wireOp",EDGE,"E14.27.8"),sQuery(id+"F0.wireOp",EDGE,"E14.27.9"),sQuery(id+"F0.wireOp",EDGE,"E14.27.10"),sQuery(id+"F0.wireOp",EDGE,"E14.27.11"),sQuery(id+"F0.wireOp",EDGE,"E14.27.12"),sQuery(id+"F0.wireOp",EDGE,"E14.28.0"),sQuery(id+"F0.wireOp",EDGE,"E14.28.1"),sQuery(id+"F0.wireOp",EDGE,"E14.28.4"),sQuery(id+"F0.wireOp",EDGE,"E14.28.5"),sQuery(id+"F0.wireOp",EDGE,"E14.28.7"),sQuery(id+"F0.wireOp",EDGE,"E14.28.8"),sQuery(id+"F0.wireOp",EDGE,"E14.28.9"),sQuery(id+"F0.wireOp",EDGE,"E14.28.10"),sQuery(id+"F0.wireOp",EDGE,"E14.28.11"),sQuery(id+"F0.wireOp",EDGE,"E14.28.12"),sQuery(id+"F0.wireOp",EDGE,"E14.29.0"),sQuery(id+"F0.wireOp",EDGE,"E14.29.1"),sQuery(id+"F0.wireOp",EDGE,"E14.29.4"),sQuery(id+"F0.wireOp",EDGE,"E14.29.5"),sQuery(id+"F0.wireOp",EDGE,"E14.29.7"),sQuery(id+"F0.wireOp",EDGE,"E14.29.8"),sQuery(id+"F0.wireOp",EDGE,"E14.29.9"),sQuery(id+"F0.wireOp",EDGE,"E14.29.10"),sQuery(id+"F0.wireOp",EDGE,"E14.29.11"),sQuery(id+"F0.wireOp",EDGE,"E14.29.12"),sQuery(id+"F0.wireOp",EDGE,"E14.30.0"),sQuery(id+"F0.wireOp",EDGE,"E14.30.1"),sQuery(id+"F0.wireOp",EDGE,"E14.30.4"),sQuery(id+"F0.wireOp",EDGE,"E14.30.5"),sQuery(id+"F0.wireOp",EDGE,"E14.30.7"),sQuery(id+"F0.wireOp",EDGE,"E14.30.8"),sQuery(id+"F0.wireOp",EDGE,"E14.30.9"),sQuery(id+"F0.wireOp",EDGE,"E14.30.10"),sQuery(id+"F0.wireOp",EDGE,"E14.30.11"),sQuery(id+"F0.wireOp",EDGE,"E14.30.12"),sQuery(id+"F0.wireOp",EDGE,"E14.31.0"),sQuery(id+"F0.wireOp",EDGE,"E14.31.1"),sQuery(id+"F0.wireOp",EDGE,"E14.31.4"),sQuery(id+"F0.wireOp",EDGE,"E14.31.5"),sQuery(id+"F0.wireOp",EDGE,"E14.31.7"),sQuery(id+"F0.wireOp",EDGE,"E14.31.8"),sQuery(id+"F0.wireOp",EDGE,"E14.31.9"),sQuery(id+"F0.wireOp",EDGE,"E14.31.10"),sQuery(id+"F0.wireOp",EDGE,"E14.31.11"),sQuery(id+"F0.wireOp",EDGE,"E14.31.12"),sQuery(id+"F0.wireOp",EDGE,"E14.32.0"),sQuery(id+"F0.wireOp",EDGE,"E14.32.1"),sQuery(id+"F0.wireOp",EDGE,"E14.32.4"),sQuery(id+"F0.wireOp",EDGE,"E14.32.5"),sQuery(id+"F0.wireOp",EDGE,"E14.32.7"),sQuery(id+"F0.wireOp",EDGE,"E14.32.8"),sQuery(id+"F0.wireOp",EDGE,"E14.32.9"),sQuery(id+"F0.wireOp",EDGE,"E14.32.10"),sQuery(id+"F0.wireOp",EDGE,"E14.32.11"),sQuery(id+"F0.wireOp",EDGE,"E14.32.12"),sQuery(id+"F0.wireOp",EDGE,"E14.33.0"),sQuery(id+"F0.wireOp",EDGE,"E14.33.1"),sQuery(id+"F0.wireOp",EDGE,"E14.33.4"),sQuery(id+"F0.wireOp",EDGE,"E14.33.5"),sQuery(id+"F0.wireOp",EDGE,"E14.33.7"),sQuery(id+"F0.wireOp",EDGE,"E14.33.8"),sQuery(id+"F0.wireOp",EDGE,"E14.33.9"),sQuery(id+"F0.wireOp",EDGE,"E14.33.10"),sQuery(id+"F0.wireOp",EDGE,"E14.33.11"),sQuery(id+"F0.wireOp",EDGE,"E14.33.12"),sQuery(id+"F0.wireOp",EDGE,"E14.34.0"),sQuery(id+"F0.wireOp",EDGE,"E14.34.1"),sQuery(id+"F0.wireOp",EDGE,"E14.34.4"),sQuery(id+"F0.wireOp",EDGE,"E14.34.5"),sQuery(id+"F0.wireOp",EDGE,"E14.34.7"),sQuery(id+"F0.wireOp",EDGE,"E14.34.8"),sQuery(id+"F0.wireOp",EDGE,"E14.34.9"),sQuery(id+"F0.wireOp",EDGE,"E14.34.10"),sQuery(id+"F0.wireOp",EDGE,"E14.34.11"),sQuery(id+"F0.wireOp",EDGE,"E14.34.12"),sQuery(id+"F0.wireOp",EDGE,"E14.35.0"),sQuery(id+"F0.wireOp",EDGE,"E14.35.1"),sQuery(id+"F0.wireOp",EDGE,"E14.35.4"),sQuery(id+"F0.wireOp",EDGE,"E14.35.5"),sQuery(id+"F0.wireOp",EDGE,"E14.35.7"),sQuery(id+"F0.wireOp",EDGE,"E14.35.8"),sQuery(id+"F0.wireOp",EDGE,"E14.35.9"),sQuery(id+"F0.wireOp",EDGE,"E14.35.10"),sQuery(id+"F0.wireOp",EDGE,"E14.35.11"),sQuery(id+"F0.wireOp",EDGE,"E14.35.12"),sQuery(id+"F0.wireOp",EDGE,"E14.36.0"),sQuery(id+"F0.wireOp",EDGE,"E14.36.1"),sQuery(id+"F0.wireOp",EDGE,"E14.36.4"),sQuery(id+"F0.wireOp",EDGE,"E14.36.5"),sQuery(id+"F0.wireOp",EDGE,"E14.36.7"),sQuery(id+"F0.wireOp",EDGE,"E14.36.8"),sQuery(id+"F0.wireOp",EDGE,"E14.36.9"),sQuery(id+"F0.wireOp",EDGE,"E14.36.10"),sQuery(id+"F0.wireOp",EDGE,"E14.36.11"),sQuery(id+"F0.wireOp",EDGE,"E14.36.12"),sQuery(id+"F0.wireOp",EDGE,"E14.37.0"),sQuery(id+"F0.wireOp",EDGE,"E14.37.1"),sQuery(id+"F0.wireOp",EDGE,"E14.37.4"),sQuery(id+"F0.wireOp",EDGE,"E14.37.5"),sQuery(id+"F0.wireOp",EDGE,"E14.37.7"),sQuery(id+"F0.wireOp",EDGE,"E14.37.8"),sQuery(id+"F0.wireOp",EDGE,"E14.37.9"),sQuery(id+"F0.wireOp",EDGE,"E14.37.10"),sQuery(id+"F0.wireOp",EDGE,"E14.37.11"),sQuery(id+"F0.wireOp",EDGE,"E14.37.12"),sQuery(id+"F0.wireOp",EDGE,"E14.38.0"),sQuery(id+"F0.wireOp",EDGE,"E14.38.1"),sQuery(id+"F0.wireOp",EDGE,"E14.38.4"),sQuery(id+"F0.wireOp",EDGE,"E14.38.5"),sQuery(id+"F0.wireOp",EDGE,"E14.38.7"),sQuery(id+"F0.wireOp",EDGE,"E14.38.8"),sQuery(id+"F0.wireOp",EDGE,"E14.38.9"),sQuery(id+"F0.wireOp",EDGE,"E14.38.10"),sQuery(id+"F0.wireOp",EDGE,"E14.38.11"),sQuery(id+"F0.wireOp",EDGE,"E14.38.12"),sQuery(id+"F0.wireOp",EDGE,"E14.39.0"),sQuery(id+"F0.wireOp",EDGE,"E14.39.1"),sQuery(id+"F0.wireOp",EDGE,"E14.39.4"),sQuery(id+"F0.wireOp",EDGE,"E14.39.5"),sQuery(id+"F0.wireOp",EDGE,"E14.39.7"),sQuery(id+"F0.wireOp",EDGE,"E14.39.8"),sQuery(id+"F0.wireOp",EDGE,"E14.39.9"),sQuery(id+"F0.wireOp",EDGE,"E14.39.10"),sQuery(id+"F0.wireOp",EDGE,"E14.39.11"),sQuery(id+"F0.wireOp",EDGE,"E14.39.12"),sQuery(id+"F0.wireOp",EDGE,"E14.40.0"),sQuery(id+"F0.wireOp",EDGE,"E14.40.1"),sQuery(id+"F0.wireOp",EDGE,"E14.40.4"),sQuery(id+"F0.wireOp",EDGE,"E14.40.5"),sQuery(id+"F0.wireOp",EDGE,"E14.40.7"),sQuery(id+"F0.wireOp",EDGE,"E14.40.8"),sQuery(id+"F0.wireOp",EDGE,"E14.40.9"),sQuery(id+"F0.wireOp",EDGE,"E14.40.10"),sQuery(id+"F0.wireOp",EDGE,"E14.40.11"),sQuery(id+"F0.wireOp",EDGE,"E14.40.12"),sQuery(id+"F0.wireOp",EDGE,"E14.41.0"),sQuery(id+"F0.wireOp",EDGE,"E14.41.1"),sQuery(id+"F0.wireOp",EDGE,"E14.41.4"),sQuery(id+"F0.wireOp",EDGE,"E14.41.5"),sQuery(id+"F0.wireOp",EDGE,"E14.41.7"),sQuery(id+"F0.wireOp",EDGE,"E14.41.8"),sQuery(id+"F0.wireOp",EDGE,"E14.41.9"),sQuery(id+"F0.wireOp",EDGE,"E14.41.10"),sQuery(id+"F0.wireOp",EDGE,"E14.41.11"),sQuery(id+"F0.wireOp",EDGE,"E14.41.12"),sQuery(id+"F0.wireOp",EDGE,"E14.42.0"),sQuery(id+"F0.wireOp",EDGE,"E14.42.1"),sQuery(id+"F0.wireOp",EDGE,"E14.42.4"),sQuery(id+"F0.wireOp",EDGE,"E14.42.5"),sQuery(id+"F0.wireOp",EDGE,"E14.42.7"),sQuery(id+"F0.wireOp",EDGE,"E14.42.8"),sQuery(id+"F0.wireOp",EDGE,"E14.42.9"),sQuery(id+"F0.wireOp",EDGE,"E14.42.10"),sQuery(id+"F0.wireOp",EDGE,"E14.42.11"),sQuery(id+"F0.wireOp",EDGE,"E14.42.12"),sQuery(id+"F0.wireOp",EDGE,"E14.43.0"),sQuery(id+"F0.wireOp",EDGE,"E14.43.1"),sQuery(id+"F0.wireOp",EDGE,"E14.43.4"),sQuery(id+"F0.wireOp",EDGE,"E14.43.5"),sQuery(id+"F0.wireOp",EDGE,"E14.43.7"),sQuery(id+"F0.wireOp",EDGE,"E14.43.8"),sQuery(id+"F0.wireOp",EDGE,"E14.43.9"),sQuery(id+"F0.wireOp",EDGE,"E14.43.10"),sQuery(id+"F0.wireOp",EDGE,"E14.43.11"),sQuery(id+"F0.wireOp",EDGE,"E14.43.12"),sQuery(id+"F0.wireOp",EDGE,"E14.44.0"),sQuery(id+"F0.wireOp",EDGE,"E14.44.1"),sQuery(id+"F0.wireOp",EDGE,"E14.44.4"),sQuery(id+"F0.wireOp",EDGE,"E14.44.5"),sQuery(id+"F0.wireOp",EDGE,"E14.44.7"),sQuery(id+"F0.wireOp",EDGE,"E14.44.8"),sQuery(id+"F0.wireOp",EDGE,"E14.44.9"),sQuery(id+"F0.wireOp",EDGE,"E14.44.10"),sQuery(id+"F0.wireOp",EDGE,"E14.44.11"),sQuery(id+"F0.wireOp",EDGE,"E14.44.12"),sQuery(id+"F0.wireOp",EDGE,"E14.45.0"),sQuery(id+"F0.wireOp",EDGE,"E14.45.1"),sQuery(id+"F0.wireOp",EDGE,"E14.45.4"),sQuery(id+"F0.wireOp",EDGE,"E14.45.5"),sQuery(id+"F0.wireOp",EDGE,"E14.45.7"),sQuery(id+"F0.wireOp",EDGE,"E14.45.8"),sQuery(id+"F0.wireOp",EDGE,"E14.45.9"),sQuery(id+"F0.wireOp",EDGE,"E14.45.10"),sQuery(id+"F0.wireOp",EDGE,"E14.45.11"),sQuery(id+"F0.wireOp",EDGE,"E14.45.12"),sQuery(id+"F0.wireOp",EDGE,"E14.46.0"),sQuery(id+"F0.wireOp",EDGE,"E14.46.1"),sQuery(id+"F0.wireOp",EDGE,"E14.46.4"),sQuery(id+"F0.wireOp",EDGE,"E14.46.5"),sQuery(id+"F0.wireOp",EDGE,"E14.46.7"),sQuery(id+"F0.wireOp",EDGE,"E14.46.8"),sQuery(id+"F0.wireOp",EDGE,"E14.46.9"),sQuery(id+"F0.wireOp",EDGE,"E14.46.10"),sQuery(id+"F0.wireOp",EDGE,"E14.46.11"),sQuery(id+"F0.wireOp",EDGE,"E14.46.12"),sQuery(id+"F0.wireOp",EDGE,"E14.47.0"),sQuery(id+"F0.wireOp",EDGE,"E14.47.1"),sQuery(id+"F0.wireOp",EDGE,"E14.47.4"),sQuery(id+"F0.wireOp",EDGE,"E14.47.5"),sQuery(id+"F0.wireOp",EDGE,"E14.47.7"),sQuery(id+"F0.wireOp",EDGE,"E14.47.8"),sQuery(id+"F0.wireOp",EDGE,"E14.47.9"),sQuery(id+"F0.wireOp",EDGE,"E14.47.10"),sQuery(id+"F0.wireOp",EDGE,"E14.47.11"),sQuery(id+"F0.wireOp",EDGE,"E14.47.12"),sQuery(id+"F0.wireOp",EDGE,"E14.48.0"),sQuery(id+"F0.wireOp",EDGE,"E14.48.1"),sQuery(id+"F0.wireOp",EDGE,"E14.48.4"),sQuery(id+"F0.wireOp",EDGE,"E14.48.5"),sQuery(id+"F0.wireOp",EDGE,"E14.48.7"),sQuery(id+"F0.wireOp",EDGE,"E14.48.8"),sQuery(id+"F0.wireOp",EDGE,"E14.48.9"),sQuery(id+"F0.wireOp",EDGE,"E14.48.10"),sQuery(id+"F0.wireOp",EDGE,"E14.48.11"),sQuery(id+"F0.wireOp",EDGE,"E14.48.12"),sQuery(id+"F0.wireOp",EDGE,"E14.49.0"),sQuery(id+"F0.wireOp",EDGE,"E14.49.1"),sQuery(id+"F0.wireOp",EDGE,"E14.49.4"),sQuery(id+"F0.wireOp",EDGE,"E14.49.5"),sQuery(id+"F0.wireOp",EDGE,"E14.49.7"),sQuery(id+"F0.wireOp",EDGE,"E14.49.8"),sQuery(id+"F0.wireOp",EDGE,"E14.49.9"),sQuery(id+"F0.wireOp",EDGE,"E14.49.10"),sQuery(id+"F0.wireOp",EDGE,"E14.49.11"),sQuery(id+"F0.wireOp",EDGE,"E14.49.12"),sQuery(id+"F0.wireOp",EDGE,"E14.50.0"),sQuery(id+"F0.wireOp",EDGE,"E14.50.1"),sQuery(id+"F0.wireOp",EDGE,"E14.50.4"),sQuery(id+"F0.wireOp",EDGE,"E14.50.5"),sQuery(id+"F0.wireOp",EDGE,"E14.50.7"),sQuery(id+"F0.wireOp",EDGE,"E14.50.8"),sQuery(id+"F0.wireOp",EDGE,"E14.50.9"),sQuery(id+"F0.wireOp",EDGE,"E14.50.10"),sQuery(id+"F0.wireOp",EDGE,"E14.50.11"),sQuery(id+"F0.wireOp",EDGE,"E14.50.12"),sQuery(id+"F0.wireOp",EDGE,"E14.51.0"),sQuery(id+"F0.wireOp",EDGE,"E14.51.1"),sQuery(id+"F0.wireOp",EDGE,"E14.51.4"),sQuery(id+"F0.wireOp",EDGE,"E14.51.5"),sQuery(id+"F0.wireOp",EDGE,"E14.51.7"),sQuery(id+"F0.wireOp",EDGE,"E14.51.8"),sQuery(id+"F0.wireOp",EDGE,"E14.51.9"),sQuery(id+"F0.wireOp",EDGE,"E14.51.10"),sQuery(id+"F0.wireOp",EDGE,"E14.51.11"),sQuery(id+"F0.wireOp",EDGE,"E14.51.12"),sQuery(id+"F0.wireOp",EDGE,"E14.52.0"),sQuery(id+"F0.wireOp",EDGE,"E14.52.1"),sQuery(id+"F0.wireOp",EDGE,"E14.52.4"),sQuery(id+"F0.wireOp",EDGE,"E14.52.5"),sQuery(id+"F0.wireOp",EDGE,"E14.52.7"),sQuery(id+"F0.wireOp",EDGE,"E14.52.8"),sQuery(id+"F0.wireOp",EDGE,"E14.52.9"),sQuery(id+"F0.wireOp",EDGE,"E14.52.10"),sQuery(id+"F0.wireOp",EDGE,"E14.52.11"),sQuery(id+"F0.wireOp",EDGE,"E14.52.12"),sQuery(id+"F0.wireOp",EDGE,"E14.53.0"),sQuery(id+"F0.wireOp",EDGE,"E14.53.1"),sQuery(id+"F0.wireOp",EDGE,"E14.53.4"),sQuery(id+"F0.wireOp",EDGE,"E14.53.5"),sQuery(id+"F0.wireOp",EDGE,"E14.53.7"),sQuery(id+"F0.wireOp",EDGE,"E14.53.8"),sQuery(id+"F0.wireOp",EDGE,"E14.53.9"),sQuery(id+"F0.wireOp",EDGE,"E14.53.10"),sQuery(id+"F0.wireOp",EDGE,"E14.53.11"),sQuery(id+"F0.wireOp",EDGE,"E14.53.12"),sQuery(id+"F0.wireOp",EDGE,"E14.54.0"),sQuery(id+"F0.wireOp",EDGE,"E14.54.1"),sQuery(id+"F0.wireOp",EDGE,"E14.54.4"),sQuery(id+"F0.wireOp",EDGE,"E14.54.5"),sQuery(id+"F0.wireOp",EDGE,"E14.54.7"),sQuery(id+"F0.wireOp",EDGE,"E14.54.8"),sQuery(id+"F0.wireOp",EDGE,"E14.54.9"),sQuery(id+"F0.wireOp",EDGE,"E14.54.10"),sQuery(id+"F0.wireOp",EDGE,"E14.54.11"),sQuery(id+"F0.wireOp",EDGE,"E14.54.12"),sQuery(id+"F0.wireOp",EDGE,"E14.55.0"),sQuery(id+"F0.wireOp",EDGE,"E14.55.1"),sQuery(id+"F0.wireOp",EDGE,"E14.55.4"),sQuery(id+"F0.wireOp",EDGE,"E14.55.5"),sQuery(id+"F0.wireOp",EDGE,"E14.55.7"),sQuery(id+"F0.wireOp",EDGE,"E14.55.8"),sQuery(id+"F0.wireOp",EDGE,"E14.55.9"),sQuery(id+"F0.wireOp",EDGE,"E14.55.10"),sQuery(id+"F0.wireOp",EDGE,"E14.55.11"),sQuery(id+"F0.wireOp",EDGE,"E14.55.12"),sQuery(id+"F0.wireOp",EDGE,"E14.56.0"),sQuery(id+"F0.wireOp",EDGE,"E14.56.1"),sQuery(id+"F0.wireOp",EDGE,"E14.56.4"),sQuery(id+"F0.wireOp",EDGE,"E14.56.5"),sQuery(id+"F0.wireOp",EDGE,"E14.56.7"),sQuery(id+"F0.wireOp",EDGE,"E14.56.8"),sQuery(id+"F0.wireOp",EDGE,"E14.56.9"),sQuery(id+"F0.wireOp",EDGE,"E14.56.10"),sQuery(id+"F0.wireOp",EDGE,"E14.56.11"),sQuery(id+"F0.wireOp",EDGE,"E14.56.12"),sQuery(id+"F0.wireOp",EDGE,"E14.57.0"),sQuery(id+"F0.wireOp",EDGE,"E14.57.1"),sQuery(id+"F0.wireOp",EDGE,"E14.57.4"),sQuery(id+"F0.wireOp",EDGE,"E14.57.5"),sQuery(id+"F0.wireOp",EDGE,"E14.57.7"),sQuery(id+"F0.wireOp",EDGE,"E14.57.8"),sQuery(id+"F0.wireOp",EDGE,"E14.57.9"),sQuery(id+"F0.wireOp",EDGE,"E14.57.10"),sQuery(id+"F0.wireOp",EDGE,"E14.57.11"),sQuery(id+"F0.wireOp",EDGE,"E14.57.12"),sQuery(id+"F0.wireOp",EDGE,"E14.58.0"),sQuery(id+"F0.wireOp",EDGE,"E14.58.1"),sQuery(id+"F0.wireOp",EDGE,"E14.58.4"),sQuery(id+"F0.wireOp",EDGE,"E14.58.5"),sQuery(id+"F0.wireOp",EDGE,"E14.58.7"),sQuery(id+"F0.wireOp",EDGE,"E14.58.8"),sQuery(id+"F0.wireOp",EDGE,"E14.58.9"),sQuery(id+"F0.wireOp",EDGE,"E14.58.10"),sQuery(id+"F0.wireOp",EDGE,"E14.58.11"),sQuery(id+"F0.wireOp",EDGE,"E14.58.12"),sQuery(id+"F0.wireOp",EDGE,"E14.59.0"),sQuery(id+"F0.wireOp",EDGE,"E14.59.1"),sQuery(id+"F0.wireOp",EDGE,"E14.59.4"),sQuery(id+"F0.wireOp",EDGE,"E14.59.5"),sQuery(id+"F0.wireOp",EDGE,"E14.59.7"),sQuery(id+"F0.wireOp",EDGE,"E14.59.8"),sQuery(id+"F0.wireOp",EDGE,"E14.59.9"),sQuery(id+"F0.wireOp",EDGE,"E14.59.10"),sQuery(id+"F0.wireOp",EDGE,"E14.59.11"),sQuery(id+"F0.wireOp",EDGE,"E14.59.12"),sQuery(id+"F0.wireOp",EDGE,"E14.60.0"),sQuery(id+"F0.wireOp",EDGE,"E14.60.1"),sQuery(id+"F0.wireOp",EDGE,"E14.60.4"),sQuery(id+"F0.wireOp",EDGE,"E14.60.5"),sQuery(id+"F0.wireOp",EDGE,"E14.60.7"),sQuery(id+"F0.wireOp",EDGE,"E14.60.8"),sQuery(id+"F0.wireOp",EDGE,"E14.60.9"),sQuery(id+"F0.wireOp",EDGE,"E14.60.10"),sQuery(id+"F0.wireOp",EDGE,"E14.60.11"),sQuery(id+"F0.wireOp",EDGE,"E14.60.12"),sQuery(id+"F0.wireOp",EDGE,"E14.61.0"),sQuery(id+"F0.wireOp",EDGE,"E14.61.1"),sQuery(id+"F0.wireOp",EDGE,"E14.61.4"),sQuery(id+"F0.wireOp",EDGE,"E14.61.5"),sQuery(id+"F0.wireOp",EDGE,"E14.61.7"),sQuery(id+"F0.wireOp",EDGE,"E14.61.8"),sQuery(id+"F0.wireOp",EDGE,"E14.61.9"),sQuery(id+"F0.wireOp",EDGE,"E14.61.10"),sQuery(id+"F0.wireOp",EDGE,"E14.61.11"),sQuery(id+"F0.wireOp",EDGE,"E14.61.12"),sQuery(id+"F0.wireOp",EDGE,"E14.62.0"),sQuery(id+"F0.wireOp",EDGE,"E14.62.1"),sQuery(id+"F0.wireOp",EDGE,"E14.62.4"),sQuery(id+"F0.wireOp",EDGE,"E14.62.5"),sQuery(id+"F0.wireOp",EDGE,"E14.62.7"),sQuery(id+"F0.wireOp",EDGE,"E14.62.8"),sQuery(id+"F0.wireOp",EDGE,"E14.62.9"),sQuery(id+"F0.wireOp",EDGE,"E14.62.10"),sQuery(id+"F0.wireOp",EDGE,"E14.62.11"),sQuery(id+"F0.wireOp",EDGE,"E14.62.12"),sQuery(id+"F0.wireOp",EDGE,"E14.63.0"),sQuery(id+"F0.wireOp",EDGE,"E14.63.1"),sQuery(id+"F0.wireOp",EDGE,"E14.63.4"),sQuery(id+"F0.wireOp",EDGE,"E14.63.5"),sQuery(id+"F0.wireOp",EDGE,"E14.63.7"),sQuery(id+"F0.wireOp",EDGE,"E14.63.8"),sQuery(id+"F0.wireOp",EDGE,"E14.63.9"),sQuery(id+"F0.wireOp",EDGE,"E14.63.10"),sQuery(id+"F0.wireOp",EDGE,"E14.63.11"),sQuery(id+"F0.wireOp",EDGE,"E14.63.12"),sQuery(id+"F0.wireOp",EDGE,"E14.64.0"),sQuery(id+"F0.wireOp",EDGE,"E14.64.1"),sQuery(id+"F0.wireOp",EDGE,"E14.64.4"),sQuery(id+"F0.wireOp",EDGE,"E14.64.5"),sQuery(id+"F0.wireOp",EDGE,"E14.64.7"),sQuery(id+"F0.wireOp",EDGE,"E14.64.8"),sQuery(id+"F0.wireOp",EDGE,"E14.64.9"),sQuery(id+"F0.wireOp",EDGE,"E14.64.10"),sQuery(id+"F0.wireOp",EDGE,"E14.64.11"),sQuery(id+"F0.wireOp",EDGE,"E14.64.12"),sQuery(id+"F0.wireOp",EDGE,"E14.65.0"),sQuery(id+"F0.wireOp",EDGE,"E14.65.1"),sQuery(id+"F0.wireOp",EDGE,"E14.65.4"),sQuery(id+"F0.wireOp",EDGE,"E14.65.5"),sQuery(id+"F0.wireOp",EDGE,"E14.65.7"),sQuery(id+"F0.wireOp",EDGE,"E14.65.8"),sQuery(id+"F0.wireOp",EDGE,"E14.65.9"),sQuery(id+"F0.wireOp",EDGE,"E14.65.10"),sQuery(id+"F0.wireOp",EDGE,"E14.65.11"),sQuery(id+"F0.wireOp",EDGE,"E14.65.12"),sQuery(id+"F0.wireOp",EDGE,"E14.66.0"),sQuery(id+"F0.wireOp",EDGE,"E14.66.1"),sQuery(id+"F0.wireOp",EDGE,"E14.66.4"),sQuery(id+"F0.wireOp",EDGE,"E14.66.5"),sQuery(id+"F0.wireOp",EDGE,"E14.66.7"),sQuery(id+"F0.wireOp",EDGE,"E14.66.8"),sQuery(id+"F0.wireOp",EDGE,"E14.66.9"),sQuery(id+"F0.wireOp",EDGE,"E14.66.10"),sQuery(id+"F0.wireOp",EDGE,"E14.66.11"),sQuery(id+"F0.wireOp",EDGE,"E14.66.12"),sQuery(id+"F0.wireOp",EDGE,"E14.67.0"),sQuery(id+"F0.wireOp",EDGE,"E14.67.1"),sQuery(id+"F0.wireOp",EDGE,"E14.67.4"),sQuery(id+"F0.wireOp",EDGE,"E14.67.5"),sQuery(id+"F0.wireOp",EDGE,"E14.67.7"),sQuery(id+"F0.wireOp",EDGE,"E14.67.8"),sQuery(id+"F0.wireOp",EDGE,"E14.67.9"),sQuery(id+"F0.wireOp",EDGE,"E14.67.10"),sQuery(id+"F0.wireOp",EDGE,"E14.67.11"),sQuery(id+"F0.wireOp",EDGE,"E14.67.12"),sQuery(id+"F0.wireOp",EDGE,"E14.68.0"),sQuery(id+"F0.wireOp",EDGE,"E14.68.1"),sQuery(id+"F0.wireOp",EDGE,"E14.68.4"),sQuery(id+"F0.wireOp",EDGE,"E14.68.5"),sQuery(id+"F0.wireOp",EDGE,"E14.68.7"),sQuery(id+"F0.wireOp",EDGE,"E14.68.8"),sQuery(id+"F0.wireOp",EDGE,"E14.68.9"),sQuery(id+"F0.wireOp",EDGE,"E14.68.10"),sQuery(id+"F0.wireOp",EDGE,"E14.68.11"),sQuery(id+"F0.wireOp",EDGE,"E14.68.12"),sQuery(id+"F0.wireOp",EDGE,"E14.69.0"),sQuery(id+"F0.wireOp",EDGE,"E14.69.1"),sQuery(id+"F0.wireOp",EDGE,"E14.69.4"),sQuery(id+"F0.wireOp",EDGE,"E14.69.5"),sQuery(id+"F0.wireOp",EDGE,"E14.69.7"),sQuery(id+"F0.wireOp",EDGE,"E14.69.8"),sQuery(id+"F0.wireOp",EDGE,"E14.69.9"),sQuery(id+"F0.wireOp",EDGE,"E14.69.10"),sQuery(id+"F0.wireOp",EDGE,"E14.69.11"),sQuery(id+"F0.wireOp",EDGE,"E14.69.12"),sQuery(id+"F0.wireOp",EDGE,"E14.70.0"),sQuery(id+"F0.wireOp",EDGE,"E14.70.1"),sQuery(id+"F0.wireOp",EDGE,"E14.70.4"),sQuery(id+"F0.wireOp",EDGE,"E14.70.5"),sQuery(id+"F0.wireOp",EDGE,"E14.70.7"),sQuery(id+"F0.wireOp",EDGE,"E14.70.8"),sQuery(id+"F0.wireOp",EDGE,"E14.70.9"),sQuery(id+"F0.wireOp",EDGE,"E14.70.10"),sQuery(id+"F0.wireOp",EDGE,"E14.70.11"),sQuery(id+"F0.wireOp",EDGE,"E14.70.12"),sQuery(id+"F0.wireOp",EDGE,"E14.71.0"),sQuery(id+"F0.wireOp",EDGE,"E14.71.1"),sQuery(id+"F0.wireOp",EDGE,"E14.71.4"),sQuery(id+"F0.wireOp",EDGE,"E14.71.5"),sQuery(id+"F0.wireOp",EDGE,"E14.71.7"),sQuery(id+"F0.wireOp",EDGE,"E14.71.8"),sQuery(id+"F0.wireOp",EDGE,"E14.71.9"),sQuery(id+"F0.wireOp",EDGE,"E14.71.10"),sQuery(id+"F0.wireOp",EDGE,"E14.71.11"),sQuery(id+"F0.wireOp",EDGE,"E14.71.12"),sQuery(id+"F0.wireOp",EDGE,"E15.trimOffspring"),sQuery(id+"F0.wireOp",EDGE,"E16.trimOffspring"),sQuery(id+"F0.wireOp",EDGE,"E17.trimOffspring"),sQuery(id+"F0.wireOp",EDGE,"E18.trimOffspring"),sQuery(id+"F0.wireOp",EDGE,"E19.trimOffspring"),sQuery(id+"F0.wireOp",EDGE,"E20.trimOffspring"),sQuery(id+"F0.wireOp",EDGE,"E21.trimOffspring"),sQuery(id+"F0.wireOp",EDGE,"E22.trimOffspring"),sQuery(id+"F0.wireOp",EDGE,"E23.trimOffspring"),sQuery(id+"F0.wireOp",EDGE,"E24.trimOffspring"),sQuery(id+"F0.wireOp",EDGE,"E25.trimOffspring"),sQuery(id+"F0.wireOp",EDGE,"E26.trimOffspring"),sQuery(id+"F0.wireOp",EDGE,"E27.trimOffspring"),sQuery(id+"F0.wireOp",EDGE,"E28.trimOffspring"),sQuery(id+"F0.wireOp",EDGE,"E29.trimOffspring"),sQuery(id+"F0.wireOp",EDGE,"E30.trimOffspring"),sQuery(id+"F0.wireOp",EDGE,"E31.trimOffspring"),sQuery(id+"F0.wireOp",EDGE,"E32.trimOffspring"),sQuery(id+"F0.wireOp",EDGE,"E33.trimOffspring"),sQuery(id+"F0.wireOp",EDGE,"E34.trimOffspring"),sQuery(id+"F0.wireOp",EDGE,"E35.trimOffspring"),sQuery(id+"F0.wireOp",EDGE,"E36.trimOffspring"),sQuery(id+"F0.wireOp",EDGE,"E37.trimOffspring"),sQuery(id+"F0.wireOp",EDGE,"E38.trimOffspring"),sQuery(id+"F0.wireOp",EDGE,"E39.trimOffspring"),sQuery(id+"F0.wireOp",EDGE,"E40.trimOffspring"),sQuery(id+"F0.wireOp",EDGE,"E41.trimOffspring"),sQuery(id+"F0.wireOp",EDGE,"E42.trimOffspring"),sQuery(id+"F0.wireOp",EDGE,"E43.trimOffspring"),sQuery(id+"F0.wireOp",EDGE,"E44.trimOffspring"),sQuery(id+"F0.wireOp",EDGE,"E45.trimOffspring"),sQuery(id+"F0.wireOp",EDGE,"E46.trimOffspring"),sQuery(id+"F0.wireOp",EDGE,"E47.trimOffspring"),sQuery(id+"F0.wireOp",EDGE,"E48.trimOffspring"),sQuery(id+"F0.wireOp",EDGE,"E49.trimOffspring"),sQuery(id+"F0.wireOp",EDGE,"E50.trimOffspring"),sQuery(id+"F0.wireOp",EDGE,"E51.trimOffspring"),sQuery(id+"F0.wireOp",EDGE,"E52.trimOffspring"),sQuery(id+"F0.wireOp",EDGE,"E53.trimOffspring"),sQuery(id+"F0.wireOp",EDGE,"E54.trimOffspring"),sQuery(id+"F0.wireOp",EDGE,"E55.trimOffspring"),sQuery(id+"F0.wireOp",EDGE,"E56.trimOffspring"),sQuery(id+"F0.wireOp",EDGE,"E57.trimOffspring"),sQuery(id+"F0.wireOp",EDGE,"E58.trimOffspring"),sQuery(id+"F0.wireOp",EDGE,"E59.trimOffspring"),sQuery(id+"F0.wireOp",EDGE,"E60.trimOffspring"),sQuery(id+"F0.wireOp",EDGE,"E61.trimOffspring"),sQuery(id+"F0.wireOp",EDGE,"E62.trimOffspring"),sQuery(id+"F0.wireOp",EDGE,"E63.trimOffspring"),sQuery(id+"F0.wireOp",EDGE,"E64.trimOffspring"),sQuery(id+"F0.wireOp",EDGE,"E65.trimOffspring"),sQuery(id+"F0.wireOp",EDGE,"E66.trimOffspring"),sQuery(id+"F0.wireOp",EDGE,"E67.trimOffspring"),sQuery(id+"F0.wireOp",EDGE,"E68.trimOffspring"),sQuery(id+"F0.wireOp",EDGE,"E69.trimOffspring"),sQuery(id+"F0.wireOp",EDGE,"E70.trimOffspring"),sQuery(id+"F0.wireOp",EDGE,"E71.trimOffspring"),sQuery(id+"F0.wireOp",EDGE,"E72.trimOffspring"),sQuery(id+"F0.wireOp",EDGE,"E73.trimOffspring"),sQuery(id+"F0.wireOp",EDGE,"E74.trimOffspring"),sQuery(id+"F0.wireOp",EDGE,"E75.trimOffspring"),sQuery(id+"F0.wireOp",EDGE,"E76.trimOffspring"),sQuery(id+"F0.wireOp",EDGE,"E77.trimOffspring"),sQuery(id+"F0.wireOp",EDGE,"E78.trimOffspring"),sQuery(id+"F0.wireOp",EDGE,"E79.trimOffspring"),sQuery(id+"F0.wireOp",EDGE,"E80.trimOffspring"),sQuery(id+"F0.wireOp",EDGE,"E81.trimOffspring"),sQuery(id+"F0.wireOp",EDGE,"E82.trimOffspring"),sQuery(id+"F0.wireOp",EDGE,"E83.trimOffspring"),sQuery(id+"F0.wireOp",EDGE,"E84.trimOffspring"),sQuery(id+"F0.wireOp",EDGE,"E85.trimOffspring")])]});
            hole(context, id + "F7", {"style" : HoleStyle.SIMPLE, "endStyle" : HoleEndStyle.THROUGH, "holeDiameter" : 6.35 * mm, "locations" : qUnion([Q0, Q1, Q2]), "scope" : qUnion([Q3]), "isTappedThrough" : true});
        }
    });
